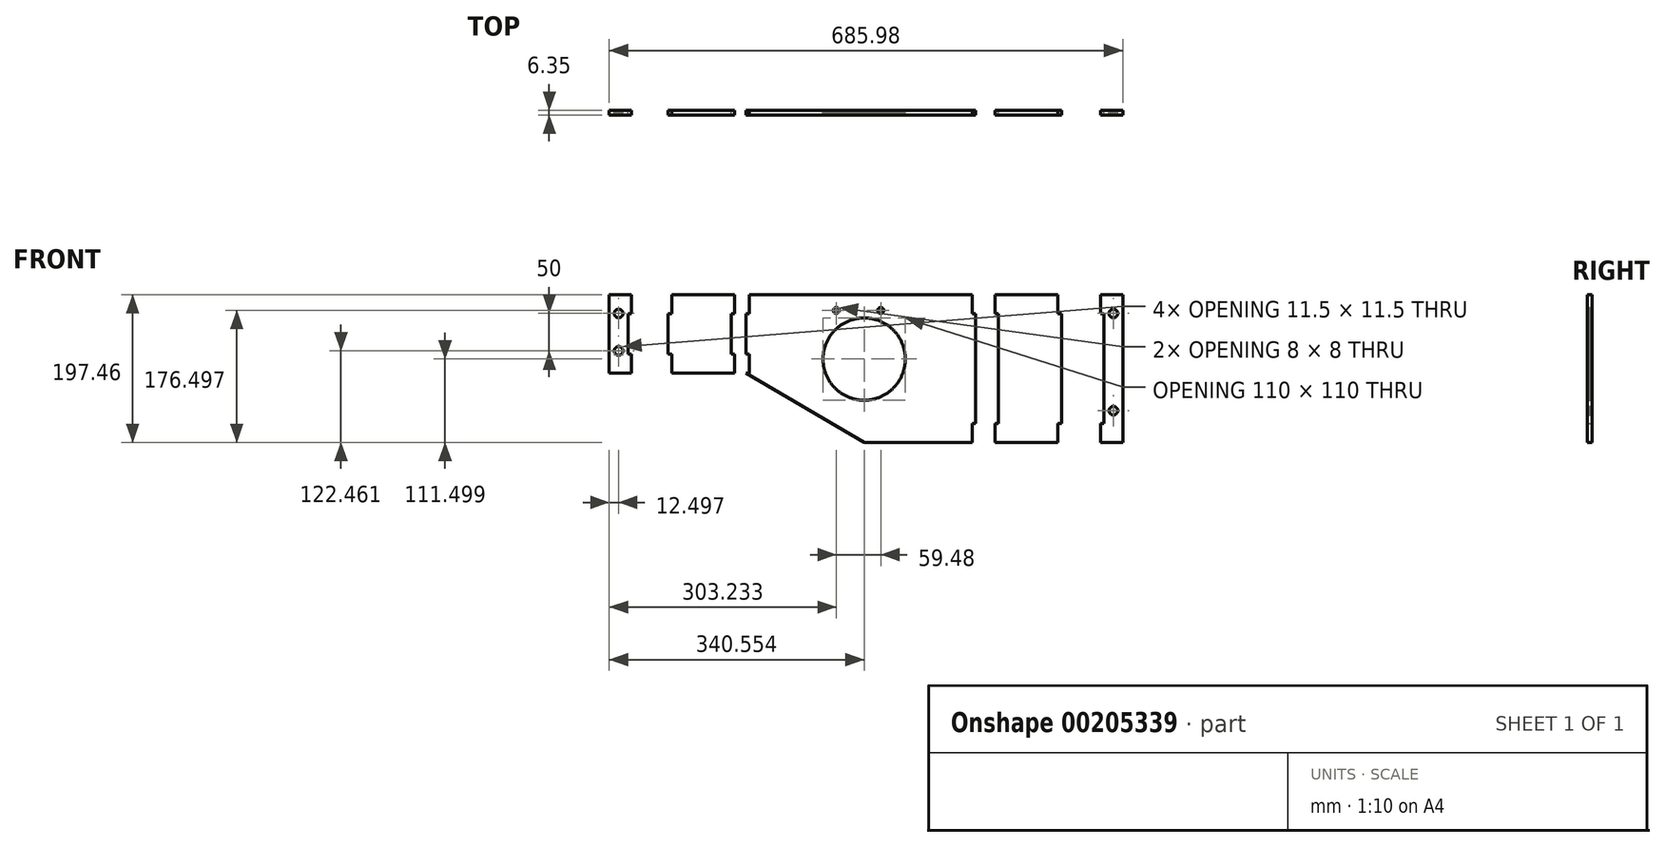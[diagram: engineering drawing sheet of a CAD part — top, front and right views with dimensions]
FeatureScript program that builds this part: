
annotation { "Feature Type Name" : "Feature", "Feature Type Description" : "" }
export const myFeature = defineFeature(function(context is Context, id is Id, definition is map)
    precondition{}
    {
        {
            var Q0;
            Q0=qCreatedBy(makeId("Front.planeOp"),FACE);
            var sketch = newSketch(context, id + "F0", { "sketchPlane" : qUnion([Q0])});
            skLineSegment(sketch, "E0", {"start": v(-330.5, 79.48) * mm, "end": v(-330.36, 79.48) * mm});
            skLineSegment(sketch, "E1", {"start": v(-330.36, 79.48) * mm, "end": v(-330.24, 79.48) * mm});
            skLineSegment(sketch, "E2", {"start": v(-330.24, 79.48) * mm, "end": v(-330.1, 79.47) * mm});
            skLineSegment(sketch, "E3", {"start": v(-330.1, 79.47) * mm, "end": v(-329.98, 79.46) * mm});
            skLineSegment(sketch, "E4", {"start": v(-329.98, 79.46) * mm, "end": v(-329.84, 79.44) * mm});
            skLineSegment(sketch, "E5", {"start": v(-329.84, 79.44) * mm, "end": v(-329.71, 79.43) * mm});
            skLineSegment(sketch, "E6", {"start": v(-329.71, 79.43) * mm, "end": v(-329.58, 79.4) * mm});
            skLineSegment(sketch, "E7", {"start": v(-329.58, 79.4) * mm, "end": v(-329.45, 79.39) * mm});
            skLineSegment(sketch, "E8", {"start": v(-329.45, 79.39) * mm, "end": v(-329.31, 79.36) * mm});
            skLineSegment(sketch, "E9", {"start": v(-329.31, 79.36) * mm, "end": v(-329.18, 79.33) * mm});
            skLineSegment(sketch, "E10", {"start": v(-329.18, 79.33) * mm, "end": v(-329.04, 79.3) * mm});
            skLineSegment(sketch, "E11", {"start": v(-329.04, 79.3) * mm, "end": v(-328.91, 79.26) * mm});
            skLineSegment(sketch, "E12", {"start": v(-328.91, 79.26) * mm, "end": v(-328.78, 79.22) * mm});
            skLineSegment(sketch, "E13", {"start": v(-328.78, 79.22) * mm, "end": v(-328.64, 79.18) * mm});
            skLineSegment(sketch, "E14", {"start": v(-328.64, 79.18) * mm, "end": v(-328.5, 79.13) * mm});
            skLineSegment(sketch, "E15", {"start": v(-328.5, 79.13) * mm, "end": v(-328.38, 79.08) * mm});
            skLineSegment(sketch, "E16", {"start": v(-328.38, 79.08) * mm, "end": v(-328.24, 79.02) * mm});
            skLineSegment(sketch, "E17", {"start": v(-328.24, 79.02) * mm, "end": v(-328.11, 78.97) * mm});
            skLineSegment(sketch, "E18", {"start": v(-328.11, 78.97) * mm, "end": v(-327.98, 78.9) * mm});
            skLineSegment(sketch, "E19", {"start": v(-327.98, 78.9) * mm, "end": v(-327.85, 78.84) * mm});
            skLineSegment(sketch, "E20", {"start": v(-327.85, 78.84) * mm, "end": v(-327.72, 78.77) * mm});
            skLineSegment(sketch, "E21", {"start": v(-327.72, 78.77) * mm, "end": v(-327.6, 78.7) * mm});
            skLineSegment(sketch, "E22", {"start": v(-327.6, 78.7) * mm, "end": v(-327.47, 78.62) * mm});
            skLineSegment(sketch, "E23", {"start": v(-327.47, 78.62) * mm, "end": v(-327.35, 78.54) * mm});
            skLineSegment(sketch, "E24", {"start": v(-327.35, 78.54) * mm, "end": v(-327.22, 78.46) * mm});
            skLineSegment(sketch, "E25", {"start": v(-327.22, 78.46) * mm, "end": v(-327.1, 78.38) * mm});
            skLineSegment(sketch, "E26", {"start": v(-327.1, 78.38) * mm, "end": v(-326.98, 78.29) * mm});
            skLineSegment(sketch, "E27", {"start": v(-326.98, 78.29) * mm, "end": v(-326.87, 78.2) * mm});
            skLineSegment(sketch, "E28", {"start": v(-326.87, 78.2) * mm, "end": v(-326.75, 78.1) * mm});
            skLineSegment(sketch, "E29", {"start": v(-326.75, 78.1) * mm, "end": v(-326.64, 78) * mm});
            skLineSegment(sketch, "E30", {"start": v(-326.64, 78) * mm, "end": v(-326.53, 77.9) * mm});
            skLineSegment(sketch, "E31", {"start": v(-326.53, 77.9) * mm, "end": v(-326.43, 77.8) * mm});
            skLineSegment(sketch, "E32", {"start": v(-326.43, 77.8) * mm, "end": v(-326.32, 77.7) * mm});
            skLineSegment(sketch, "E33", {"start": v(-326.32, 77.7) * mm, "end": v(-326.22, 77.58) * mm});
            skLineSegment(sketch, "E34", {"start": v(-326.22, 77.58) * mm, "end": v(-326.12, 77.47) * mm});
            skLineSegment(sketch, "E35", {"start": v(-326.12, 77.47) * mm, "end": v(-326.03, 77.36) * mm});
            skLineSegment(sketch, "E36", {"start": v(-326.03, 77.36) * mm, "end": v(-325.94, 77.24) * mm});
            skLineSegment(sketch, "E37", {"start": v(-325.94, 77.24) * mm, "end": v(-325.85, 77.12) * mm});
            skLineSegment(sketch, "E38", {"start": v(-325.85, 77.12) * mm, "end": v(-325.76, 77) * mm});
            skLineSegment(sketch, "E39", {"start": v(-325.76, 77) * mm, "end": v(-325.68, 76.88) * mm});
            skLineSegment(sketch, "E40", {"start": v(-325.68, 76.88) * mm, "end": v(-325.6, 76.75) * mm});
            skLineSegment(sketch, "E41", {"start": v(-325.6, 76.75) * mm, "end": v(-325.53, 76.63) * mm});
            skLineSegment(sketch, "E42", {"start": v(-325.53, 76.63) * mm, "end": v(-325.45, 76.5) * mm});
            skLineSegment(sketch, "E43", {"start": v(-325.45, 76.5) * mm, "end": v(-325.38, 76.37) * mm});
            skLineSegment(sketch, "E44", {"start": v(-325.38, 76.37) * mm, "end": v(-325.32, 76.24) * mm});
            skLineSegment(sketch, "E45", {"start": v(-325.32, 76.24) * mm, "end": v(-325.26, 76.11) * mm});
            skLineSegment(sketch, "E46", {"start": v(-325.26, 76.11) * mm, "end": v(-325.2, 75.98) * mm});
            skLineSegment(sketch, "E47", {"start": v(-325.2, 75.98) * mm, "end": v(-325.15, 75.85) * mm});
            skLineSegment(sketch, "E48", {"start": v(-325.15, 75.85) * mm, "end": v(-325.1, 75.71) * mm});
            skLineSegment(sketch, "E49", {"start": v(-325.1, 75.71) * mm, "end": v(-325.05, 75.58) * mm});
            skLineSegment(sketch, "E50", {"start": v(-325.05, 75.58) * mm, "end": v(-325, 75.45) * mm});
            skLineSegment(sketch, "E51", {"start": v(-325, 75.45) * mm, "end": v(-324.96, 75.31) * mm});
            skLineSegment(sketch, "E52", {"start": v(-324.96, 75.31) * mm, "end": v(-324.93, 75.18) * mm});
            skLineSegment(sketch, "E53", {"start": v(-324.93, 75.18) * mm, "end": v(-324.9, 75.05) * mm});
            skLineSegment(sketch, "E54", {"start": v(-324.9, 75.05) * mm, "end": v(-324.87, 74.91) * mm});
            skLineSegment(sketch, "E55", {"start": v(-324.87, 74.91) * mm, "end": v(-324.84, 74.78) * mm});
            skLineSegment(sketch, "E56", {"start": v(-324.84, 74.78) * mm, "end": v(-324.82, 74.64) * mm});
            skLineSegment(sketch, "E57", {"start": v(-324.82, 74.64) * mm, "end": v(-324.8, 74.51) * mm});
            skLineSegment(sketch, "E58", {"start": v(-324.8, 74.51) * mm, "end": v(-324.78, 74.38) * mm});
            skLineSegment(sketch, "E59", {"start": v(-324.78, 74.38) * mm, "end": v(-324.77, 74.25) * mm});
            skLineSegment(sketch, "E60", {"start": v(-324.77, 74.25) * mm, "end": v(-324.76, 74.12) * mm});
            skLineSegment(sketch, "E61", {"start": v(-324.76, 74.12) * mm, "end": v(-324.75, 73.99) * mm});
            skLineSegment(sketch, "E62", {"start": v(-324.75, 73.99) * mm, "end": v(-324.74, 73.86) * mm});
            skLineSegment(sketch, "E63", {"start": v(-324.74, 73.86) * mm, "end": v(-324.74, 73.73) * mm});
            skLineSegment(sketch, "E64", {"start": v(-324.74, 73.73) * mm, "end": v(-324.74, 73.6) * mm});
            skLineSegment(sketch, "E65", {"start": v(-324.74, 73.6) * mm, "end": v(-324.75, 73.47) * mm});
            skLineSegment(sketch, "E66", {"start": v(-324.75, 73.47) * mm, "end": v(-324.76, 73.35) * mm});
            skLineSegment(sketch, "E67", {"start": v(-324.76, 73.35) * mm, "end": v(-324.77, 73.21) * mm});
            skLineSegment(sketch, "E68", {"start": v(-324.77, 73.21) * mm, "end": v(-324.78, 73.08) * mm});
            skLineSegment(sketch, "E69", {"start": v(-324.78, 73.08) * mm, "end": v(-324.8, 72.95) * mm});
            skLineSegment(sketch, "E70", {"start": v(-324.8, 72.95) * mm, "end": v(-324.82, 72.82) * mm});
            skLineSegment(sketch, "E71", {"start": v(-324.82, 72.82) * mm, "end": v(-324.84, 72.68) * mm});
            skLineSegment(sketch, "E72", {"start": v(-324.84, 72.68) * mm, "end": v(-324.87, 72.55) * mm});
            skLineSegment(sketch, "E73", {"start": v(-324.87, 72.55) * mm, "end": v(-324.9, 72.42) * mm});
            skLineSegment(sketch, "E74", {"start": v(-324.9, 72.42) * mm, "end": v(-324.93, 72.28) * mm});
            skLineSegment(sketch, "E75", {"start": v(-324.93, 72.28) * mm, "end": v(-324.96, 72.15) * mm});
            skLineSegment(sketch, "E76", {"start": v(-324.96, 72.15) * mm, "end": v(-325, 72.02) * mm});
            skLineSegment(sketch, "E77", {"start": v(-325, 72.02) * mm, "end": v(-325.05, 71.88) * mm});
            skLineSegment(sketch, "E78", {"start": v(-325.05, 71.88) * mm, "end": v(-325.1, 71.75) * mm});
            skLineSegment(sketch, "E79", {"start": v(-325.1, 71.75) * mm, "end": v(-325.15, 71.61) * mm});
            skLineSegment(sketch, "E80", {"start": v(-325.15, 71.61) * mm, "end": v(-325.2, 71.48) * mm});
            skLineSegment(sketch, "E81", {"start": v(-325.2, 71.48) * mm, "end": v(-325.26, 71.35) * mm});
            skLineSegment(sketch, "E82", {"start": v(-325.26, 71.35) * mm, "end": v(-325.32, 71.22) * mm});
            skLineSegment(sketch, "E83", {"start": v(-325.32, 71.22) * mm, "end": v(-325.38, 71.1) * mm});
            skLineSegment(sketch, "E84", {"start": v(-325.38, 71.1) * mm, "end": v(-325.45, 70.96) * mm});
            skLineSegment(sketch, "E85", {"start": v(-325.45, 70.96) * mm, "end": v(-325.53, 70.83) * mm});
            skLineSegment(sketch, "E86", {"start": v(-325.53, 70.83) * mm, "end": v(-325.6, 70.7) * mm});
            skLineSegment(sketch, "E87", {"start": v(-325.6, 70.7) * mm, "end": v(-325.68, 70.58) * mm});
            skLineSegment(sketch, "E88", {"start": v(-325.68, 70.58) * mm, "end": v(-325.76, 70.46) * mm});
            skLineSegment(sketch, "E89", {"start": v(-325.76, 70.46) * mm, "end": v(-325.85, 70.34) * mm});
            skLineSegment(sketch, "E90", {"start": v(-325.85, 70.34) * mm, "end": v(-325.94, 70.22) * mm});
            skLineSegment(sketch, "E91", {"start": v(-325.94, 70.22) * mm, "end": v(-326.03, 70.1) * mm});
            skLineSegment(sketch, "E92", {"start": v(-326.03, 70.1) * mm, "end": v(-326.12, 70) * mm});
            skLineSegment(sketch, "E93", {"start": v(-326.12, 70) * mm, "end": v(-326.22, 69.88) * mm});
            skLineSegment(sketch, "E94", {"start": v(-326.22, 69.88) * mm, "end": v(-326.32, 69.77) * mm});
            skLineSegment(sketch, "E95", {"start": v(-326.32, 69.77) * mm, "end": v(-326.43, 69.67) * mm});
            skLineSegment(sketch, "E96", {"start": v(-326.43, 69.67) * mm, "end": v(-326.53, 69.56) * mm});
            skLineSegment(sketch, "E97", {"start": v(-326.53, 69.56) * mm, "end": v(-326.64, 69.46) * mm});
            skLineSegment(sketch, "E98", {"start": v(-326.64, 69.46) * mm, "end": v(-326.75, 69.36) * mm});
            skLineSegment(sketch, "E99", {"start": v(-326.75, 69.36) * mm, "end": v(-326.87, 69.27) * mm});
            skLineSegment(sketch, "E100", {"start": v(-326.87, 69.27) * mm, "end": v(-326.98, 69.18) * mm});
            skLineSegment(sketch, "E101", {"start": v(-326.98, 69.18) * mm, "end": v(-327.1, 69.09) * mm});
            skLineSegment(sketch, "E102", {"start": v(-327.1, 69.09) * mm, "end": v(-327.22, 69) * mm});
            skLineSegment(sketch, "E103", {"start": v(-327.22, 69) * mm, "end": v(-327.35, 68.92) * mm});
            skLineSegment(sketch, "E104", {"start": v(-327.35, 68.92) * mm, "end": v(-327.47, 68.84) * mm});
            skLineSegment(sketch, "E105", {"start": v(-327.47, 68.84) * mm, "end": v(-327.6, 68.76) * mm});
            skLineSegment(sketch, "E106", {"start": v(-327.6, 68.76) * mm, "end": v(-327.72, 68.7) * mm});
            skLineSegment(sketch, "E107", {"start": v(-327.72, 68.7) * mm, "end": v(-327.85, 68.62) * mm});
            skLineSegment(sketch, "E108", {"start": v(-327.85, 68.62) * mm, "end": v(-327.98, 68.56) * mm});
            skLineSegment(sketch, "E109", {"start": v(-327.98, 68.56) * mm, "end": v(-328.11, 68.5) * mm});
            skLineSegment(sketch, "E110", {"start": v(-328.11, 68.5) * mm, "end": v(-328.24, 68.44) * mm});
            skLineSegment(sketch, "E111", {"start": v(-328.24, 68.44) * mm, "end": v(-328.38, 68.38) * mm});
            skLineSegment(sketch, "E112", {"start": v(-328.38, 68.38) * mm, "end": v(-328.5, 68.33) * mm});
            skLineSegment(sketch, "E113", {"start": v(-328.5, 68.33) * mm, "end": v(-328.64, 68.29) * mm});
            skLineSegment(sketch, "E114", {"start": v(-328.64, 68.29) * mm, "end": v(-328.78, 68.24) * mm});
            skLineSegment(sketch, "E115", {"start": v(-328.78, 68.24) * mm, "end": v(-328.91, 68.2) * mm});
            skLineSegment(sketch, "E116", {"start": v(-328.91, 68.2) * mm, "end": v(-329.04, 68.17) * mm});
            skLineSegment(sketch, "E117", {"start": v(-329.04, 68.17) * mm, "end": v(-329.18, 68.13) * mm});
            skLineSegment(sketch, "E118", {"start": v(-329.18, 68.13) * mm, "end": v(-329.31, 68.1) * mm});
            skLineSegment(sketch, "E119", {"start": v(-329.31, 68.1) * mm, "end": v(-329.45, 68.08) * mm});
            skLineSegment(sketch, "E120", {"start": v(-329.45, 68.08) * mm, "end": v(-329.58, 68.05) * mm});
            skLineSegment(sketch, "E121", {"start": v(-329.58, 68.05) * mm, "end": v(-329.71, 68.03) * mm});
            skLineSegment(sketch, "E122", {"start": v(-329.71, 68.03) * mm, "end": v(-329.84, 68.02) * mm});
            skLineSegment(sketch, "E123", {"start": v(-329.84, 68.02) * mm, "end": v(-329.98, 68) * mm});
            skLineSegment(sketch, "E124", {"start": v(-329.98, 68) * mm, "end": v(-330.1, 68) * mm});
            skLineSegment(sketch, "E125", {"start": v(-330.1, 68) * mm, "end": v(-330.24, 67.99) * mm});
            skLineSegment(sketch, "E126", {"start": v(-330.24, 67.99) * mm, "end": v(-330.36, 67.98) * mm});
            skLineSegment(sketch, "E127", {"start": v(-330.36, 67.98) * mm, "end": v(-330.5, 67.98) * mm});
            skLineSegment(sketch, "E128", {"start": v(-330.5, 67.98) * mm, "end": v(-330.62, 67.98) * mm});
            skLineSegment(sketch, "E129", {"start": v(-330.62, 67.98) * mm, "end": v(-330.75, 67.99) * mm});
            skLineSegment(sketch, "E130", {"start": v(-330.75, 67.99) * mm, "end": v(-330.88, 68) * mm});
            skLineSegment(sketch, "E131", {"start": v(-330.88, 68) * mm, "end": v(-331, 68) * mm});
            skLineSegment(sketch, "E132", {"start": v(-331, 68) * mm, "end": v(-331.14, 68.02) * mm});
            skLineSegment(sketch, "E133", {"start": v(-331.14, 68.02) * mm, "end": v(-331.27, 68.03) * mm});
            skLineSegment(sketch, "E134", {"start": v(-331.27, 68.03) * mm, "end": v(-331.4, 68.05) * mm});
            skLineSegment(sketch, "E135", {"start": v(-331.4, 68.05) * mm, "end": v(-331.54, 68.08) * mm});
            skLineSegment(sketch, "E136", {"start": v(-331.54, 68.08) * mm, "end": v(-331.67, 68.1) * mm});
            skLineSegment(sketch, "E137", {"start": v(-331.67, 68.1) * mm, "end": v(-331.8, 68.13) * mm});
            skLineSegment(sketch, "E138", {"start": v(-331.8, 68.13) * mm, "end": v(-331.94, 68.17) * mm});
            skLineSegment(sketch, "E139", {"start": v(-331.94, 68.17) * mm, "end": v(-332.07, 68.2) * mm});
            skLineSegment(sketch, "E140", {"start": v(-332.07, 68.2) * mm, "end": v(-332.2, 68.24) * mm});
            skLineSegment(sketch, "E141", {"start": v(-332.2, 68.24) * mm, "end": v(-332.34, 68.29) * mm});
            skLineSegment(sketch, "E142", {"start": v(-332.34, 68.29) * mm, "end": v(-332.48, 68.33) * mm});
            skLineSegment(sketch, "E143", {"start": v(-332.48, 68.33) * mm, "end": v(-332.6, 68.38) * mm});
            skLineSegment(sketch, "E144", {"start": v(-332.6, 68.38) * mm, "end": v(-332.74, 68.44) * mm});
            skLineSegment(sketch, "E145", {"start": v(-332.74, 68.44) * mm, "end": v(-332.87, 68.5) * mm});
            skLineSegment(sketch, "E146", {"start": v(-332.87, 68.5) * mm, "end": v(-333, 68.56) * mm});
            skLineSegment(sketch, "E147", {"start": v(-333, 68.56) * mm, "end": v(-333.13, 68.62) * mm});
            skLineSegment(sketch, "E148", {"start": v(-333.13, 68.62) * mm, "end": v(-333.26, 68.7) * mm});
            skLineSegment(sketch, "E149", {"start": v(-333.26, 68.7) * mm, "end": v(-333.39, 68.76) * mm});
            skLineSegment(sketch, "E150", {"start": v(-333.39, 68.76) * mm, "end": v(-333.51, 68.84) * mm});
            skLineSegment(sketch, "E151", {"start": v(-333.51, 68.84) * mm, "end": v(-333.64, 68.92) * mm});
            skLineSegment(sketch, "E152", {"start": v(-333.64, 68.92) * mm, "end": v(-333.76, 69) * mm});
            skLineSegment(sketch, "E153", {"start": v(-333.76, 69) * mm, "end": v(-333.88, 69.09) * mm});
            skLineSegment(sketch, "E154", {"start": v(-333.88, 69.09) * mm, "end": v(-334, 69.18) * mm});
            skLineSegment(sketch, "E155", {"start": v(-334, 69.18) * mm, "end": v(-334.12, 69.27) * mm});
            skLineSegment(sketch, "E156", {"start": v(-334.12, 69.27) * mm, "end": v(-334.23, 69.36) * mm});
            skLineSegment(sketch, "E157", {"start": v(-334.23, 69.36) * mm, "end": v(-334.34, 69.46) * mm});
            skLineSegment(sketch, "E158", {"start": v(-334.34, 69.46) * mm, "end": v(-334.45, 69.56) * mm});
            skLineSegment(sketch, "E159", {"start": v(-334.45, 69.56) * mm, "end": v(-334.56, 69.67) * mm});
            skLineSegment(sketch, "E160", {"start": v(-334.56, 69.67) * mm, "end": v(-334.66, 69.77) * mm});
            skLineSegment(sketch, "E161", {"start": v(-334.66, 69.77) * mm, "end": v(-334.76, 69.88) * mm});
            skLineSegment(sketch, "E162", {"start": v(-334.76, 69.88) * mm, "end": v(-334.86, 70) * mm});
            skLineSegment(sketch, "E163", {"start": v(-334.86, 70) * mm, "end": v(-334.96, 70.1) * mm});
            skLineSegment(sketch, "E164", {"start": v(-334.96, 70.1) * mm, "end": v(-335.05, 70.22) * mm});
            skLineSegment(sketch, "E165", {"start": v(-335.05, 70.22) * mm, "end": v(-335.14, 70.34) * mm});
            skLineSegment(sketch, "E166", {"start": v(-335.14, 70.34) * mm, "end": v(-335.22, 70.46) * mm});
            skLineSegment(sketch, "E167", {"start": v(-335.22, 70.46) * mm, "end": v(-335.3, 70.58) * mm});
            skLineSegment(sketch, "E168", {"start": v(-335.3, 70.58) * mm, "end": v(-335.38, 70.7) * mm});
            skLineSegment(sketch, "E169", {"start": v(-335.38, 70.7) * mm, "end": v(-335.46, 70.83) * mm});
            skLineSegment(sketch, "E170", {"start": v(-335.46, 70.83) * mm, "end": v(-335.53, 70.96) * mm});
            skLineSegment(sketch, "E171", {"start": v(-335.53, 70.96) * mm, "end": v(-335.6, 71.1) * mm});
            skLineSegment(sketch, "E172", {"start": v(-335.6, 71.1) * mm, "end": v(-335.67, 71.22) * mm});
            skLineSegment(sketch, "E173", {"start": v(-335.67, 71.22) * mm, "end": v(-335.73, 71.35) * mm});
            skLineSegment(sketch, "E174", {"start": v(-335.73, 71.35) * mm, "end": v(-335.78, 71.48) * mm});
            skLineSegment(sketch, "E175", {"start": v(-335.78, 71.48) * mm, "end": v(-335.84, 71.61) * mm});
            skLineSegment(sketch, "E176", {"start": v(-335.84, 71.61) * mm, "end": v(-335.89, 71.75) * mm});
            skLineSegment(sketch, "E177", {"start": v(-335.89, 71.75) * mm, "end": v(-335.94, 71.88) * mm});
            skLineSegment(sketch, "E178", {"start": v(-335.94, 71.88) * mm, "end": v(-335.98, 72.02) * mm});
            skLineSegment(sketch, "E179", {"start": v(-335.98, 72.02) * mm, "end": v(-336.02, 72.15) * mm});
            skLineSegment(sketch, "E180", {"start": v(-336.02, 72.15) * mm, "end": v(-336.06, 72.28) * mm});
            skLineSegment(sketch, "E181", {"start": v(-336.06, 72.28) * mm, "end": v(-336.1, 72.42) * mm});
            skLineSegment(sketch, "E182", {"start": v(-336.1, 72.42) * mm, "end": v(-336.12, 72.55) * mm});
            skLineSegment(sketch, "E183", {"start": v(-336.12, 72.55) * mm, "end": v(-336.15, 72.68) * mm});
            skLineSegment(sketch, "E184", {"start": v(-336.15, 72.68) * mm, "end": v(-336.17, 72.82) * mm});
            skLineSegment(sketch, "E185", {"start": v(-336.17, 72.82) * mm, "end": v(-336.19, 72.95) * mm});
            skLineSegment(sketch, "E186", {"start": v(-336.19, 72.95) * mm, "end": v(-336.2, 73.08) * mm});
            skLineSegment(sketch, "E187", {"start": v(-336.2, 73.08) * mm, "end": v(-336.22, 73.21) * mm});
            skLineSegment(sketch, "E188", {"start": v(-336.22, 73.21) * mm, "end": v(-336.23, 73.35) * mm});
            skLineSegment(sketch, "E189", {"start": v(-336.23, 73.35) * mm, "end": v(-336.24, 73.47) * mm});
            skLineSegment(sketch, "E190", {"start": v(-336.24, 73.47) * mm, "end": v(-336.24, 73.6) * mm});
            skLineSegment(sketch, "E191", {"start": v(-336.24, 73.6) * mm, "end": v(-336.24, 73.73) * mm});
            skLineSegment(sketch, "E192", {"start": v(-336.24, 73.73) * mm, "end": v(-336.24, 73.86) * mm});
            skLineSegment(sketch, "E193", {"start": v(-336.24, 73.86) * mm, "end": v(-336.24, 73.99) * mm});
            skLineSegment(sketch, "E194", {"start": v(-336.24, 73.99) * mm, "end": v(-336.23, 74.12) * mm});
            skLineSegment(sketch, "E195", {"start": v(-336.23, 74.12) * mm, "end": v(-336.22, 74.25) * mm});
            skLineSegment(sketch, "E196", {"start": v(-336.22, 74.25) * mm, "end": v(-336.2, 74.38) * mm});
            skLineSegment(sketch, "E197", {"start": v(-336.2, 74.38) * mm, "end": v(-336.19, 74.51) * mm});
            skLineSegment(sketch, "E198", {"start": v(-336.19, 74.51) * mm, "end": v(-336.17, 74.64) * mm});
            skLineSegment(sketch, "E199", {"start": v(-336.17, 74.64) * mm, "end": v(-336.15, 74.78) * mm});
            skLineSegment(sketch, "E200", {"start": v(-336.15, 74.78) * mm, "end": v(-336.12, 74.91) * mm});
            skLineSegment(sketch, "E201", {"start": v(-336.12, 74.91) * mm, "end": v(-336.1, 75.05) * mm});
            skLineSegment(sketch, "E202", {"start": v(-336.1, 75.05) * mm, "end": v(-336.06, 75.18) * mm});
            skLineSegment(sketch, "E203", {"start": v(-336.06, 75.18) * mm, "end": v(-336.02, 75.31) * mm});
            skLineSegment(sketch, "E204", {"start": v(-336.02, 75.31) * mm, "end": v(-335.98, 75.45) * mm});
            skLineSegment(sketch, "E205", {"start": v(-335.98, 75.45) * mm, "end": v(-335.94, 75.58) * mm});
            skLineSegment(sketch, "E206", {"start": v(-335.94, 75.58) * mm, "end": v(-335.89, 75.71) * mm});
            skLineSegment(sketch, "E207", {"start": v(-335.89, 75.71) * mm, "end": v(-335.84, 75.85) * mm});
            skLineSegment(sketch, "E208", {"start": v(-335.84, 75.85) * mm, "end": v(-335.78, 75.98) * mm});
            skLineSegment(sketch, "E209", {"start": v(-335.78, 75.98) * mm, "end": v(-335.73, 76.11) * mm});
            skLineSegment(sketch, "E210", {"start": v(-335.73, 76.11) * mm, "end": v(-335.67, 76.24) * mm});
            skLineSegment(sketch, "E211", {"start": v(-335.67, 76.24) * mm, "end": v(-335.6, 76.37) * mm});
            skLineSegment(sketch, "E212", {"start": v(-335.6, 76.37) * mm, "end": v(-335.53, 76.5) * mm});
            skLineSegment(sketch, "E213", {"start": v(-335.53, 76.5) * mm, "end": v(-335.46, 76.63) * mm});
            skLineSegment(sketch, "E214", {"start": v(-335.46, 76.63) * mm, "end": v(-335.38, 76.75) * mm});
            skLineSegment(sketch, "E215", {"start": v(-335.38, 76.75) * mm, "end": v(-335.3, 76.88) * mm});
            skLineSegment(sketch, "E216", {"start": v(-335.3, 76.88) * mm, "end": v(-335.22, 77) * mm});
            skLineSegment(sketch, "E217", {"start": v(-335.22, 77) * mm, "end": v(-335.14, 77.12) * mm});
            skLineSegment(sketch, "E218", {"start": v(-335.14, 77.12) * mm, "end": v(-335.05, 77.24) * mm});
            skLineSegment(sketch, "E219", {"start": v(-335.05, 77.24) * mm, "end": v(-334.96, 77.36) * mm});
            skLineSegment(sketch, "E220", {"start": v(-334.96, 77.36) * mm, "end": v(-334.86, 77.47) * mm});
            skLineSegment(sketch, "E221", {"start": v(-334.86, 77.47) * mm, "end": v(-334.76, 77.58) * mm});
            skLineSegment(sketch, "E222", {"start": v(-334.76, 77.58) * mm, "end": v(-334.66, 77.7) * mm});
            skLineSegment(sketch, "E223", {"start": v(-334.66, 77.7) * mm, "end": v(-334.56, 77.8) * mm});
            skLineSegment(sketch, "E224", {"start": v(-334.56, 77.8) * mm, "end": v(-334.45, 77.9) * mm});
            skLineSegment(sketch, "E225", {"start": v(-334.45, 77.9) * mm, "end": v(-334.34, 78) * mm});
            skLineSegment(sketch, "E226", {"start": v(-334.34, 78) * mm, "end": v(-334.23, 78.1) * mm});
            skLineSegment(sketch, "E227", {"start": v(-334.23, 78.1) * mm, "end": v(-334.12, 78.2) * mm});
            skLineSegment(sketch, "E228", {"start": v(-334.12, 78.2) * mm, "end": v(-334, 78.29) * mm});
            skLineSegment(sketch, "E229", {"start": v(-334, 78.29) * mm, "end": v(-333.88, 78.38) * mm});
            skLineSegment(sketch, "E230", {"start": v(-333.88, 78.38) * mm, "end": v(-333.76, 78.46) * mm});
            skLineSegment(sketch, "E231", {"start": v(-333.76, 78.46) * mm, "end": v(-333.64, 78.54) * mm});
            skLineSegment(sketch, "E232", {"start": v(-333.64, 78.54) * mm, "end": v(-333.51, 78.62) * mm});
            skLineSegment(sketch, "E233", {"start": v(-333.51, 78.62) * mm, "end": v(-333.39, 78.7) * mm});
            skLineSegment(sketch, "E234", {"start": v(-333.39, 78.7) * mm, "end": v(-333.26, 78.77) * mm});
            skLineSegment(sketch, "E235", {"start": v(-333.26, 78.77) * mm, "end": v(-333.13, 78.84) * mm});
            skLineSegment(sketch, "E236", {"start": v(-333.13, 78.84) * mm, "end": v(-333, 78.9) * mm});
            skLineSegment(sketch, "E237", {"start": v(-333, 78.9) * mm, "end": v(-332.87, 78.97) * mm});
            skLineSegment(sketch, "E238", {"start": v(-332.87, 78.97) * mm, "end": v(-332.74, 79.02) * mm});
            skLineSegment(sketch, "E239", {"start": v(-332.74, 79.02) * mm, "end": v(-332.6, 79.08) * mm});
            skLineSegment(sketch, "E240", {"start": v(-332.6, 79.08) * mm, "end": v(-332.48, 79.13) * mm});
            skLineSegment(sketch, "E241", {"start": v(-332.48, 79.13) * mm, "end": v(-332.34, 79.18) * mm});
            skLineSegment(sketch, "E242", {"start": v(-332.34, 79.18) * mm, "end": v(-332.2, 79.22) * mm});
            skLineSegment(sketch, "E243", {"start": v(-332.2, 79.22) * mm, "end": v(-332.07, 79.26) * mm});
            skLineSegment(sketch, "E244", {"start": v(-332.07, 79.26) * mm, "end": v(-331.94, 79.3) * mm});
            skLineSegment(sketch, "E245", {"start": v(-331.94, 79.3) * mm, "end": v(-331.8, 79.33) * mm});
            skLineSegment(sketch, "E246", {"start": v(-331.8, 79.33) * mm, "end": v(-331.67, 79.36) * mm});
            skLineSegment(sketch, "E247", {"start": v(-331.67, 79.36) * mm, "end": v(-331.54, 79.39) * mm});
            skLineSegment(sketch, "E248", {"start": v(-331.54, 79.39) * mm, "end": v(-331.4, 79.4) * mm});
            skLineSegment(sketch, "E249", {"start": v(-331.4, 79.4) * mm, "end": v(-331.27, 79.43) * mm});
            skLineSegment(sketch, "E250", {"start": v(-331.27, 79.43) * mm, "end": v(-331.14, 79.44) * mm});
            skLineSegment(sketch, "E251", {"start": v(-331.14, 79.44) * mm, "end": v(-331, 79.46) * mm});
            skLineSegment(sketch, "E252", {"start": v(-331, 79.46) * mm, "end": v(-330.88, 79.47) * mm});
            skLineSegment(sketch, "E253", {"start": v(-330.88, 79.47) * mm, "end": v(-330.75, 79.48) * mm});
            skLineSegment(sketch, "E254", {"start": v(-330.75, 79.48) * mm, "end": v(-330.62, 79.48) * mm});
            skLineSegment(sketch, "E255", {"start": v(-330.62, 79.48) * mm, "end": v(-330.5, 79.48) * mm});
            skLineSegment(sketch, "E256", {"start": v(-330.5, 29.48) * mm, "end": v(-330.36, 29.48) * mm});
            skLineSegment(sketch, "E257", {"start": v(-330.36, 29.48) * mm, "end": v(-330.24, 29.48) * mm});
            skLineSegment(sketch, "E258", {"start": v(-330.24, 29.48) * mm, "end": v(-330.1, 29.47) * mm});
            skLineSegment(sketch, "E259", {"start": v(-330.1, 29.47) * mm, "end": v(-329.98, 29.46) * mm});
            skLineSegment(sketch, "E260", {"start": v(-329.98, 29.46) * mm, "end": v(-329.84, 29.44) * mm});
            skLineSegment(sketch, "E261", {"start": v(-329.84, 29.44) * mm, "end": v(-329.71, 29.43) * mm});
            skLineSegment(sketch, "E262", {"start": v(-329.71, 29.43) * mm, "end": v(-329.58, 29.4) * mm});
            skLineSegment(sketch, "E263", {"start": v(-329.58, 29.4) * mm, "end": v(-329.45, 29.39) * mm});
            skLineSegment(sketch, "E264", {"start": v(-329.45, 29.39) * mm, "end": v(-329.31, 29.36) * mm});
            skLineSegment(sketch, "E265", {"start": v(-329.31, 29.36) * mm, "end": v(-329.18, 29.33) * mm});
            skLineSegment(sketch, "E266", {"start": v(-329.18, 29.33) * mm, "end": v(-329.04, 29.3) * mm});
            skLineSegment(sketch, "E267", {"start": v(-329.04, 29.3) * mm, "end": v(-328.91, 29.26) * mm});
            skLineSegment(sketch, "E268", {"start": v(-328.91, 29.26) * mm, "end": v(-328.78, 29.22) * mm});
            skLineSegment(sketch, "E269", {"start": v(-328.78, 29.22) * mm, "end": v(-328.64, 29.18) * mm});
            skLineSegment(sketch, "E270", {"start": v(-328.64, 29.18) * mm, "end": v(-328.5, 29.13) * mm});
            skLineSegment(sketch, "E271", {"start": v(-328.5, 29.13) * mm, "end": v(-328.38, 29.08) * mm});
            skLineSegment(sketch, "E272", {"start": v(-328.38, 29.08) * mm, "end": v(-328.24, 29.02) * mm});
            skLineSegment(sketch, "E273", {"start": v(-328.24, 29.02) * mm, "end": v(-328.11, 28.97) * mm});
            skLineSegment(sketch, "E274", {"start": v(-328.11, 28.97) * mm, "end": v(-327.98, 28.9) * mm});
            skLineSegment(sketch, "E275", {"start": v(-327.98, 28.9) * mm, "end": v(-327.85, 28.84) * mm});
            skLineSegment(sketch, "E276", {"start": v(-327.85, 28.84) * mm, "end": v(-327.72, 28.77) * mm});
            skLineSegment(sketch, "E277", {"start": v(-327.72, 28.77) * mm, "end": v(-327.6, 28.7) * mm});
            skLineSegment(sketch, "E278", {"start": v(-327.6, 28.7) * mm, "end": v(-327.47, 28.62) * mm});
            skLineSegment(sketch, "E279", {"start": v(-327.47, 28.62) * mm, "end": v(-327.35, 28.54) * mm});
            skLineSegment(sketch, "E280", {"start": v(-327.35, 28.54) * mm, "end": v(-327.22, 28.46) * mm});
            skLineSegment(sketch, "E281", {"start": v(-327.22, 28.46) * mm, "end": v(-327.1, 28.38) * mm});
            skLineSegment(sketch, "E282", {"start": v(-327.1, 28.38) * mm, "end": v(-326.98, 28.29) * mm});
            skLineSegment(sketch, "E283", {"start": v(-326.98, 28.29) * mm, "end": v(-326.87, 28.2) * mm});
            skLineSegment(sketch, "E284", {"start": v(-326.87, 28.2) * mm, "end": v(-326.75, 28.1) * mm});
            skLineSegment(sketch, "E285", {"start": v(-326.75, 28.1) * mm, "end": v(-326.64, 28) * mm});
            skLineSegment(sketch, "E286", {"start": v(-326.64, 28) * mm, "end": v(-326.53, 27.9) * mm});
            skLineSegment(sketch, "E287", {"start": v(-326.53, 27.9) * mm, "end": v(-326.43, 27.8) * mm});
            skLineSegment(sketch, "E288", {"start": v(-326.43, 27.8) * mm, "end": v(-326.32, 27.7) * mm});
            skLineSegment(sketch, "E289", {"start": v(-326.32, 27.7) * mm, "end": v(-326.22, 27.58) * mm});
            skLineSegment(sketch, "E290", {"start": v(-326.22, 27.58) * mm, "end": v(-326.12, 27.47) * mm});
            skLineSegment(sketch, "E291", {"start": v(-326.12, 27.47) * mm, "end": v(-326.03, 27.36) * mm});
            skLineSegment(sketch, "E292", {"start": v(-326.03, 27.36) * mm, "end": v(-325.94, 27.24) * mm});
            skLineSegment(sketch, "E293", {"start": v(-325.94, 27.24) * mm, "end": v(-325.85, 27.12) * mm});
            skLineSegment(sketch, "E294", {"start": v(-325.85, 27.12) * mm, "end": v(-325.76, 27) * mm});
            skLineSegment(sketch, "E295", {"start": v(-325.76, 27) * mm, "end": v(-325.68, 26.88) * mm});
            skLineSegment(sketch, "E296", {"start": v(-325.68, 26.88) * mm, "end": v(-325.6, 26.75) * mm});
            skLineSegment(sketch, "E297", {"start": v(-325.6, 26.75) * mm, "end": v(-325.53, 26.63) * mm});
            skLineSegment(sketch, "E298", {"start": v(-325.53, 26.63) * mm, "end": v(-325.45, 26.5) * mm});
            skLineSegment(sketch, "E299", {"start": v(-325.45, 26.5) * mm, "end": v(-325.38, 26.37) * mm});
            skLineSegment(sketch, "E300", {"start": v(-325.38, 26.37) * mm, "end": v(-325.32, 26.24) * mm});
            skLineSegment(sketch, "E301", {"start": v(-325.32, 26.24) * mm, "end": v(-325.26, 26.11) * mm});
            skLineSegment(sketch, "E302", {"start": v(-325.26, 26.11) * mm, "end": v(-325.2, 25.98) * mm});
            skLineSegment(sketch, "E303", {"start": v(-325.2, 25.98) * mm, "end": v(-325.15, 25.85) * mm});
            skLineSegment(sketch, "E304", {"start": v(-325.15, 25.85) * mm, "end": v(-325.1, 25.71) * mm});
            skLineSegment(sketch, "E305", {"start": v(-325.1, 25.71) * mm, "end": v(-325.05, 25.58) * mm});
            skLineSegment(sketch, "E306", {"start": v(-325.05, 25.58) * mm, "end": v(-325, 25.45) * mm});
            skLineSegment(sketch, "E307", {"start": v(-325, 25.45) * mm, "end": v(-324.96, 25.31) * mm});
            skLineSegment(sketch, "E308", {"start": v(-324.96, 25.31) * mm, "end": v(-324.93, 25.18) * mm});
            skLineSegment(sketch, "E309", {"start": v(-324.93, 25.18) * mm, "end": v(-324.9, 25.05) * mm});
            skLineSegment(sketch, "E310", {"start": v(-324.9, 25.05) * mm, "end": v(-324.87, 24.91) * mm});
            skLineSegment(sketch, "E311", {"start": v(-324.87, 24.91) * mm, "end": v(-324.84, 24.78) * mm});
            skLineSegment(sketch, "E312", {"start": v(-324.84, 24.78) * mm, "end": v(-324.82, 24.64) * mm});
            skLineSegment(sketch, "E313", {"start": v(-324.82, 24.64) * mm, "end": v(-324.8, 24.51) * mm});
            skLineSegment(sketch, "E314", {"start": v(-324.8, 24.51) * mm, "end": v(-324.78, 24.38) * mm});
            skLineSegment(sketch, "E315", {"start": v(-324.78, 24.38) * mm, "end": v(-324.77, 24.25) * mm});
            skLineSegment(sketch, "E316", {"start": v(-324.77, 24.25) * mm, "end": v(-324.76, 24.12) * mm});
            skLineSegment(sketch, "E317", {"start": v(-324.76, 24.12) * mm, "end": v(-324.75, 23.99) * mm});
            skLineSegment(sketch, "E318", {"start": v(-324.75, 23.99) * mm, "end": v(-324.74, 23.86) * mm});
            skLineSegment(sketch, "E319", {"start": v(-324.74, 23.86) * mm, "end": v(-324.74, 23.73) * mm});
            skLineSegment(sketch, "E320", {"start": v(-324.74, 23.73) * mm, "end": v(-324.74, 23.6) * mm});
            skLineSegment(sketch, "E321", {"start": v(-324.74, 23.6) * mm, "end": v(-324.75, 23.47) * mm});
            skLineSegment(sketch, "E322", {"start": v(-324.75, 23.47) * mm, "end": v(-324.76, 23.35) * mm});
            skLineSegment(sketch, "E323", {"start": v(-324.76, 23.35) * mm, "end": v(-324.77, 23.21) * mm});
            skLineSegment(sketch, "E324", {"start": v(-324.77, 23.21) * mm, "end": v(-324.78, 23.08) * mm});
            skLineSegment(sketch, "E325", {"start": v(-324.78, 23.08) * mm, "end": v(-324.8, 22.95) * mm});
            skLineSegment(sketch, "E326", {"start": v(-324.8, 22.95) * mm, "end": v(-324.82, 22.82) * mm});
            skLineSegment(sketch, "E327", {"start": v(-324.82, 22.82) * mm, "end": v(-324.84, 22.68) * mm});
            skLineSegment(sketch, "E328", {"start": v(-324.84, 22.68) * mm, "end": v(-324.87, 22.55) * mm});
            skLineSegment(sketch, "E329", {"start": v(-324.87, 22.55) * mm, "end": v(-324.9, 22.42) * mm});
            skLineSegment(sketch, "E330", {"start": v(-324.9, 22.42) * mm, "end": v(-324.93, 22.28) * mm});
            skLineSegment(sketch, "E331", {"start": v(-324.93, 22.28) * mm, "end": v(-324.96, 22.15) * mm});
            skLineSegment(sketch, "E332", {"start": v(-324.96, 22.15) * mm, "end": v(-325, 22.02) * mm});
            skLineSegment(sketch, "E333", {"start": v(-325, 22.02) * mm, "end": v(-325.05, 21.88) * mm});
            skLineSegment(sketch, "E334", {"start": v(-325.05, 21.88) * mm, "end": v(-325.1, 21.75) * mm});
            skLineSegment(sketch, "E335", {"start": v(-325.1, 21.75) * mm, "end": v(-325.15, 21.61) * mm});
            skLineSegment(sketch, "E336", {"start": v(-325.15, 21.61) * mm, "end": v(-325.2, 21.48) * mm});
            skLineSegment(sketch, "E337", {"start": v(-325.2, 21.48) * mm, "end": v(-325.26, 21.35) * mm});
            skLineSegment(sketch, "E338", {"start": v(-325.26, 21.35) * mm, "end": v(-325.32, 21.22) * mm});
            skLineSegment(sketch, "E339", {"start": v(-325.32, 21.22) * mm, "end": v(-325.38, 21.1) * mm});
            skLineSegment(sketch, "E340", {"start": v(-325.38, 21.1) * mm, "end": v(-325.45, 20.96) * mm});
            skLineSegment(sketch, "E341", {"start": v(-325.45, 20.96) * mm, "end": v(-325.53, 20.83) * mm});
            skLineSegment(sketch, "E342", {"start": v(-325.53, 20.83) * mm, "end": v(-325.6, 20.7) * mm});
            skLineSegment(sketch, "E343", {"start": v(-325.6, 20.7) * mm, "end": v(-325.68, 20.58) * mm});
            skLineSegment(sketch, "E344", {"start": v(-325.68, 20.58) * mm, "end": v(-325.76, 20.46) * mm});
            skLineSegment(sketch, "E345", {"start": v(-325.76, 20.46) * mm, "end": v(-325.85, 20.34) * mm});
            skLineSegment(sketch, "E346", {"start": v(-325.85, 20.34) * mm, "end": v(-325.94, 20.22) * mm});
            skLineSegment(sketch, "E347", {"start": v(-325.94, 20.22) * mm, "end": v(-326.03, 20.1) * mm});
            skLineSegment(sketch, "E348", {"start": v(-326.03, 20.1) * mm, "end": v(-326.12, 20) * mm});
            skLineSegment(sketch, "E349", {"start": v(-326.12, 20) * mm, "end": v(-326.22, 19.88) * mm});
            skLineSegment(sketch, "E350", {"start": v(-326.22, 19.88) * mm, "end": v(-326.32, 19.77) * mm});
            skLineSegment(sketch, "E351", {"start": v(-326.32, 19.77) * mm, "end": v(-326.43, 19.67) * mm});
            skLineSegment(sketch, "E352", {"start": v(-326.43, 19.67) * mm, "end": v(-326.53, 19.56) * mm});
            skLineSegment(sketch, "E353", {"start": v(-326.53, 19.56) * mm, "end": v(-326.64, 19.46) * mm});
            skLineSegment(sketch, "E354", {"start": v(-326.64, 19.46) * mm, "end": v(-326.75, 19.36) * mm});
            skLineSegment(sketch, "E355", {"start": v(-326.75, 19.36) * mm, "end": v(-326.87, 19.27) * mm});
            skLineSegment(sketch, "E356", {"start": v(-326.87, 19.27) * mm, "end": v(-326.98, 19.18) * mm});
            skLineSegment(sketch, "E357", {"start": v(-326.98, 19.18) * mm, "end": v(-327.1, 19.09) * mm});
            skLineSegment(sketch, "E358", {"start": v(-327.1, 19.09) * mm, "end": v(-327.22, 19) * mm});
            skLineSegment(sketch, "E359", {"start": v(-327.22, 19) * mm, "end": v(-327.35, 18.92) * mm});
            skLineSegment(sketch, "E360", {"start": v(-327.35, 18.92) * mm, "end": v(-327.47, 18.84) * mm});
            skLineSegment(sketch, "E361", {"start": v(-327.47, 18.84) * mm, "end": v(-327.6, 18.76) * mm});
            skLineSegment(sketch, "E362", {"start": v(-327.6, 18.76) * mm, "end": v(-327.72, 18.7) * mm});
            skLineSegment(sketch, "E363", {"start": v(-327.72, 18.7) * mm, "end": v(-327.85, 18.62) * mm});
            skLineSegment(sketch, "E364", {"start": v(-327.85, 18.62) * mm, "end": v(-327.98, 18.56) * mm});
            skLineSegment(sketch, "E365", {"start": v(-327.98, 18.56) * mm, "end": v(-328.11, 18.5) * mm});
            skLineSegment(sketch, "E366", {"start": v(-328.11, 18.5) * mm, "end": v(-328.24, 18.44) * mm});
            skLineSegment(sketch, "E367", {"start": v(-328.24, 18.44) * mm, "end": v(-328.38, 18.38) * mm});
            skLineSegment(sketch, "E368", {"start": v(-328.38, 18.38) * mm, "end": v(-328.5, 18.33) * mm});
            skLineSegment(sketch, "E369", {"start": v(-328.5, 18.33) * mm, "end": v(-328.64, 18.29) * mm});
            skLineSegment(sketch, "E370", {"start": v(-328.64, 18.29) * mm, "end": v(-328.78, 18.24) * mm});
            skLineSegment(sketch, "E371", {"start": v(-328.78, 18.24) * mm, "end": v(-328.91, 18.2) * mm});
            skLineSegment(sketch, "E372", {"start": v(-328.91, 18.2) * mm, "end": v(-329.04, 18.17) * mm});
            skLineSegment(sketch, "E373", {"start": v(-329.04, 18.17) * mm, "end": v(-329.18, 18.13) * mm});
            skLineSegment(sketch, "E374", {"start": v(-329.18, 18.13) * mm, "end": v(-329.31, 18.1) * mm});
            skLineSegment(sketch, "E375", {"start": v(-329.31, 18.1) * mm, "end": v(-329.45, 18.08) * mm});
            skLineSegment(sketch, "E376", {"start": v(-329.45, 18.08) * mm, "end": v(-329.58, 18.05) * mm});
            skLineSegment(sketch, "E377", {"start": v(-329.58, 18.05) * mm, "end": v(-329.71, 18.03) * mm});
            skLineSegment(sketch, "E378", {"start": v(-329.71, 18.03) * mm, "end": v(-329.84, 18.02) * mm});
            skLineSegment(sketch, "E379", {"start": v(-329.84, 18.02) * mm, "end": v(-329.98, 18) * mm});
            skLineSegment(sketch, "E380", {"start": v(-329.98, 18) * mm, "end": v(-330.1, 18) * mm});
            skLineSegment(sketch, "E381", {"start": v(-330.1, 18) * mm, "end": v(-330.24, 17.99) * mm});
            skLineSegment(sketch, "E382", {"start": v(-330.24, 17.99) * mm, "end": v(-330.36, 17.98) * mm});
            skLineSegment(sketch, "E383", {"start": v(-330.36, 17.98) * mm, "end": v(-330.5, 17.98) * mm});
            skLineSegment(sketch, "E384", {"start": v(-330.5, 17.98) * mm, "end": v(-330.62, 17.98) * mm});
            skLineSegment(sketch, "E385", {"start": v(-330.62, 17.98) * mm, "end": v(-330.75, 17.99) * mm});
            skLineSegment(sketch, "E386", {"start": v(-330.75, 17.99) * mm, "end": v(-330.88, 18) * mm});
            skLineSegment(sketch, "E387", {"start": v(-330.88, 18) * mm, "end": v(-331, 18) * mm});
            skLineSegment(sketch, "E388", {"start": v(-331, 18) * mm, "end": v(-331.14, 18.02) * mm});
            skLineSegment(sketch, "E389", {"start": v(-331.14, 18.02) * mm, "end": v(-331.27, 18.03) * mm});
            skLineSegment(sketch, "E390", {"start": v(-331.27, 18.03) * mm, "end": v(-331.4, 18.05) * mm});
            skLineSegment(sketch, "E391", {"start": v(-331.4, 18.05) * mm, "end": v(-331.54, 18.08) * mm});
            skLineSegment(sketch, "E392", {"start": v(-331.54, 18.08) * mm, "end": v(-331.67, 18.1) * mm});
            skLineSegment(sketch, "E393", {"start": v(-331.67, 18.1) * mm, "end": v(-331.8, 18.13) * mm});
            skLineSegment(sketch, "E394", {"start": v(-331.8, 18.13) * mm, "end": v(-331.94, 18.17) * mm});
            skLineSegment(sketch, "E395", {"start": v(-331.94, 18.17) * mm, "end": v(-332.07, 18.2) * mm});
            skLineSegment(sketch, "E396", {"start": v(-332.07, 18.2) * mm, "end": v(-332.2, 18.24) * mm});
            skLineSegment(sketch, "E397", {"start": v(-332.2, 18.24) * mm, "end": v(-332.34, 18.29) * mm});
            skLineSegment(sketch, "E398", {"start": v(-332.34, 18.29) * mm, "end": v(-332.48, 18.33) * mm});
            skLineSegment(sketch, "E399", {"start": v(-332.48, 18.33) * mm, "end": v(-332.6, 18.38) * mm});
            skLineSegment(sketch, "E400", {"start": v(-332.6, 18.38) * mm, "end": v(-332.74, 18.44) * mm});
            skLineSegment(sketch, "E401", {"start": v(-332.74, 18.44) * mm, "end": v(-332.87, 18.5) * mm});
            skLineSegment(sketch, "E402", {"start": v(-332.87, 18.5) * mm, "end": v(-333, 18.56) * mm});
            skLineSegment(sketch, "E403", {"start": v(-333, 18.56) * mm, "end": v(-333.13, 18.62) * mm});
            skLineSegment(sketch, "E404", {"start": v(-333.13, 18.62) * mm, "end": v(-333.26, 18.7) * mm});
            skLineSegment(sketch, "E405", {"start": v(-333.26, 18.7) * mm, "end": v(-333.39, 18.76) * mm});
            skLineSegment(sketch, "E406", {"start": v(-333.39, 18.76) * mm, "end": v(-333.51, 18.84) * mm});
            skLineSegment(sketch, "E407", {"start": v(-333.51, 18.84) * mm, "end": v(-333.64, 18.92) * mm});
            skLineSegment(sketch, "E408", {"start": v(-333.64, 18.92) * mm, "end": v(-333.76, 19) * mm});
            skLineSegment(sketch, "E409", {"start": v(-333.76, 19) * mm, "end": v(-333.88, 19.09) * mm});
            skLineSegment(sketch, "E410", {"start": v(-333.88, 19.09) * mm, "end": v(-334, 19.18) * mm});
            skLineSegment(sketch, "E411", {"start": v(-334, 19.18) * mm, "end": v(-334.12, 19.27) * mm});
            skLineSegment(sketch, "E412", {"start": v(-334.12, 19.27) * mm, "end": v(-334.23, 19.36) * mm});
            skLineSegment(sketch, "E413", {"start": v(-334.23, 19.36) * mm, "end": v(-334.34, 19.46) * mm});
            skLineSegment(sketch, "E414", {"start": v(-334.34, 19.46) * mm, "end": v(-334.45, 19.56) * mm});
            skLineSegment(sketch, "E415", {"start": v(-334.45, 19.56) * mm, "end": v(-334.56, 19.67) * mm});
            skLineSegment(sketch, "E416", {"start": v(-334.56, 19.67) * mm, "end": v(-334.66, 19.77) * mm});
            skLineSegment(sketch, "E417", {"start": v(-334.66, 19.77) * mm, "end": v(-334.76, 19.88) * mm});
            skLineSegment(sketch, "E418", {"start": v(-334.76, 19.88) * mm, "end": v(-334.86, 20) * mm});
            skLineSegment(sketch, "E419", {"start": v(-334.86, 20) * mm, "end": v(-334.96, 20.1) * mm});
            skLineSegment(sketch, "E420", {"start": v(-334.96, 20.1) * mm, "end": v(-335.05, 20.22) * mm});
            skLineSegment(sketch, "E421", {"start": v(-335.05, 20.22) * mm, "end": v(-335.14, 20.34) * mm});
            skLineSegment(sketch, "E422", {"start": v(-335.14, 20.34) * mm, "end": v(-335.22, 20.46) * mm});
            skLineSegment(sketch, "E423", {"start": v(-335.22, 20.46) * mm, "end": v(-335.3, 20.58) * mm});
            skLineSegment(sketch, "E424", {"start": v(-335.3, 20.58) * mm, "end": v(-335.38, 20.7) * mm});
            skLineSegment(sketch, "E425", {"start": v(-335.38, 20.7) * mm, "end": v(-335.46, 20.83) * mm});
            skLineSegment(sketch, "E426", {"start": v(-335.46, 20.83) * mm, "end": v(-335.53, 20.96) * mm});
            skLineSegment(sketch, "E427", {"start": v(-335.53, 20.96) * mm, "end": v(-335.6, 21.1) * mm});
            skLineSegment(sketch, "E428", {"start": v(-335.6, 21.1) * mm, "end": v(-335.67, 21.22) * mm});
            skLineSegment(sketch, "E429", {"start": v(-335.67, 21.22) * mm, "end": v(-335.73, 21.35) * mm});
            skLineSegment(sketch, "E430", {"start": v(-335.73, 21.35) * mm, "end": v(-335.78, 21.48) * mm});
            skLineSegment(sketch, "E431", {"start": v(-335.78, 21.48) * mm, "end": v(-335.84, 21.61) * mm});
            skLineSegment(sketch, "E432", {"start": v(-335.84, 21.61) * mm, "end": v(-335.89, 21.75) * mm});
            skLineSegment(sketch, "E433", {"start": v(-335.89, 21.75) * mm, "end": v(-335.94, 21.88) * mm});
            skLineSegment(sketch, "E434", {"start": v(-335.94, 21.88) * mm, "end": v(-335.98, 22.02) * mm});
            skLineSegment(sketch, "E435", {"start": v(-335.98, 22.02) * mm, "end": v(-336.02, 22.15) * mm});
            skLineSegment(sketch, "E436", {"start": v(-336.02, 22.15) * mm, "end": v(-336.06, 22.28) * mm});
            skLineSegment(sketch, "E437", {"start": v(-336.06, 22.28) * mm, "end": v(-336.1, 22.42) * mm});
            skLineSegment(sketch, "E438", {"start": v(-336.1, 22.42) * mm, "end": v(-336.12, 22.55) * mm});
            skLineSegment(sketch, "E439", {"start": v(-336.12, 22.55) * mm, "end": v(-336.15, 22.68) * mm});
            skLineSegment(sketch, "E440", {"start": v(-336.15, 22.68) * mm, "end": v(-336.17, 22.82) * mm});
            skLineSegment(sketch, "E441", {"start": v(-336.17, 22.82) * mm, "end": v(-336.19, 22.95) * mm});
            skLineSegment(sketch, "E442", {"start": v(-336.19, 22.95) * mm, "end": v(-336.2, 23.08) * mm});
            skLineSegment(sketch, "E443", {"start": v(-336.2, 23.08) * mm, "end": v(-336.22, 23.21) * mm});
            skLineSegment(sketch, "E444", {"start": v(-336.22, 23.21) * mm, "end": v(-336.23, 23.35) * mm});
            skLineSegment(sketch, "E445", {"start": v(-336.23, 23.35) * mm, "end": v(-336.24, 23.47) * mm});
            skLineSegment(sketch, "E446", {"start": v(-336.24, 23.47) * mm, "end": v(-336.24, 23.6) * mm});
            skLineSegment(sketch, "E447", {"start": v(-336.24, 23.6) * mm, "end": v(-336.24, 23.73) * mm});
            skLineSegment(sketch, "E448", {"start": v(-336.24, 23.73) * mm, "end": v(-336.24, 23.86) * mm});
            skLineSegment(sketch, "E449", {"start": v(-336.24, 23.86) * mm, "end": v(-336.24, 23.99) * mm});
            skLineSegment(sketch, "E450", {"start": v(-336.24, 23.99) * mm, "end": v(-336.23, 24.12) * mm});
            skLineSegment(sketch, "E451", {"start": v(-336.23, 24.12) * mm, "end": v(-336.22, 24.25) * mm});
            skLineSegment(sketch, "E452", {"start": v(-336.22, 24.25) * mm, "end": v(-336.2, 24.38) * mm});
            skLineSegment(sketch, "E453", {"start": v(-336.2, 24.38) * mm, "end": v(-336.19, 24.51) * mm});
            skLineSegment(sketch, "E454", {"start": v(-336.19, 24.51) * mm, "end": v(-336.17, 24.64) * mm});
            skLineSegment(sketch, "E455", {"start": v(-336.17, 24.64) * mm, "end": v(-336.15, 24.78) * mm});
            skLineSegment(sketch, "E456", {"start": v(-336.15, 24.78) * mm, "end": v(-336.12, 24.91) * mm});
            skLineSegment(sketch, "E457", {"start": v(-336.12, 24.91) * mm, "end": v(-336.1, 25.05) * mm});
            skLineSegment(sketch, "E458", {"start": v(-336.1, 25.05) * mm, "end": v(-336.06, 25.18) * mm});
            skLineSegment(sketch, "E459", {"start": v(-336.06, 25.18) * mm, "end": v(-336.02, 25.31) * mm});
            skLineSegment(sketch, "E460", {"start": v(-336.02, 25.31) * mm, "end": v(-335.98, 25.45) * mm});
            skLineSegment(sketch, "E461", {"start": v(-335.98, 25.45) * mm, "end": v(-335.94, 25.58) * mm});
            skLineSegment(sketch, "E462", {"start": v(-335.94, 25.58) * mm, "end": v(-335.89, 25.71) * mm});
            skLineSegment(sketch, "E463", {"start": v(-335.89, 25.71) * mm, "end": v(-335.84, 25.85) * mm});
            skLineSegment(sketch, "E464", {"start": v(-335.84, 25.85) * mm, "end": v(-335.78, 25.98) * mm});
            skLineSegment(sketch, "E465", {"start": v(-335.78, 25.98) * mm, "end": v(-335.73, 26.11) * mm});
            skLineSegment(sketch, "E466", {"start": v(-335.73, 26.11) * mm, "end": v(-335.67, 26.24) * mm});
            skLineSegment(sketch, "E467", {"start": v(-335.67, 26.24) * mm, "end": v(-335.6, 26.37) * mm});
            skLineSegment(sketch, "E468", {"start": v(-335.6, 26.37) * mm, "end": v(-335.53, 26.5) * mm});
            skLineSegment(sketch, "E469", {"start": v(-335.53, 26.5) * mm, "end": v(-335.46, 26.63) * mm});
            skLineSegment(sketch, "E470", {"start": v(-335.46, 26.63) * mm, "end": v(-335.38, 26.75) * mm});
            skLineSegment(sketch, "E471", {"start": v(-335.38, 26.75) * mm, "end": v(-335.3, 26.88) * mm});
            skLineSegment(sketch, "E472", {"start": v(-335.3, 26.88) * mm, "end": v(-335.22, 27) * mm});
            skLineSegment(sketch, "E473", {"start": v(-335.22, 27) * mm, "end": v(-335.14, 27.12) * mm});
            skLineSegment(sketch, "E474", {"start": v(-335.14, 27.12) * mm, "end": v(-335.05, 27.24) * mm});
            skLineSegment(sketch, "E475", {"start": v(-335.05, 27.24) * mm, "end": v(-334.96, 27.36) * mm});
            skLineSegment(sketch, "E476", {"start": v(-334.96, 27.36) * mm, "end": v(-334.86, 27.47) * mm});
            skLineSegment(sketch, "E477", {"start": v(-334.86, 27.47) * mm, "end": v(-334.76, 27.58) * mm});
            skLineSegment(sketch, "E478", {"start": v(-334.76, 27.58) * mm, "end": v(-334.66, 27.7) * mm});
            skLineSegment(sketch, "E479", {"start": v(-334.66, 27.7) * mm, "end": v(-334.56, 27.8) * mm});
            skLineSegment(sketch, "E480", {"start": v(-334.56, 27.8) * mm, "end": v(-334.45, 27.9) * mm});
            skLineSegment(sketch, "E481", {"start": v(-334.45, 27.9) * mm, "end": v(-334.34, 28) * mm});
            skLineSegment(sketch, "E482", {"start": v(-334.34, 28) * mm, "end": v(-334.23, 28.1) * mm});
            skLineSegment(sketch, "E483", {"start": v(-334.23, 28.1) * mm, "end": v(-334.12, 28.2) * mm});
            skLineSegment(sketch, "E484", {"start": v(-334.12, 28.2) * mm, "end": v(-334, 28.29) * mm});
            skLineSegment(sketch, "E485", {"start": v(-334, 28.29) * mm, "end": v(-333.88, 28.38) * mm});
            skLineSegment(sketch, "E486", {"start": v(-333.88, 28.38) * mm, "end": v(-333.76, 28.46) * mm});
            skLineSegment(sketch, "E487", {"start": v(-333.76, 28.46) * mm, "end": v(-333.64, 28.54) * mm});
            skLineSegment(sketch, "E488", {"start": v(-333.64, 28.54) * mm, "end": v(-333.51, 28.62) * mm});
            skLineSegment(sketch, "E489", {"start": v(-333.51, 28.62) * mm, "end": v(-333.39, 28.7) * mm});
            skLineSegment(sketch, "E490", {"start": v(-333.39, 28.7) * mm, "end": v(-333.26, 28.77) * mm});
            skLineSegment(sketch, "E491", {"start": v(-333.26, 28.77) * mm, "end": v(-333.13, 28.84) * mm});
            skLineSegment(sketch, "E492", {"start": v(-333.13, 28.84) * mm, "end": v(-333, 28.9) * mm});
            skLineSegment(sketch, "E493", {"start": v(-333, 28.9) * mm, "end": v(-332.87, 28.97) * mm});
            skLineSegment(sketch, "E494", {"start": v(-332.87, 28.97) * mm, "end": v(-332.74, 29.02) * mm});
            skLineSegment(sketch, "E495", {"start": v(-332.74, 29.02) * mm, "end": v(-332.6, 29.08) * mm});
            skLineSegment(sketch, "E496", {"start": v(-332.6, 29.08) * mm, "end": v(-332.48, 29.13) * mm});
            skLineSegment(sketch, "E497", {"start": v(-332.48, 29.13) * mm, "end": v(-332.34, 29.18) * mm});
            skLineSegment(sketch, "E498", {"start": v(-332.34, 29.18) * mm, "end": v(-332.2, 29.22) * mm});
            skLineSegment(sketch, "E499", {"start": v(-332.2, 29.22) * mm, "end": v(-332.07, 29.26) * mm});
            skLineSegment(sketch, "E500", {"start": v(-332.07, 29.26) * mm, "end": v(-331.94, 29.3) * mm});
            skLineSegment(sketch, "E501", {"start": v(-331.94, 29.3) * mm, "end": v(-331.8, 29.33) * mm});
            skLineSegment(sketch, "E502", {"start": v(-331.8, 29.33) * mm, "end": v(-331.67, 29.36) * mm});
            skLineSegment(sketch, "E503", {"start": v(-331.67, 29.36) * mm, "end": v(-331.54, 29.39) * mm});
            skLineSegment(sketch, "E504", {"start": v(-331.54, 29.39) * mm, "end": v(-331.4, 29.4) * mm});
            skLineSegment(sketch, "E505", {"start": v(-331.4, 29.4) * mm, "end": v(-331.27, 29.43) * mm});
            skLineSegment(sketch, "E506", {"start": v(-331.27, 29.43) * mm, "end": v(-331.14, 29.44) * mm});
            skLineSegment(sketch, "E507", {"start": v(-331.14, 29.44) * mm, "end": v(-331, 29.46) * mm});
            skLineSegment(sketch, "E508", {"start": v(-331, 29.46) * mm, "end": v(-330.88, 29.47) * mm});
            skLineSegment(sketch, "E509", {"start": v(-330.88, 29.47) * mm, "end": v(-330.75, 29.48) * mm});
            skLineSegment(sketch, "E510", {"start": v(-330.75, 29.48) * mm, "end": v(-330.62, 29.48) * mm});
            skLineSegment(sketch, "E511", {"start": v(-330.62, 29.48) * mm, "end": v(-330.5, 29.48) * mm});
            skLineSegment(sketch, "E512", {"start": v(-313.23, -6.23) * mm, "end": v(-313.23, 19.17) * mm});
            skLineSegment(sketch, "E513", {"start": v(-313.23, 19.17) * mm, "end": v(-318, 19.17) * mm});
            skLineSegment(sketch, "E514", {"start": v(-318, 19.17) * mm, "end": v(-318, 73.33) * mm});
            skLineSegment(sketch, "E515", {"start": v(-318, 73.33) * mm, "end": v(-313.23, 73.33) * mm});
            skLineSegment(sketch, "E516", {"start": v(-313.23, 73.33) * mm, "end": v(-313.23, 98.73) * mm});
            skLineSegment(sketch, "E517", {"start": v(-313.23, 98.73) * mm, "end": v(-318, 98.73) * mm});
            skLineSegment(sketch, "E518", {"start": v(-318, 98.73) * mm, "end": v(-343, 98.73) * mm});
            skLineSegment(sketch, "E519", {"start": v(-343, 98.73) * mm, "end": v(-343, -6.23) * mm});
            skLineSegment(sketch, "E520", {"start": v(-343, -6.23) * mm, "end": v(-318, -6.23) * mm});
            skLineSegment(sketch, "E521", {"start": v(-318, -6.23) * mm, "end": v(-313.23, -6.23) * mm});
            skLineSegment(sketch, "E522", {"start": v(-259.5, 19.17) * mm, "end": v(-259.5, -6.23) * mm});
            skLineSegment(sketch, "E523", {"start": v(-259.5, -6.23) * mm, "end": v(-180.03, -6.23) * mm});
            skLineSegment(sketch, "E524", {"start": v(-180.03, -6.23) * mm, "end": v(-175.27, -6.23) * mm});
            skLineSegment(sketch, "E525", {"start": v(-175.27, -6.23) * mm, "end": v(-175.27, 19.17) * mm});
            skLineSegment(sketch, "E526", {"start": v(-175.27, 19.17) * mm, "end": v(-180.03, 19.17) * mm});
            skLineSegment(sketch, "E527", {"start": v(-180.03, 19.17) * mm, "end": v(-180.03, 73.33) * mm});
            skLineSegment(sketch, "E528", {"start": v(-180.03, 73.33) * mm, "end": v(-175.27, 73.33) * mm});
            skLineSegment(sketch, "E529", {"start": v(-175.27, 73.33) * mm, "end": v(-175.27, 98.73) * mm});
            skLineSegment(sketch, "E530", {"start": v(-175.27, 98.73) * mm, "end": v(-180.03, 98.73) * mm});
            skLineSegment(sketch, "E531", {"start": v(-180.03, 98.73) * mm, "end": v(-259.5, 98.73) * mm});
            skLineSegment(sketch, "E532", {"start": v(-259.5, 98.73) * mm, "end": v(-259.5, 73.33) * mm});
            skLineSegment(sketch, "E533", {"start": v(-259.5, 73.33) * mm, "end": v(-264.27, 73.33) * mm});
            skLineSegment(sketch, "E534", {"start": v(-264.27, 73.33) * mm, "end": v(-264.27, 19.17) * mm});
            skLineSegment(sketch, "E535", {"start": v(-264.27, 19.17) * mm, "end": v(-259.5, 19.17) * mm});
            skLineSegment(sketch, "E536", {"start": v(-39.76, 81.77) * mm, "end": v(-39.67, 81.77) * mm});
            skLineSegment(sketch, "E537", {"start": v(-39.67, 81.77) * mm, "end": v(-39.58, 81.76) * mm});
            skLineSegment(sketch, "E538", {"start": v(-39.58, 81.76) * mm, "end": v(-39.49, 81.76) * mm});
            skLineSegment(sketch, "E539", {"start": v(-39.49, 81.76) * mm, "end": v(-39.4, 81.75) * mm});
            skLineSegment(sketch, "E540", {"start": v(-39.4, 81.75) * mm, "end": v(-39.3, 81.74) * mm});
            skLineSegment(sketch, "E541", {"start": v(-39.3, 81.74) * mm, "end": v(-39.21, 81.73) * mm});
            skLineSegment(sketch, "E542", {"start": v(-39.21, 81.73) * mm, "end": v(-39.12, 81.72) * mm});
            skLineSegment(sketch, "E543", {"start": v(-39.12, 81.72) * mm, "end": v(-39.03, 81.7) * mm});
            skLineSegment(sketch, "E544", {"start": v(-39.03, 81.7) * mm, "end": v(-38.94, 81.68) * mm});
            skLineSegment(sketch, "E545", {"start": v(-38.94, 81.68) * mm, "end": v(-38.84, 81.66) * mm});
            skLineSegment(sketch, "E546", {"start": v(-38.84, 81.66) * mm, "end": v(-38.75, 81.64) * mm});
            skLineSegment(sketch, "E547", {"start": v(-38.75, 81.64) * mm, "end": v(-38.66, 81.61) * mm});
            skLineSegment(sketch, "E548", {"start": v(-38.66, 81.61) * mm, "end": v(-38.56, 81.59) * mm});
            skLineSegment(sketch, "E549", {"start": v(-38.56, 81.59) * mm, "end": v(-38.47, 81.55) * mm});
            skLineSegment(sketch, "E550", {"start": v(-38.47, 81.55) * mm, "end": v(-38.38, 81.52) * mm});
            skLineSegment(sketch, "E551", {"start": v(-38.38, 81.52) * mm, "end": v(-38.29, 81.49) * mm});
            skLineSegment(sketch, "E552", {"start": v(-38.29, 81.49) * mm, "end": v(-38.2, 81.45) * mm});
            skLineSegment(sketch, "E553", {"start": v(-38.2, 81.45) * mm, "end": v(-38.1, 81.4) * mm});
            skLineSegment(sketch, "E554", {"start": v(-38.1, 81.4) * mm, "end": v(-38.01, 81.37) * mm});
            skLineSegment(sketch, "E555", {"start": v(-38.01, 81.37) * mm, "end": v(-37.92, 81.32) * mm});
            skLineSegment(sketch, "E556", {"start": v(-37.92, 81.32) * mm, "end": v(-37.83, 81.27) * mm});
            skLineSegment(sketch, "E557", {"start": v(-37.83, 81.27) * mm, "end": v(-37.74, 81.22) * mm});
            skLineSegment(sketch, "E558", {"start": v(-37.74, 81.22) * mm, "end": v(-37.66, 81.17) * mm});
            skLineSegment(sketch, "E559", {"start": v(-37.66, 81.17) * mm, "end": v(-37.57, 81.12) * mm});
            skLineSegment(sketch, "E560", {"start": v(-37.57, 81.12) * mm, "end": v(-37.48, 81.06) * mm});
            skLineSegment(sketch, "E561", {"start": v(-37.48, 81.06) * mm, "end": v(-37.4, 81) * mm});
            skLineSegment(sketch, "E562", {"start": v(-37.4, 81) * mm, "end": v(-37.32, 80.94) * mm});
            skLineSegment(sketch, "E563", {"start": v(-37.32, 80.94) * mm, "end": v(-37.24, 80.87) * mm});
            skLineSegment(sketch, "E564", {"start": v(-37.24, 80.87) * mm, "end": v(-37.16, 80.8) * mm});
            skLineSegment(sketch, "E565", {"start": v(-37.16, 80.8) * mm, "end": v(-37.08, 80.74) * mm});
            skLineSegment(sketch, "E566", {"start": v(-37.08, 80.74) * mm, "end": v(-37, 80.67) * mm});
            skLineSegment(sketch, "E567", {"start": v(-37, 80.67) * mm, "end": v(-36.93, 80.6) * mm});
            skLineSegment(sketch, "E568", {"start": v(-36.93, 80.6) * mm, "end": v(-36.86, 80.52) * mm});
            skLineSegment(sketch, "E569", {"start": v(-36.86, 80.52) * mm, "end": v(-36.79, 80.45) * mm});
            skLineSegment(sketch, "E570", {"start": v(-36.79, 80.45) * mm, "end": v(-36.72, 80.37) * mm});
            skLineSegment(sketch, "E571", {"start": v(-36.72, 80.37) * mm, "end": v(-36.65, 80.29) * mm});
            skLineSegment(sketch, "E572", {"start": v(-36.65, 80.29) * mm, "end": v(-36.59, 80.2) * mm});
            skLineSegment(sketch, "E573", {"start": v(-36.59, 80.2) * mm, "end": v(-36.53, 80.13) * mm});
            skLineSegment(sketch, "E574", {"start": v(-36.53, 80.13) * mm, "end": v(-36.47, 80.04) * mm});
            skLineSegment(sketch, "E575", {"start": v(-36.47, 80.04) * mm, "end": v(-36.4, 79.96) * mm});
            skLineSegment(sketch, "E576", {"start": v(-36.4, 79.96) * mm, "end": v(-36.35, 79.87) * mm});
            skLineSegment(sketch, "E577", {"start": v(-36.35, 79.87) * mm, "end": v(-36.3, 79.78) * mm});
            skLineSegment(sketch, "E578", {"start": v(-36.3, 79.78) * mm, "end": v(-36.25, 79.7) * mm});
            skLineSegment(sketch, "E579", {"start": v(-36.25, 79.7) * mm, "end": v(-36.2, 79.6) * mm});
            skLineSegment(sketch, "E580", {"start": v(-36.2, 79.6) * mm, "end": v(-36.16, 79.51) * mm});
            skLineSegment(sketch, "E581", {"start": v(-36.16, 79.51) * mm, "end": v(-36.12, 79.42) * mm});
            skLineSegment(sketch, "E582", {"start": v(-36.12, 79.42) * mm, "end": v(-36.08, 79.33) * mm});
            skLineSegment(sketch, "E583", {"start": v(-36.08, 79.33) * mm, "end": v(-36.04, 79.24) * mm});
            skLineSegment(sketch, "E584", {"start": v(-36.04, 79.24) * mm, "end": v(-36, 79.15) * mm});
            skLineSegment(sketch, "E585", {"start": v(-36, 79.15) * mm, "end": v(-35.97, 79.05) * mm});
            skLineSegment(sketch, "E586", {"start": v(-35.97, 79.05) * mm, "end": v(-35.94, 78.96) * mm});
            skLineSegment(sketch, "E587", {"start": v(-35.94, 78.96) * mm, "end": v(-35.91, 78.87) * mm});
            skLineSegment(sketch, "E588", {"start": v(-35.91, 78.87) * mm, "end": v(-35.89, 78.77) * mm});
            skLineSegment(sketch, "E589", {"start": v(-35.89, 78.77) * mm, "end": v(-35.86, 78.68) * mm});
            skLineSegment(sketch, "E590", {"start": v(-35.86, 78.68) * mm, "end": v(-35.84, 78.59) * mm});
            skLineSegment(sketch, "E591", {"start": v(-35.84, 78.59) * mm, "end": v(-35.82, 78.5) * mm});
            skLineSegment(sketch, "E592", {"start": v(-35.82, 78.5) * mm, "end": v(-35.8, 78.4) * mm});
            skLineSegment(sketch, "E593", {"start": v(-35.8, 78.4) * mm, "end": v(-35.8, 78.31) * mm});
            skLineSegment(sketch, "E594", {"start": v(-35.8, 78.31) * mm, "end": v(-35.78, 78.22) * mm});
            skLineSegment(sketch, "E595", {"start": v(-35.78, 78.22) * mm, "end": v(-35.77, 78.13) * mm});
            skLineSegment(sketch, "E596", {"start": v(-35.77, 78.13) * mm, "end": v(-35.77, 78.04) * mm});
            skLineSegment(sketch, "E597", {"start": v(-35.77, 78.04) * mm, "end": v(-35.76, 77.95) * mm});
            skLineSegment(sketch, "E598", {"start": v(-35.76, 77.95) * mm, "end": v(-35.76, 77.86) * mm});
            skLineSegment(sketch, "E599", {"start": v(-35.76, 77.86) * mm, "end": v(-35.76, 77.77) * mm});
            skLineSegment(sketch, "E600", {"start": v(-35.76, 77.77) * mm, "end": v(-35.76, 77.68) * mm});
            skLineSegment(sketch, "E601", {"start": v(-35.76, 77.68) * mm, "end": v(-35.76, 77.59) * mm});
            skLineSegment(sketch, "E602", {"start": v(-35.76, 77.59) * mm, "end": v(-35.77, 77.5) * mm});
            skLineSegment(sketch, "E603", {"start": v(-35.77, 77.5) * mm, "end": v(-35.77, 77.4) * mm});
            skLineSegment(sketch, "E604", {"start": v(-35.77, 77.4) * mm, "end": v(-35.78, 77.32) * mm});
            skLineSegment(sketch, "E605", {"start": v(-35.78, 77.32) * mm, "end": v(-35.8, 77.22) * mm});
            skLineSegment(sketch, "E606", {"start": v(-35.8, 77.22) * mm, "end": v(-35.8, 77.13) * mm});
            skLineSegment(sketch, "E607", {"start": v(-35.8, 77.13) * mm, "end": v(-35.82, 77.04) * mm});
            skLineSegment(sketch, "E608", {"start": v(-35.82, 77.04) * mm, "end": v(-35.84, 76.95) * mm});
            skLineSegment(sketch, "E609", {"start": v(-35.84, 76.95) * mm, "end": v(-35.86, 76.85) * mm});
            skLineSegment(sketch, "E610", {"start": v(-35.86, 76.85) * mm, "end": v(-35.89, 76.76) * mm});
            skLineSegment(sketch, "E611", {"start": v(-35.89, 76.76) * mm, "end": v(-35.91, 76.67) * mm});
            skLineSegment(sketch, "E612", {"start": v(-35.91, 76.67) * mm, "end": v(-35.94, 76.57) * mm});
            skLineSegment(sketch, "E613", {"start": v(-35.94, 76.57) * mm, "end": v(-35.97, 76.48) * mm});
            skLineSegment(sketch, "E614", {"start": v(-35.97, 76.48) * mm, "end": v(-36, 76.39) * mm});
            skLineSegment(sketch, "E615", {"start": v(-36, 76.39) * mm, "end": v(-36.04, 76.3) * mm});
            skLineSegment(sketch, "E616", {"start": v(-36.04, 76.3) * mm, "end": v(-36.08, 76.2) * mm});
            skLineSegment(sketch, "E617", {"start": v(-36.08, 76.2) * mm, "end": v(-36.12, 76.11) * mm});
            skLineSegment(sketch, "E618", {"start": v(-36.12, 76.11) * mm, "end": v(-36.16, 76.02) * mm});
            skLineSegment(sketch, "E619", {"start": v(-36.16, 76.02) * mm, "end": v(-36.2, 75.93) * mm});
            skLineSegment(sketch, "E620", {"start": v(-36.2, 75.93) * mm, "end": v(-36.25, 75.84) * mm});
            skLineSegment(sketch, "E621", {"start": v(-36.25, 75.84) * mm, "end": v(-36.3, 75.75) * mm});
            skLineSegment(sketch, "E622", {"start": v(-36.3, 75.75) * mm, "end": v(-36.35, 75.66) * mm});
            skLineSegment(sketch, "E623", {"start": v(-36.35, 75.66) * mm, "end": v(-36.4, 75.58) * mm});
            skLineSegment(sketch, "E624", {"start": v(-36.4, 75.58) * mm, "end": v(-36.47, 75.5) * mm});
            skLineSegment(sketch, "E625", {"start": v(-36.47, 75.5) * mm, "end": v(-36.53, 75.4) * mm});
            skLineSegment(sketch, "E626", {"start": v(-36.53, 75.4) * mm, "end": v(-36.59, 75.33) * mm});
            skLineSegment(sketch, "E627", {"start": v(-36.59, 75.33) * mm, "end": v(-36.65, 75.25) * mm});
            skLineSegment(sketch, "E628", {"start": v(-36.65, 75.25) * mm, "end": v(-36.72, 75.17) * mm});
            skLineSegment(sketch, "E629", {"start": v(-36.72, 75.17) * mm, "end": v(-36.79, 75.09) * mm});
            skLineSegment(sketch, "E630", {"start": v(-36.79, 75.09) * mm, "end": v(-36.86, 75.01) * mm});
            skLineSegment(sketch, "E631", {"start": v(-36.86, 75.01) * mm, "end": v(-36.93, 74.94) * mm});
            skLineSegment(sketch, "E632", {"start": v(-36.93, 74.94) * mm, "end": v(-37, 74.87) * mm});
            skLineSegment(sketch, "E633", {"start": v(-37, 74.87) * mm, "end": v(-37.08, 74.8) * mm});
            skLineSegment(sketch, "E634", {"start": v(-37.08, 74.8) * mm, "end": v(-37.16, 74.73) * mm});
            skLineSegment(sketch, "E635", {"start": v(-37.16, 74.73) * mm, "end": v(-37.24, 74.66) * mm});
            skLineSegment(sketch, "E636", {"start": v(-37.24, 74.66) * mm, "end": v(-37.32, 74.6) * mm});
            skLineSegment(sketch, "E637", {"start": v(-37.32, 74.6) * mm, "end": v(-37.4, 74.54) * mm});
            skLineSegment(sketch, "E638", {"start": v(-37.4, 74.54) * mm, "end": v(-37.48, 74.48) * mm});
            skLineSegment(sketch, "E639", {"start": v(-37.48, 74.48) * mm, "end": v(-37.57, 74.42) * mm});
            skLineSegment(sketch, "E640", {"start": v(-37.57, 74.42) * mm, "end": v(-37.66, 74.36) * mm});
            skLineSegment(sketch, "E641", {"start": v(-37.66, 74.36) * mm, "end": v(-37.74, 74.31) * mm});
            skLineSegment(sketch, "E642", {"start": v(-37.74, 74.31) * mm, "end": v(-37.83, 74.26) * mm});
            skLineSegment(sketch, "E643", {"start": v(-37.83, 74.26) * mm, "end": v(-37.92, 74.21) * mm});
            skLineSegment(sketch, "E644", {"start": v(-37.92, 74.21) * mm, "end": v(-38.01, 74.17) * mm});
            skLineSegment(sketch, "E645", {"start": v(-38.01, 74.17) * mm, "end": v(-38.1, 74.13) * mm});
            skLineSegment(sketch, "E646", {"start": v(-38.1, 74.13) * mm, "end": v(-38.2, 74.09) * mm});
            skLineSegment(sketch, "E647", {"start": v(-38.2, 74.09) * mm, "end": v(-38.29, 74.05) * mm});
            skLineSegment(sketch, "E648", {"start": v(-38.29, 74.05) * mm, "end": v(-38.38, 74.01) * mm});
            skLineSegment(sketch, "E649", {"start": v(-38.38, 74.01) * mm, "end": v(-38.47, 73.98) * mm});
            skLineSegment(sketch, "E650", {"start": v(-38.47, 73.98) * mm, "end": v(-38.56, 73.95) * mm});
            skLineSegment(sketch, "E651", {"start": v(-38.56, 73.95) * mm, "end": v(-38.66, 73.92) * mm});
            skLineSegment(sketch, "E652", {"start": v(-38.66, 73.92) * mm, "end": v(-38.75, 73.9) * mm});
            skLineSegment(sketch, "E653", {"start": v(-38.75, 73.9) * mm, "end": v(-38.84, 73.87) * mm});
            skLineSegment(sketch, "E654", {"start": v(-38.84, 73.87) * mm, "end": v(-38.94, 73.85) * mm});
            skLineSegment(sketch, "E655", {"start": v(-38.94, 73.85) * mm, "end": v(-39.03, 73.83) * mm});
            skLineSegment(sketch, "E656", {"start": v(-39.03, 73.83) * mm, "end": v(-39.12, 73.82) * mm});
            skLineSegment(sketch, "E657", {"start": v(-39.12, 73.82) * mm, "end": v(-39.21, 73.8) * mm});
            skLineSegment(sketch, "E658", {"start": v(-39.21, 73.8) * mm, "end": v(-39.3, 73.8) * mm});
            skLineSegment(sketch, "E659", {"start": v(-39.3, 73.8) * mm, "end": v(-39.4, 73.78) * mm});
            skLineSegment(sketch, "E660", {"start": v(-39.4, 73.78) * mm, "end": v(-39.49, 73.78) * mm});
            skLineSegment(sketch, "E661", {"start": v(-39.49, 73.78) * mm, "end": v(-39.58, 73.77) * mm});
            skLineSegment(sketch, "E662", {"start": v(-39.58, 73.77) * mm, "end": v(-39.67, 73.77) * mm});
            skLineSegment(sketch, "E663", {"start": v(-39.67, 73.77) * mm, "end": v(-39.76, 73.77) * mm});
            skLineSegment(sketch, "E664", {"start": v(-39.76, 73.77) * mm, "end": v(-39.85, 73.77) * mm});
            skLineSegment(sketch, "E665", {"start": v(-39.85, 73.77) * mm, "end": v(-39.94, 73.77) * mm});
            skLineSegment(sketch, "E666", {"start": v(-39.94, 73.77) * mm, "end": v(-40.03, 73.78) * mm});
            skLineSegment(sketch, "E667", {"start": v(-40.03, 73.78) * mm, "end": v(-40.12, 73.78) * mm});
            skLineSegment(sketch, "E668", {"start": v(-40.12, 73.78) * mm, "end": v(-40.2, 73.8) * mm});
            skLineSegment(sketch, "E669", {"start": v(-40.2, 73.8) * mm, "end": v(-40.3, 73.8) * mm});
            skLineSegment(sketch, "E670", {"start": v(-40.3, 73.8) * mm, "end": v(-40.4, 73.82) * mm});
            skLineSegment(sketch, "E671", {"start": v(-40.4, 73.82) * mm, "end": v(-40.49, 73.83) * mm});
            skLineSegment(sketch, "E672", {"start": v(-40.49, 73.83) * mm, "end": v(-40.58, 73.85) * mm});
            skLineSegment(sketch, "E673", {"start": v(-40.58, 73.85) * mm, "end": v(-40.67, 73.87) * mm});
            skLineSegment(sketch, "E674", {"start": v(-40.67, 73.87) * mm, "end": v(-40.76, 73.9) * mm});
            skLineSegment(sketch, "E675", {"start": v(-40.76, 73.9) * mm, "end": v(-40.86, 73.92) * mm});
            skLineSegment(sketch, "E676", {"start": v(-40.86, 73.92) * mm, "end": v(-40.95, 73.95) * mm});
            skLineSegment(sketch, "E677", {"start": v(-40.95, 73.95) * mm, "end": v(-41.04, 73.98) * mm});
            skLineSegment(sketch, "E678", {"start": v(-41.04, 73.98) * mm, "end": v(-41.14, 74.01) * mm});
            skLineSegment(sketch, "E679", {"start": v(-41.14, 74.01) * mm, "end": v(-41.23, 74.05) * mm});
            skLineSegment(sketch, "E680", {"start": v(-41.23, 74.05) * mm, "end": v(-41.32, 74.09) * mm});
            skLineSegment(sketch, "E681", {"start": v(-41.32, 74.09) * mm, "end": v(-41.41, 74.13) * mm});
            skLineSegment(sketch, "E682", {"start": v(-41.41, 74.13) * mm, "end": v(-41.5, 74.17) * mm});
            skLineSegment(sketch, "E683", {"start": v(-41.5, 74.17) * mm, "end": v(-41.6, 74.21) * mm});
            skLineSegment(sketch, "E684", {"start": v(-41.6, 74.21) * mm, "end": v(-41.68, 74.26) * mm});
            skLineSegment(sketch, "E685", {"start": v(-41.68, 74.26) * mm, "end": v(-41.77, 74.31) * mm});
            skLineSegment(sketch, "E686", {"start": v(-41.77, 74.31) * mm, "end": v(-41.86, 74.36) * mm});
            skLineSegment(sketch, "E687", {"start": v(-41.86, 74.36) * mm, "end": v(-41.95, 74.42) * mm});
            skLineSegment(sketch, "E688", {"start": v(-41.95, 74.42) * mm, "end": v(-42.03, 74.48) * mm});
            skLineSegment(sketch, "E689", {"start": v(-42.03, 74.48) * mm, "end": v(-42.12, 74.54) * mm});
            skLineSegment(sketch, "E690", {"start": v(-42.12, 74.54) * mm, "end": v(-42.2, 74.6) * mm});
            skLineSegment(sketch, "E691", {"start": v(-42.2, 74.6) * mm, "end": v(-42.28, 74.66) * mm});
            skLineSegment(sketch, "E692", {"start": v(-42.28, 74.66) * mm, "end": v(-42.36, 74.73) * mm});
            skLineSegment(sketch, "E693", {"start": v(-42.36, 74.73) * mm, "end": v(-42.44, 74.8) * mm});
            skLineSegment(sketch, "E694", {"start": v(-42.44, 74.8) * mm, "end": v(-42.51, 74.87) * mm});
            skLineSegment(sketch, "E695", {"start": v(-42.51, 74.87) * mm, "end": v(-42.59, 74.94) * mm});
            skLineSegment(sketch, "E696", {"start": v(-42.59, 74.94) * mm, "end": v(-42.66, 75.01) * mm});
            skLineSegment(sketch, "E697", {"start": v(-42.66, 75.01) * mm, "end": v(-42.73, 75.09) * mm});
            skLineSegment(sketch, "E698", {"start": v(-42.73, 75.09) * mm, "end": v(-42.8, 75.17) * mm});
            skLineSegment(sketch, "E699", {"start": v(-42.8, 75.17) * mm, "end": v(-42.86, 75.25) * mm});
            skLineSegment(sketch, "E700", {"start": v(-42.86, 75.25) * mm, "end": v(-42.93, 75.33) * mm});
            skLineSegment(sketch, "E701", {"start": v(-42.93, 75.33) * mm, "end": v(-42.99, 75.4) * mm});
            skLineSegment(sketch, "E702", {"start": v(-42.99, 75.4) * mm, "end": v(-43.05, 75.5) * mm});
            skLineSegment(sketch, "E703", {"start": v(-43.05, 75.5) * mm, "end": v(-43.1, 75.58) * mm});
            skLineSegment(sketch, "E704", {"start": v(-43.1, 75.58) * mm, "end": v(-43.16, 75.66) * mm});
            skLineSegment(sketch, "E705", {"start": v(-43.16, 75.66) * mm, "end": v(-43.21, 75.75) * mm});
            skLineSegment(sketch, "E706", {"start": v(-43.21, 75.75) * mm, "end": v(-43.26, 75.84) * mm});
            skLineSegment(sketch, "E707", {"start": v(-43.26, 75.84) * mm, "end": v(-43.31, 75.93) * mm});
            skLineSegment(sketch, "E708", {"start": v(-43.31, 75.93) * mm, "end": v(-43.36, 76.02) * mm});
            skLineSegment(sketch, "E709", {"start": v(-43.36, 76.02) * mm, "end": v(-43.4, 76.11) * mm});
            skLineSegment(sketch, "E710", {"start": v(-43.4, 76.11) * mm, "end": v(-43.44, 76.2) * mm});
            skLineSegment(sketch, "E711", {"start": v(-43.44, 76.2) * mm, "end": v(-43.48, 76.3) * mm});
            skLineSegment(sketch, "E712", {"start": v(-43.48, 76.3) * mm, "end": v(-43.51, 76.39) * mm});
            skLineSegment(sketch, "E713", {"start": v(-43.51, 76.39) * mm, "end": v(-43.54, 76.48) * mm});
            skLineSegment(sketch, "E714", {"start": v(-43.54, 76.48) * mm, "end": v(-43.58, 76.57) * mm});
            skLineSegment(sketch, "E715", {"start": v(-43.58, 76.57) * mm, "end": v(-43.6, 76.67) * mm});
            skLineSegment(sketch, "E716", {"start": v(-43.6, 76.67) * mm, "end": v(-43.63, 76.76) * mm});
            skLineSegment(sketch, "E717", {"start": v(-43.63, 76.76) * mm, "end": v(-43.65, 76.85) * mm});
            skLineSegment(sketch, "E718", {"start": v(-43.65, 76.85) * mm, "end": v(-43.67, 76.95) * mm});
            skLineSegment(sketch, "E719", {"start": v(-43.67, 76.95) * mm, "end": v(-43.7, 77.04) * mm});
            skLineSegment(sketch, "E720", {"start": v(-43.7, 77.04) * mm, "end": v(-43.7, 77.13) * mm});
            skLineSegment(sketch, "E721", {"start": v(-43.7, 77.13) * mm, "end": v(-43.72, 77.22) * mm});
            skLineSegment(sketch, "E722", {"start": v(-43.72, 77.22) * mm, "end": v(-43.73, 77.32) * mm});
            skLineSegment(sketch, "E723", {"start": v(-43.73, 77.32) * mm, "end": v(-43.74, 77.4) * mm});
            skLineSegment(sketch, "E724", {"start": v(-43.74, 77.4) * mm, "end": v(-43.75, 77.5) * mm});
            skLineSegment(sketch, "E725", {"start": v(-43.75, 77.5) * mm, "end": v(-43.75, 77.59) * mm});
            skLineSegment(sketch, "E726", {"start": v(-43.75, 77.59) * mm, "end": v(-43.76, 77.68) * mm});
            skLineSegment(sketch, "E727", {"start": v(-43.76, 77.68) * mm, "end": v(-43.76, 77.77) * mm});
            skLineSegment(sketch, "E728", {"start": v(-43.76, 77.77) * mm, "end": v(-43.76, 77.86) * mm});
            skLineSegment(sketch, "E729", {"start": v(-43.76, 77.86) * mm, "end": v(-43.75, 77.95) * mm});
            skLineSegment(sketch, "E730", {"start": v(-43.75, 77.95) * mm, "end": v(-43.75, 78.04) * mm});
            skLineSegment(sketch, "E731", {"start": v(-43.75, 78.04) * mm, "end": v(-43.74, 78.13) * mm});
            skLineSegment(sketch, "E732", {"start": v(-43.74, 78.13) * mm, "end": v(-43.73, 78.22) * mm});
            skLineSegment(sketch, "E733", {"start": v(-43.73, 78.22) * mm, "end": v(-43.72, 78.31) * mm});
            skLineSegment(sketch, "E734", {"start": v(-43.72, 78.31) * mm, "end": v(-43.7, 78.4) * mm});
            skLineSegment(sketch, "E735", {"start": v(-43.7, 78.4) * mm, "end": v(-43.7, 78.5) * mm});
            skLineSegment(sketch, "E736", {"start": v(-43.7, 78.5) * mm, "end": v(-43.67, 78.59) * mm});
            skLineSegment(sketch, "E737", {"start": v(-43.67, 78.59) * mm, "end": v(-43.65, 78.68) * mm});
            skLineSegment(sketch, "E738", {"start": v(-43.65, 78.68) * mm, "end": v(-43.63, 78.77) * mm});
            skLineSegment(sketch, "E739", {"start": v(-43.63, 78.77) * mm, "end": v(-43.6, 78.87) * mm});
            skLineSegment(sketch, "E740", {"start": v(-43.6, 78.87) * mm, "end": v(-43.58, 78.96) * mm});
            skLineSegment(sketch, "E741", {"start": v(-43.58, 78.96) * mm, "end": v(-43.54, 79.05) * mm});
            skLineSegment(sketch, "E742", {"start": v(-43.54, 79.05) * mm, "end": v(-43.51, 79.15) * mm});
            skLineSegment(sketch, "E743", {"start": v(-43.51, 79.15) * mm, "end": v(-43.48, 79.24) * mm});
            skLineSegment(sketch, "E744", {"start": v(-43.48, 79.24) * mm, "end": v(-43.44, 79.33) * mm});
            skLineSegment(sketch, "E745", {"start": v(-43.44, 79.33) * mm, "end": v(-43.4, 79.42) * mm});
            skLineSegment(sketch, "E746", {"start": v(-43.4, 79.42) * mm, "end": v(-43.36, 79.51) * mm});
            skLineSegment(sketch, "E747", {"start": v(-43.36, 79.51) * mm, "end": v(-43.31, 79.6) * mm});
            skLineSegment(sketch, "E748", {"start": v(-43.31, 79.6) * mm, "end": v(-43.26, 79.7) * mm});
            skLineSegment(sketch, "E749", {"start": v(-43.26, 79.7) * mm, "end": v(-43.21, 79.78) * mm});
            skLineSegment(sketch, "E750", {"start": v(-43.21, 79.78) * mm, "end": v(-43.16, 79.87) * mm});
            skLineSegment(sketch, "E751", {"start": v(-43.16, 79.87) * mm, "end": v(-43.1, 79.96) * mm});
            skLineSegment(sketch, "E752", {"start": v(-43.1, 79.96) * mm, "end": v(-43.05, 80.04) * mm});
            skLineSegment(sketch, "E753", {"start": v(-43.05, 80.04) * mm, "end": v(-42.99, 80.13) * mm});
            skLineSegment(sketch, "E754", {"start": v(-42.99, 80.13) * mm, "end": v(-42.93, 80.2) * mm});
            skLineSegment(sketch, "E755", {"start": v(-42.93, 80.2) * mm, "end": v(-42.86, 80.29) * mm});
            skLineSegment(sketch, "E756", {"start": v(-42.86, 80.29) * mm, "end": v(-42.8, 80.37) * mm});
            skLineSegment(sketch, "E757", {"start": v(-42.8, 80.37) * mm, "end": v(-42.73, 80.45) * mm});
            skLineSegment(sketch, "E758", {"start": v(-42.73, 80.45) * mm, "end": v(-42.66, 80.52) * mm});
            skLineSegment(sketch, "E759", {"start": v(-42.66, 80.52) * mm, "end": v(-42.59, 80.6) * mm});
            skLineSegment(sketch, "E760", {"start": v(-42.59, 80.6) * mm, "end": v(-42.51, 80.67) * mm});
            skLineSegment(sketch, "E761", {"start": v(-42.51, 80.67) * mm, "end": v(-42.44, 80.74) * mm});
            skLineSegment(sketch, "E762", {"start": v(-42.44, 80.74) * mm, "end": v(-42.36, 80.8) * mm});
            skLineSegment(sketch, "E763", {"start": v(-42.36, 80.8) * mm, "end": v(-42.28, 80.87) * mm});
            skLineSegment(sketch, "E764", {"start": v(-42.28, 80.87) * mm, "end": v(-42.2, 80.94) * mm});
            skLineSegment(sketch, "E765", {"start": v(-42.2, 80.94) * mm, "end": v(-42.12, 81) * mm});
            skLineSegment(sketch, "E766", {"start": v(-42.12, 81) * mm, "end": v(-42.03, 81.06) * mm});
            skLineSegment(sketch, "E767", {"start": v(-42.03, 81.06) * mm, "end": v(-41.95, 81.12) * mm});
            skLineSegment(sketch, "E768", {"start": v(-41.95, 81.12) * mm, "end": v(-41.86, 81.17) * mm});
            skLineSegment(sketch, "E769", {"start": v(-41.86, 81.17) * mm, "end": v(-41.77, 81.22) * mm});
            skLineSegment(sketch, "E770", {"start": v(-41.77, 81.22) * mm, "end": v(-41.68, 81.27) * mm});
            skLineSegment(sketch, "E771", {"start": v(-41.68, 81.27) * mm, "end": v(-41.6, 81.32) * mm});
            skLineSegment(sketch, "E772", {"start": v(-41.6, 81.32) * mm, "end": v(-41.5, 81.37) * mm});
            skLineSegment(sketch, "E773", {"start": v(-41.5, 81.37) * mm, "end": v(-41.41, 81.4) * mm});
            skLineSegment(sketch, "E774", {"start": v(-41.41, 81.4) * mm, "end": v(-41.32, 81.45) * mm});
            skLineSegment(sketch, "E775", {"start": v(-41.32, 81.45) * mm, "end": v(-41.23, 81.49) * mm});
            skLineSegment(sketch, "E776", {"start": v(-41.23, 81.49) * mm, "end": v(-41.14, 81.52) * mm});
            skLineSegment(sketch, "E777", {"start": v(-41.14, 81.52) * mm, "end": v(-41.04, 81.55) * mm});
            skLineSegment(sketch, "E778", {"start": v(-41.04, 81.55) * mm, "end": v(-40.95, 81.59) * mm});
            skLineSegment(sketch, "E779", {"start": v(-40.95, 81.59) * mm, "end": v(-40.86, 81.61) * mm});
            skLineSegment(sketch, "E780", {"start": v(-40.86, 81.61) * mm, "end": v(-40.76, 81.64) * mm});
            skLineSegment(sketch, "E781", {"start": v(-40.76, 81.64) * mm, "end": v(-40.67, 81.66) * mm});
            skLineSegment(sketch, "E782", {"start": v(-40.67, 81.66) * mm, "end": v(-40.58, 81.68) * mm});
            skLineSegment(sketch, "E783", {"start": v(-40.58, 81.68) * mm, "end": v(-40.49, 81.7) * mm});
            skLineSegment(sketch, "E784", {"start": v(-40.49, 81.7) * mm, "end": v(-40.4, 81.72) * mm});
            skLineSegment(sketch, "E785", {"start": v(-40.4, 81.72) * mm, "end": v(-40.3, 81.73) * mm});
            skLineSegment(sketch, "E786", {"start": v(-40.3, 81.73) * mm, "end": v(-40.2, 81.74) * mm});
            skLineSegment(sketch, "E787", {"start": v(-40.2, 81.74) * mm, "end": v(-40.12, 81.75) * mm});
            skLineSegment(sketch, "E788", {"start": v(-40.12, 81.75) * mm, "end": v(-40.03, 81.76) * mm});
            skLineSegment(sketch, "E789", {"start": v(-40.03, 81.76) * mm, "end": v(-39.94, 81.76) * mm});
            skLineSegment(sketch, "E790", {"start": v(-39.94, 81.76) * mm, "end": v(-39.85, 81.77) * mm});
            skLineSegment(sketch, "E791", {"start": v(-39.85, 81.77) * mm, "end": v(-39.76, 81.77) * mm});
            skLineSegment(sketch, "E792", {"start": v(19.72, 81.77) * mm, "end": v(19.81, 81.77) * mm});
            skLineSegment(sketch, "E793", {"start": v(19.81, 81.77) * mm, "end": v(19.9, 81.76) * mm});
            skLineSegment(sketch, "E794", {"start": v(19.9, 81.76) * mm, "end": v(20, 81.76) * mm});
            skLineSegment(sketch, "E795", {"start": v(20, 81.76) * mm, "end": v(20.08, 81.75) * mm});
            skLineSegment(sketch, "E796", {"start": v(20.08, 81.75) * mm, "end": v(20.17, 81.74) * mm});
            skLineSegment(sketch, "E797", {"start": v(20.17, 81.74) * mm, "end": v(20.27, 81.73) * mm});
            skLineSegment(sketch, "E798", {"start": v(20.27, 81.73) * mm, "end": v(20.36, 81.72) * mm});
            skLineSegment(sketch, "E799", {"start": v(20.36, 81.72) * mm, "end": v(20.45, 81.7) * mm});
            skLineSegment(sketch, "E800", {"start": v(20.45, 81.7) * mm, "end": v(20.54, 81.68) * mm});
            skLineSegment(sketch, "E801", {"start": v(20.54, 81.68) * mm, "end": v(20.64, 81.66) * mm});
            skLineSegment(sketch, "E802", {"start": v(20.64, 81.66) * mm, "end": v(20.73, 81.64) * mm});
            skLineSegment(sketch, "E803", {"start": v(20.73, 81.64) * mm, "end": v(20.82, 81.61) * mm});
            skLineSegment(sketch, "E804", {"start": v(20.82, 81.61) * mm, "end": v(20.92, 81.58) * mm});
            skLineSegment(sketch, "E805", {"start": v(20.92, 81.58) * mm, "end": v(21, 81.55) * mm});
            skLineSegment(sketch, "E806", {"start": v(21, 81.55) * mm, "end": v(21.1, 81.52) * mm});
            skLineSegment(sketch, "E807", {"start": v(21.1, 81.52) * mm, "end": v(21.2, 81.49) * mm});
            skLineSegment(sketch, "E808", {"start": v(21.2, 81.49) * mm, "end": v(21.29, 81.45) * mm});
            skLineSegment(sketch, "E809", {"start": v(21.29, 81.45) * mm, "end": v(21.38, 81.4) * mm});
            skLineSegment(sketch, "E810", {"start": v(21.38, 81.4) * mm, "end": v(21.47, 81.36) * mm});
            skLineSegment(sketch, "E811", {"start": v(21.47, 81.36) * mm, "end": v(21.56, 81.32) * mm});
            skLineSegment(sketch, "E812", {"start": v(21.56, 81.32) * mm, "end": v(21.65, 81.27) * mm});
            skLineSegment(sketch, "E813", {"start": v(21.65, 81.27) * mm, "end": v(21.74, 81.22) * mm});
            skLineSegment(sketch, "E814", {"start": v(21.74, 81.22) * mm, "end": v(21.82, 81.17) * mm});
            skLineSegment(sketch, "E815", {"start": v(21.82, 81.17) * mm, "end": v(21.91, 81.11) * mm});
            skLineSegment(sketch, "E816", {"start": v(21.91, 81.11) * mm, "end": v(22, 81.06) * mm});
            skLineSegment(sketch, "E817", {"start": v(22, 81.06) * mm, "end": v(22.08, 81) * mm});
            skLineSegment(sketch, "E818", {"start": v(22.08, 81) * mm, "end": v(22.16, 80.94) * mm});
            skLineSegment(sketch, "E819", {"start": v(22.16, 80.94) * mm, "end": v(22.24, 80.87) * mm});
            skLineSegment(sketch, "E820", {"start": v(22.24, 80.87) * mm, "end": v(22.32, 80.8) * mm});
            skLineSegment(sketch, "E821", {"start": v(22.32, 80.8) * mm, "end": v(22.4, 80.74) * mm});
            skLineSegment(sketch, "E822", {"start": v(22.4, 80.74) * mm, "end": v(22.48, 80.67) * mm});
            skLineSegment(sketch, "E823", {"start": v(22.48, 80.67) * mm, "end": v(22.55, 80.6) * mm});
            skLineSegment(sketch, "E824", {"start": v(22.55, 80.6) * mm, "end": v(22.62, 80.52) * mm});
            skLineSegment(sketch, "E825", {"start": v(22.62, 80.52) * mm, "end": v(22.7, 80.45) * mm});
            skLineSegment(sketch, "E826", {"start": v(22.7, 80.45) * mm, "end": v(22.76, 80.37) * mm});
            skLineSegment(sketch, "E827", {"start": v(22.76, 80.37) * mm, "end": v(22.83, 80.29) * mm});
            skLineSegment(sketch, "E828", {"start": v(22.83, 80.29) * mm, "end": v(22.9, 80.2) * mm});
            skLineSegment(sketch, "E829", {"start": v(22.9, 80.2) * mm, "end": v(22.95, 80.12) * mm});
            skLineSegment(sketch, "E830", {"start": v(22.95, 80.12) * mm, "end": v(23.01, 80.04) * mm});
            skLineSegment(sketch, "E831", {"start": v(23.01, 80.04) * mm, "end": v(23.07, 79.96) * mm});
            skLineSegment(sketch, "E832", {"start": v(23.07, 79.96) * mm, "end": v(23.12, 79.87) * mm});
            skLineSegment(sketch, "E833", {"start": v(23.12, 79.87) * mm, "end": v(23.18, 79.78) * mm});
            skLineSegment(sketch, "E834", {"start": v(23.18, 79.78) * mm, "end": v(23.23, 79.7) * mm});
            skLineSegment(sketch, "E835", {"start": v(23.23, 79.7) * mm, "end": v(23.27, 79.6) * mm});
            skLineSegment(sketch, "E836", {"start": v(23.27, 79.6) * mm, "end": v(23.32, 79.51) * mm});
            skLineSegment(sketch, "E837", {"start": v(23.32, 79.51) * mm, "end": v(23.36, 79.42) * mm});
            skLineSegment(sketch, "E838", {"start": v(23.36, 79.42) * mm, "end": v(23.4, 79.33) * mm});
            skLineSegment(sketch, "E839", {"start": v(23.4, 79.33) * mm, "end": v(23.44, 79.24) * mm});
            skLineSegment(sketch, "E840", {"start": v(23.44, 79.24) * mm, "end": v(23.48, 79.15) * mm});
            skLineSegment(sketch, "E841", {"start": v(23.48, 79.15) * mm, "end": v(23.5, 79.05) * mm});
            skLineSegment(sketch, "E842", {"start": v(23.5, 79.05) * mm, "end": v(23.54, 78.96) * mm});
            skLineSegment(sketch, "E843", {"start": v(23.54, 78.96) * mm, "end": v(23.57, 78.87) * mm});
            skLineSegment(sketch, "E844", {"start": v(23.57, 78.87) * mm, "end": v(23.6, 78.77) * mm});
            skLineSegment(sketch, "E845", {"start": v(23.6, 78.77) * mm, "end": v(23.62, 78.68) * mm});
            skLineSegment(sketch, "E846", {"start": v(23.62, 78.68) * mm, "end": v(23.64, 78.59) * mm});
            skLineSegment(sketch, "E847", {"start": v(23.64, 78.59) * mm, "end": v(23.65, 78.5) * mm});
            skLineSegment(sketch, "E848", {"start": v(23.65, 78.5) * mm, "end": v(23.67, 78.4) * mm});
            skLineSegment(sketch, "E849", {"start": v(23.67, 78.4) * mm, "end": v(23.68, 78.31) * mm});
            skLineSegment(sketch, "E850", {"start": v(23.68, 78.31) * mm, "end": v(23.7, 78.22) * mm});
            skLineSegment(sketch, "E851", {"start": v(23.7, 78.22) * mm, "end": v(23.7, 78.13) * mm});
            skLineSegment(sketch, "E852", {"start": v(23.7, 78.13) * mm, "end": v(23.71, 78.04) * mm});
            skLineSegment(sketch, "E853", {"start": v(23.71, 78.04) * mm, "end": v(23.72, 77.95) * mm});
            skLineSegment(sketch, "E854", {"start": v(23.72, 77.95) * mm, "end": v(23.72, 77.86) * mm});
            skLineSegment(sketch, "E855", {"start": v(23.72, 77.86) * mm, "end": v(23.72, 77.77) * mm});
            skLineSegment(sketch, "E856", {"start": v(23.72, 77.77) * mm, "end": v(23.72, 77.68) * mm});
            skLineSegment(sketch, "E857", {"start": v(23.72, 77.68) * mm, "end": v(23.72, 77.59) * mm});
            skLineSegment(sketch, "E858", {"start": v(23.72, 77.59) * mm, "end": v(23.71, 77.5) * mm});
            skLineSegment(sketch, "E859", {"start": v(23.71, 77.5) * mm, "end": v(23.7, 77.4) * mm});
            skLineSegment(sketch, "E860", {"start": v(23.7, 77.4) * mm, "end": v(23.7, 77.32) * mm});
            skLineSegment(sketch, "E861", {"start": v(23.7, 77.32) * mm, "end": v(23.68, 77.22) * mm});
            skLineSegment(sketch, "E862", {"start": v(23.68, 77.22) * mm, "end": v(23.67, 77.13) * mm});
            skLineSegment(sketch, "E863", {"start": v(23.67, 77.13) * mm, "end": v(23.65, 77.04) * mm});
            skLineSegment(sketch, "E864", {"start": v(23.65, 77.04) * mm, "end": v(23.64, 76.95) * mm});
            skLineSegment(sketch, "E865", {"start": v(23.64, 76.95) * mm, "end": v(23.62, 76.85) * mm});
            skLineSegment(sketch, "E866", {"start": v(23.62, 76.85) * mm, "end": v(23.6, 76.76) * mm});
            skLineSegment(sketch, "E867", {"start": v(23.6, 76.76) * mm, "end": v(23.57, 76.67) * mm});
            skLineSegment(sketch, "E868", {"start": v(23.57, 76.67) * mm, "end": v(23.54, 76.57) * mm});
            skLineSegment(sketch, "E869", {"start": v(23.54, 76.57) * mm, "end": v(23.5, 76.48) * mm});
            skLineSegment(sketch, "E870", {"start": v(23.5, 76.48) * mm, "end": v(23.48, 76.39) * mm});
            skLineSegment(sketch, "E871", {"start": v(23.48, 76.39) * mm, "end": v(23.44, 76.3) * mm});
            skLineSegment(sketch, "E872", {"start": v(23.44, 76.3) * mm, "end": v(23.4, 76.2) * mm});
            skLineSegment(sketch, "E873", {"start": v(23.4, 76.2) * mm, "end": v(23.36, 76.11) * mm});
            skLineSegment(sketch, "E874", {"start": v(23.36, 76.11) * mm, "end": v(23.32, 76.02) * mm});
            skLineSegment(sketch, "E875", {"start": v(23.32, 76.02) * mm, "end": v(23.27, 75.93) * mm});
            skLineSegment(sketch, "E876", {"start": v(23.27, 75.93) * mm, "end": v(23.23, 75.84) * mm});
            skLineSegment(sketch, "E877", {"start": v(23.23, 75.84) * mm, "end": v(23.18, 75.75) * mm});
            skLineSegment(sketch, "E878", {"start": v(23.18, 75.75) * mm, "end": v(23.12, 75.67) * mm});
            skLineSegment(sketch, "E879", {"start": v(23.12, 75.67) * mm, "end": v(23.07, 75.58) * mm});
            skLineSegment(sketch, "E880", {"start": v(23.07, 75.58) * mm, "end": v(23.01, 75.5) * mm});
            skLineSegment(sketch, "E881", {"start": v(23.01, 75.5) * mm, "end": v(22.95, 75.41) * mm});
            skLineSegment(sketch, "E882", {"start": v(22.95, 75.41) * mm, "end": v(22.9, 75.33) * mm});
            skLineSegment(sketch, "E883", {"start": v(22.9, 75.33) * mm, "end": v(22.83, 75.25) * mm});
            skLineSegment(sketch, "E884", {"start": v(22.83, 75.25) * mm, "end": v(22.76, 75.17) * mm});
            skLineSegment(sketch, "E885", {"start": v(22.76, 75.17) * mm, "end": v(22.7, 75.09) * mm});
            skLineSegment(sketch, "E886", {"start": v(22.7, 75.09) * mm, "end": v(22.62, 75.01) * mm});
            skLineSegment(sketch, "E887", {"start": v(22.62, 75.01) * mm, "end": v(22.55, 74.94) * mm});
            skLineSegment(sketch, "E888", {"start": v(22.55, 74.94) * mm, "end": v(22.48, 74.87) * mm});
            skLineSegment(sketch, "E889", {"start": v(22.48, 74.87) * mm, "end": v(22.4, 74.8) * mm});
            skLineSegment(sketch, "E890", {"start": v(22.4, 74.8) * mm, "end": v(22.32, 74.73) * mm});
            skLineSegment(sketch, "E891", {"start": v(22.32, 74.73) * mm, "end": v(22.24, 74.66) * mm});
            skLineSegment(sketch, "E892", {"start": v(22.24, 74.66) * mm, "end": v(22.16, 74.6) * mm});
            skLineSegment(sketch, "E893", {"start": v(22.16, 74.6) * mm, "end": v(22.08, 74.54) * mm});
            skLineSegment(sketch, "E894", {"start": v(22.08, 74.54) * mm, "end": v(22, 74.48) * mm});
            skLineSegment(sketch, "E895", {"start": v(22, 74.48) * mm, "end": v(21.91, 74.42) * mm});
            skLineSegment(sketch, "E896", {"start": v(21.91, 74.42) * mm, "end": v(21.82, 74.37) * mm});
            skLineSegment(sketch, "E897", {"start": v(21.82, 74.37) * mm, "end": v(21.74, 74.31) * mm});
            skLineSegment(sketch, "E898", {"start": v(21.74, 74.31) * mm, "end": v(21.65, 74.26) * mm});
            skLineSegment(sketch, "E899", {"start": v(21.65, 74.26) * mm, "end": v(21.56, 74.22) * mm});
            skLineSegment(sketch, "E900", {"start": v(21.56, 74.22) * mm, "end": v(21.47, 74.17) * mm});
            skLineSegment(sketch, "E901", {"start": v(21.47, 74.17) * mm, "end": v(21.38, 74.13) * mm});
            skLineSegment(sketch, "E902", {"start": v(21.38, 74.13) * mm, "end": v(21.29, 74.09) * mm});
            skLineSegment(sketch, "E903", {"start": v(21.29, 74.09) * mm, "end": v(21.2, 74.05) * mm});
            skLineSegment(sketch, "E904", {"start": v(21.2, 74.05) * mm, "end": v(21.1, 74.01) * mm});
            skLineSegment(sketch, "E905", {"start": v(21.1, 74.01) * mm, "end": v(21, 73.98) * mm});
            skLineSegment(sketch, "E906", {"start": v(21, 73.98) * mm, "end": v(20.92, 73.95) * mm});
            skLineSegment(sketch, "E907", {"start": v(20.92, 73.95) * mm, "end": v(20.82, 73.92) * mm});
            skLineSegment(sketch, "E908", {"start": v(20.82, 73.92) * mm, "end": v(20.73, 73.9) * mm});
            skLineSegment(sketch, "E909", {"start": v(20.73, 73.9) * mm, "end": v(20.64, 73.87) * mm});
            skLineSegment(sketch, "E910", {"start": v(20.64, 73.87) * mm, "end": v(20.54, 73.85) * mm});
            skLineSegment(sketch, "E911", {"start": v(20.54, 73.85) * mm, "end": v(20.45, 73.84) * mm});
            skLineSegment(sketch, "E912", {"start": v(20.45, 73.84) * mm, "end": v(20.36, 73.82) * mm});
            skLineSegment(sketch, "E913", {"start": v(20.36, 73.82) * mm, "end": v(20.27, 73.8) * mm});
            skLineSegment(sketch, "E914", {"start": v(20.27, 73.8) * mm, "end": v(20.17, 73.8) * mm});
            skLineSegment(sketch, "E915", {"start": v(20.17, 73.8) * mm, "end": v(20.08, 73.78) * mm});
            skLineSegment(sketch, "E916", {"start": v(20.08, 73.78) * mm, "end": v(20, 73.78) * mm});
            skLineSegment(sketch, "E917", {"start": v(20, 73.78) * mm, "end": v(19.9, 73.77) * mm});
            skLineSegment(sketch, "E918", {"start": v(19.9, 73.77) * mm, "end": v(19.81, 73.77) * mm});
            skLineSegment(sketch, "E919", {"start": v(19.81, 73.77) * mm, "end": v(19.72, 73.77) * mm});
            skLineSegment(sketch, "E920", {"start": v(19.72, 73.77) * mm, "end": v(19.63, 73.77) * mm});
            skLineSegment(sketch, "E921", {"start": v(19.63, 73.77) * mm, "end": v(19.54, 73.77) * mm});
            skLineSegment(sketch, "E922", {"start": v(19.54, 73.77) * mm, "end": v(19.45, 73.78) * mm});
            skLineSegment(sketch, "E923", {"start": v(19.45, 73.78) * mm, "end": v(19.36, 73.78) * mm});
            skLineSegment(sketch, "E924", {"start": v(19.36, 73.78) * mm, "end": v(19.27, 73.8) * mm});
            skLineSegment(sketch, "E925", {"start": v(19.27, 73.8) * mm, "end": v(19.18, 73.8) * mm});
            skLineSegment(sketch, "E926", {"start": v(19.18, 73.8) * mm, "end": v(19.09, 73.82) * mm});
            skLineSegment(sketch, "E927", {"start": v(19.09, 73.82) * mm, "end": v(19, 73.84) * mm});
            skLineSegment(sketch, "E928", {"start": v(19, 73.84) * mm, "end": v(18.9, 73.85) * mm});
            skLineSegment(sketch, "E929", {"start": v(18.9, 73.85) * mm, "end": v(18.8, 73.87) * mm});
            skLineSegment(sketch, "E930", {"start": v(18.8, 73.87) * mm, "end": v(18.72, 73.9) * mm});
            skLineSegment(sketch, "E931", {"start": v(18.72, 73.9) * mm, "end": v(18.62, 73.92) * mm});
            skLineSegment(sketch, "E932", {"start": v(18.62, 73.92) * mm, "end": v(18.53, 73.95) * mm});
            skLineSegment(sketch, "E933", {"start": v(18.53, 73.95) * mm, "end": v(18.44, 73.98) * mm});
            skLineSegment(sketch, "E934", {"start": v(18.44, 73.98) * mm, "end": v(18.34, 74.01) * mm});
            skLineSegment(sketch, "E935", {"start": v(18.34, 74.01) * mm, "end": v(18.25, 74.05) * mm});
            skLineSegment(sketch, "E936", {"start": v(18.25, 74.05) * mm, "end": v(18.16, 74.09) * mm});
            skLineSegment(sketch, "E937", {"start": v(18.16, 74.09) * mm, "end": v(18.07, 74.13) * mm});
            skLineSegment(sketch, "E938", {"start": v(18.07, 74.13) * mm, "end": v(17.98, 74.17) * mm});
            skLineSegment(sketch, "E939", {"start": v(17.98, 74.17) * mm, "end": v(17.89, 74.22) * mm});
            skLineSegment(sketch, "E940", {"start": v(17.89, 74.22) * mm, "end": v(17.8, 74.26) * mm});
            skLineSegment(sketch, "E941", {"start": v(17.8, 74.26) * mm, "end": v(17.7, 74.31) * mm});
            skLineSegment(sketch, "E942", {"start": v(17.7, 74.31) * mm, "end": v(17.62, 74.37) * mm});
            skLineSegment(sketch, "E943", {"start": v(17.62, 74.37) * mm, "end": v(17.53, 74.42) * mm});
            skLineSegment(sketch, "E944", {"start": v(17.53, 74.42) * mm, "end": v(17.45, 74.48) * mm});
            skLineSegment(sketch, "E945", {"start": v(17.45, 74.48) * mm, "end": v(17.37, 74.54) * mm});
            skLineSegment(sketch, "E946", {"start": v(17.37, 74.54) * mm, "end": v(17.28, 74.6) * mm});
            skLineSegment(sketch, "E947", {"start": v(17.28, 74.6) * mm, "end": v(17.2, 74.66) * mm});
            skLineSegment(sketch, "E948", {"start": v(17.2, 74.66) * mm, "end": v(17.12, 74.73) * mm});
            skLineSegment(sketch, "E949", {"start": v(17.12, 74.73) * mm, "end": v(17.04, 74.8) * mm});
            skLineSegment(sketch, "E950", {"start": v(17.04, 74.8) * mm, "end": v(16.97, 74.87) * mm});
            skLineSegment(sketch, "E951", {"start": v(16.97, 74.87) * mm, "end": v(16.9, 74.94) * mm});
            skLineSegment(sketch, "E952", {"start": v(16.9, 74.94) * mm, "end": v(16.82, 75.01) * mm});
            skLineSegment(sketch, "E953", {"start": v(16.82, 75.01) * mm, "end": v(16.75, 75.09) * mm});
            skLineSegment(sketch, "E954", {"start": v(16.75, 75.09) * mm, "end": v(16.68, 75.17) * mm});
            skLineSegment(sketch, "E955", {"start": v(16.68, 75.17) * mm, "end": v(16.62, 75.25) * mm});
            skLineSegment(sketch, "E956", {"start": v(16.62, 75.25) * mm, "end": v(16.55, 75.33) * mm});
            skLineSegment(sketch, "E957", {"start": v(16.55, 75.33) * mm, "end": v(16.5, 75.41) * mm});
            skLineSegment(sketch, "E958", {"start": v(16.5, 75.41) * mm, "end": v(16.43, 75.5) * mm});
            skLineSegment(sketch, "E959", {"start": v(16.43, 75.5) * mm, "end": v(16.38, 75.58) * mm});
            skLineSegment(sketch, "E960", {"start": v(16.38, 75.58) * mm, "end": v(16.32, 75.67) * mm});
            skLineSegment(sketch, "E961", {"start": v(16.32, 75.67) * mm, "end": v(16.27, 75.75) * mm});
            skLineSegment(sketch, "E962", {"start": v(16.27, 75.75) * mm, "end": v(16.22, 75.84) * mm});
            skLineSegment(sketch, "E963", {"start": v(16.22, 75.84) * mm, "end": v(16.17, 75.93) * mm});
            skLineSegment(sketch, "E964", {"start": v(16.17, 75.93) * mm, "end": v(16.12, 76.02) * mm});
            skLineSegment(sketch, "E965", {"start": v(16.12, 76.02) * mm, "end": v(16.08, 76.11) * mm});
            skLineSegment(sketch, "E966", {"start": v(16.08, 76.11) * mm, "end": v(16.04, 76.2) * mm});
            skLineSegment(sketch, "E967", {"start": v(16.04, 76.2) * mm, "end": v(16, 76.3) * mm});
            skLineSegment(sketch, "E968", {"start": v(16, 76.3) * mm, "end": v(15.97, 76.39) * mm});
            skLineSegment(sketch, "E969", {"start": v(15.97, 76.39) * mm, "end": v(15.94, 76.48) * mm});
            skLineSegment(sketch, "E970", {"start": v(15.94, 76.48) * mm, "end": v(15.9, 76.57) * mm});
            skLineSegment(sketch, "E971", {"start": v(15.9, 76.57) * mm, "end": v(15.88, 76.67) * mm});
            skLineSegment(sketch, "E972", {"start": v(15.88, 76.67) * mm, "end": v(15.85, 76.76) * mm});
            skLineSegment(sketch, "E973", {"start": v(15.85, 76.76) * mm, "end": v(15.83, 76.85) * mm});
            skLineSegment(sketch, "E974", {"start": v(15.83, 76.85) * mm, "end": v(15.8, 76.95) * mm});
            skLineSegment(sketch, "E975", {"start": v(15.8, 76.95) * mm, "end": v(15.8, 77.04) * mm});
            skLineSegment(sketch, "E976", {"start": v(15.8, 77.04) * mm, "end": v(15.77, 77.13) * mm});
            skLineSegment(sketch, "E977", {"start": v(15.77, 77.13) * mm, "end": v(15.76, 77.22) * mm});
            skLineSegment(sketch, "E978", {"start": v(15.76, 77.22) * mm, "end": v(15.75, 77.32) * mm});
            skLineSegment(sketch, "E979", {"start": v(15.75, 77.32) * mm, "end": v(15.74, 77.4) * mm});
            skLineSegment(sketch, "E980", {"start": v(15.74, 77.4) * mm, "end": v(15.73, 77.5) * mm});
            skLineSegment(sketch, "E981", {"start": v(15.73, 77.5) * mm, "end": v(15.73, 77.59) * mm});
            skLineSegment(sketch, "E982", {"start": v(15.73, 77.59) * mm, "end": v(15.72, 77.68) * mm});
            skLineSegment(sketch, "E983", {"start": v(15.72, 77.68) * mm, "end": v(15.72, 77.77) * mm});
            skLineSegment(sketch, "E984", {"start": v(15.72, 77.77) * mm, "end": v(15.72, 77.86) * mm});
            skLineSegment(sketch, "E985", {"start": v(15.72, 77.86) * mm, "end": v(15.73, 77.95) * mm});
            skLineSegment(sketch, "E986", {"start": v(15.73, 77.95) * mm, "end": v(15.73, 78.04) * mm});
            skLineSegment(sketch, "E987", {"start": v(15.73, 78.04) * mm, "end": v(15.74, 78.13) * mm});
            skLineSegment(sketch, "E988", {"start": v(15.74, 78.13) * mm, "end": v(15.75, 78.22) * mm});
            skLineSegment(sketch, "E989", {"start": v(15.75, 78.22) * mm, "end": v(15.76, 78.31) * mm});
            skLineSegment(sketch, "E990", {"start": v(15.76, 78.31) * mm, "end": v(15.77, 78.4) * mm});
            skLineSegment(sketch, "E991", {"start": v(15.77, 78.4) * mm, "end": v(15.8, 78.5) * mm});
            skLineSegment(sketch, "E992", {"start": v(15.8, 78.5) * mm, "end": v(15.8, 78.59) * mm});
            skLineSegment(sketch, "E993", {"start": v(15.8, 78.59) * mm, "end": v(15.83, 78.68) * mm});
            skLineSegment(sketch, "E994", {"start": v(15.83, 78.68) * mm, "end": v(15.85, 78.77) * mm});
            skLineSegment(sketch, "E995", {"start": v(15.85, 78.77) * mm, "end": v(15.88, 78.87) * mm});
            skLineSegment(sketch, "E996", {"start": v(15.88, 78.87) * mm, "end": v(15.9, 78.96) * mm});
            skLineSegment(sketch, "E997", {"start": v(15.9, 78.96) * mm, "end": v(15.94, 79.05) * mm});
            skLineSegment(sketch, "E998", {"start": v(15.94, 79.05) * mm, "end": v(15.97, 79.15) * mm});
            skLineSegment(sketch, "E999", {"start": v(15.97, 79.15) * mm, "end": v(16, 79.24) * mm});
            skLineSegment(sketch, "E1000", {"start": v(16, 79.24) * mm, "end": v(16.04, 79.33) * mm});
            skLineSegment(sketch, "E1001", {"start": v(16.04, 79.33) * mm, "end": v(16.08, 79.42) * mm});
            skLineSegment(sketch, "E1002", {"start": v(16.08, 79.42) * mm, "end": v(16.12, 79.51) * mm});
            skLineSegment(sketch, "E1003", {"start": v(16.12, 79.51) * mm, "end": v(16.17, 79.6) * mm});
            skLineSegment(sketch, "E1004", {"start": v(16.17, 79.6) * mm, "end": v(16.22, 79.7) * mm});
            skLineSegment(sketch, "E1005", {"start": v(16.22, 79.7) * mm, "end": v(16.27, 79.78) * mm});
            skLineSegment(sketch, "E1006", {"start": v(16.27, 79.78) * mm, "end": v(16.32, 79.87) * mm});
            skLineSegment(sketch, "E1007", {"start": v(16.32, 79.87) * mm, "end": v(16.38, 79.96) * mm});
            skLineSegment(sketch, "E1008", {"start": v(16.38, 79.96) * mm, "end": v(16.43, 80.04) * mm});
            skLineSegment(sketch, "E1009", {"start": v(16.43, 80.04) * mm, "end": v(16.5, 80.12) * mm});
            skLineSegment(sketch, "E1010", {"start": v(16.5, 80.12) * mm, "end": v(16.55, 80.2) * mm});
            skLineSegment(sketch, "E1011", {"start": v(16.55, 80.2) * mm, "end": v(16.62, 80.29) * mm});
            skLineSegment(sketch, "E1012", {"start": v(16.62, 80.29) * mm, "end": v(16.68, 80.37) * mm});
            skLineSegment(sketch, "E1013", {"start": v(16.68, 80.37) * mm, "end": v(16.75, 80.45) * mm});
            skLineSegment(sketch, "E1014", {"start": v(16.75, 80.45) * mm, "end": v(16.82, 80.52) * mm});
            skLineSegment(sketch, "E1015", {"start": v(16.82, 80.52) * mm, "end": v(16.9, 80.6) * mm});
            skLineSegment(sketch, "E1016", {"start": v(16.9, 80.6) * mm, "end": v(16.97, 80.67) * mm});
            skLineSegment(sketch, "E1017", {"start": v(16.97, 80.67) * mm, "end": v(17.04, 80.74) * mm});
            skLineSegment(sketch, "E1018", {"start": v(17.04, 80.74) * mm, "end": v(17.12, 80.8) * mm});
            skLineSegment(sketch, "E1019", {"start": v(17.12, 80.8) * mm, "end": v(17.2, 80.87) * mm});
            skLineSegment(sketch, "E1020", {"start": v(17.2, 80.87) * mm, "end": v(17.28, 80.94) * mm});
            skLineSegment(sketch, "E1021", {"start": v(17.28, 80.94) * mm, "end": v(17.37, 81) * mm});
            skLineSegment(sketch, "E1022", {"start": v(17.37, 81) * mm, "end": v(17.45, 81.06) * mm});
            skLineSegment(sketch, "E1023", {"start": v(17.45, 81.06) * mm, "end": v(17.53, 81.11) * mm});
            skLineSegment(sketch, "E1024", {"start": v(17.53, 81.11) * mm, "end": v(17.62, 81.17) * mm});
            skLineSegment(sketch, "E1025", {"start": v(17.62, 81.17) * mm, "end": v(17.7, 81.22) * mm});
            skLineSegment(sketch, "E1026", {"start": v(17.7, 81.22) * mm, "end": v(17.8, 81.27) * mm});
            skLineSegment(sketch, "E1027", {"start": v(17.8, 81.27) * mm, "end": v(17.89, 81.32) * mm});
            skLineSegment(sketch, "E1028", {"start": v(17.89, 81.32) * mm, "end": v(17.98, 81.36) * mm});
            skLineSegment(sketch, "E1029", {"start": v(17.98, 81.36) * mm, "end": v(18.07, 81.4) * mm});
            skLineSegment(sketch, "E1030", {"start": v(18.07, 81.4) * mm, "end": v(18.16, 81.45) * mm});
            skLineSegment(sketch, "E1031", {"start": v(18.16, 81.45) * mm, "end": v(18.25, 81.49) * mm});
            skLineSegment(sketch, "E1032", {"start": v(18.25, 81.49) * mm, "end": v(18.34, 81.52) * mm});
            skLineSegment(sketch, "E1033", {"start": v(18.34, 81.52) * mm, "end": v(18.44, 81.55) * mm});
            skLineSegment(sketch, "E1034", {"start": v(18.44, 81.55) * mm, "end": v(18.53, 81.58) * mm});
            skLineSegment(sketch, "E1035", {"start": v(18.53, 81.58) * mm, "end": v(18.62, 81.61) * mm});
            skLineSegment(sketch, "E1036", {"start": v(18.62, 81.61) * mm, "end": v(18.72, 81.64) * mm});
            skLineSegment(sketch, "E1037", {"start": v(18.72, 81.64) * mm, "end": v(18.8, 81.66) * mm});
            skLineSegment(sketch, "E1038", {"start": v(18.8, 81.66) * mm, "end": v(18.9, 81.68) * mm});
            skLineSegment(sketch, "E1039", {"start": v(18.9, 81.68) * mm, "end": v(19, 81.7) * mm});
            skLineSegment(sketch, "E1040", {"start": v(19, 81.7) * mm, "end": v(19.09, 81.72) * mm});
            skLineSegment(sketch, "E1041", {"start": v(19.09, 81.72) * mm, "end": v(19.18, 81.73) * mm});
            skLineSegment(sketch, "E1042", {"start": v(19.18, 81.73) * mm, "end": v(19.27, 81.74) * mm});
            skLineSegment(sketch, "E1043", {"start": v(19.27, 81.74) * mm, "end": v(19.36, 81.75) * mm});
            skLineSegment(sketch, "E1044", {"start": v(19.36, 81.75) * mm, "end": v(19.45, 81.76) * mm});
            skLineSegment(sketch, "E1045", {"start": v(19.45, 81.76) * mm, "end": v(19.54, 81.76) * mm});
            skLineSegment(sketch, "E1046", {"start": v(19.54, 81.76) * mm, "end": v(19.63, 81.77) * mm});
            skLineSegment(sketch, "E1047", {"start": v(19.63, 81.77) * mm, "end": v(19.72, 81.77) * mm});
            skLineSegment(sketch, "E1048", {"start": v(-2.44, 67.77) * mm, "end": v(-1.21, 67.76) * mm});
            skLineSegment(sketch, "E1049", {"start": v(-1.21, 67.76) * mm, "end": v(0.02, 67.71) * mm});
            skLineSegment(sketch, "E1050", {"start": v(0.02, 67.71) * mm, "end": v(1.26, 67.64) * mm});
            skLineSegment(sketch, "E1051", {"start": v(1.26, 67.64) * mm, "end": v(2.5, 67.55) * mm});
            skLineSegment(sketch, "E1052", {"start": v(2.5, 67.55) * mm, "end": v(3.76, 67.42) * mm});
            skLineSegment(sketch, "E1053", {"start": v(3.76, 67.42) * mm, "end": v(5.03, 67.26) * mm});
            skLineSegment(sketch, "E1054", {"start": v(5.03, 67.26) * mm, "end": v(6.3, 67.07) * mm});
            skLineSegment(sketch, "E1055", {"start": v(6.3, 67.07) * mm, "end": v(7.57, 66.85) * mm});
            skLineSegment(sketch, "E1056", {"start": v(7.57, 66.85) * mm, "end": v(8.85, 66.6) * mm});
            skLineSegment(sketch, "E1057", {"start": v(8.85, 66.6) * mm, "end": v(10.13, 66.31) * mm});
            skLineSegment(sketch, "E1058", {"start": v(10.13, 66.31) * mm, "end": v(11.41, 66) * mm});
            skLineSegment(sketch, "E1059", {"start": v(11.41, 66) * mm, "end": v(12.7, 65.65) * mm});
            skLineSegment(sketch, "E1060", {"start": v(12.7, 65.65) * mm, "end": v(13.98, 65.26) * mm});
            skLineSegment(sketch, "E1061", {"start": v(13.98, 65.26) * mm, "end": v(15.26, 64.84) * mm});
            skLineSegment(sketch, "E1062", {"start": v(15.26, 64.84) * mm, "end": v(16.54, 64.4) * mm});
            skLineSegment(sketch, "E1063", {"start": v(16.54, 64.4) * mm, "end": v(17.8, 63.9) * mm});
            skLineSegment(sketch, "E1064", {"start": v(17.8, 63.9) * mm, "end": v(19.08, 63.39) * mm});
            skLineSegment(sketch, "E1065", {"start": v(19.08, 63.39) * mm, "end": v(20.33, 62.83) * mm});
            skLineSegment(sketch, "E1066", {"start": v(20.33, 62.83) * mm, "end": v(21.59, 62.25) * mm});
            skLineSegment(sketch, "E1067", {"start": v(21.59, 62.25) * mm, "end": v(22.83, 61.62) * mm});
            skLineSegment(sketch, "E1068", {"start": v(22.83, 61.62) * mm, "end": v(24.05, 60.97) * mm});
            skLineSegment(sketch, "E1069", {"start": v(24.05, 60.97) * mm, "end": v(25.27, 60.28) * mm});
            skLineSegment(sketch, "E1070", {"start": v(25.27, 60.28) * mm, "end": v(26.47, 59.56) * mm});
            skLineSegment(sketch, "E1071", {"start": v(26.47, 59.56) * mm, "end": v(27.66, 58.8) * mm});
            skLineSegment(sketch, "E1072", {"start": v(27.66, 58.8) * mm, "end": v(28.83, 58.02) * mm});
            skLineSegment(sketch, "E1073", {"start": v(28.83, 58.02) * mm, "end": v(29.98, 57.2) * mm});
            skLineSegment(sketch, "E1074", {"start": v(29.98, 57.2) * mm, "end": v(31.12, 56.35) * mm});
            skLineSegment(sketch, "E1075", {"start": v(31.12, 56.35) * mm, "end": v(32.23, 55.47) * mm});
            skLineSegment(sketch, "E1076", {"start": v(32.23, 55.47) * mm, "end": v(33.32, 54.56) * mm});
            skLineSegment(sketch, "E1077", {"start": v(33.32, 54.56) * mm, "end": v(34.4, 53.62) * mm});
            skLineSegment(sketch, "E1078", {"start": v(34.4, 53.62) * mm, "end": v(35.44, 52.65) * mm});
            skLineSegment(sketch, "E1079", {"start": v(35.44, 52.65) * mm, "end": v(36.46, 51.66) * mm});
            skLineSegment(sketch, "E1080", {"start": v(36.46, 51.66) * mm, "end": v(37.45, 50.64) * mm});
            skLineSegment(sketch, "E1081", {"start": v(37.45, 50.64) * mm, "end": v(38.42, 49.6) * mm});
            skLineSegment(sketch, "E1082", {"start": v(38.42, 49.6) * mm, "end": v(39.35, 48.53) * mm});
            skLineSegment(sketch, "E1083", {"start": v(39.35, 48.53) * mm, "end": v(40.26, 47.44) * mm});
            skLineSegment(sketch, "E1084", {"start": v(40.26, 47.44) * mm, "end": v(41.14, 46.32) * mm});
            skLineSegment(sketch, "E1085", {"start": v(41.14, 46.32) * mm, "end": v(42, 45.19) * mm});
            skLineSegment(sketch, "E1086", {"start": v(42, 45.19) * mm, "end": v(42.81, 44.04) * mm});
            skLineSegment(sketch, "E1087", {"start": v(42.81, 44.04) * mm, "end": v(43.6, 42.87) * mm});
            skLineSegment(sketch, "E1088", {"start": v(43.6, 42.87) * mm, "end": v(44.35, 41.68) * mm});
            skLineSegment(sketch, "E1089", {"start": v(44.35, 41.68) * mm, "end": v(45.08, 40.48) * mm});
            skLineSegment(sketch, "E1090", {"start": v(45.08, 40.48) * mm, "end": v(45.76, 39.26) * mm});
            skLineSegment(sketch, "E1091", {"start": v(45.76, 39.26) * mm, "end": v(46.42, 38.03) * mm});
            skLineSegment(sketch, "E1092", {"start": v(46.42, 38.03) * mm, "end": v(47.04, 36.79) * mm});
            skLineSegment(sketch, "E1093", {"start": v(47.04, 36.79) * mm, "end": v(47.63, 35.54) * mm});
            skLineSegment(sketch, "E1094", {"start": v(47.63, 35.54) * mm, "end": v(48.18, 34.28) * mm});
            skLineSegment(sketch, "E1095", {"start": v(48.18, 34.28) * mm, "end": v(48.7, 33.01) * mm});
            skLineSegment(sketch, "E1096", {"start": v(48.7, 33.01) * mm, "end": v(49.19, 31.74) * mm});
            skLineSegment(sketch, "E1097", {"start": v(49.19, 31.74) * mm, "end": v(49.64, 30.46) * mm});
            skLineSegment(sketch, "E1098", {"start": v(49.64, 30.46) * mm, "end": v(50.06, 29.18) * mm});
            skLineSegment(sketch, "E1099", {"start": v(50.06, 29.18) * mm, "end": v(50.44, 27.9) * mm});
            skLineSegment(sketch, "E1100", {"start": v(50.44, 27.9) * mm, "end": v(50.8, 26.62) * mm});
            skLineSegment(sketch, "E1101", {"start": v(50.8, 26.62) * mm, "end": v(51.1, 25.34) * mm});
            skLineSegment(sketch, "E1102", {"start": v(51.1, 25.34) * mm, "end": v(51.4, 24.06) * mm});
            skLineSegment(sketch, "E1103", {"start": v(51.4, 24.06) * mm, "end": v(51.65, 22.78) * mm});
            skLineSegment(sketch, "E1104", {"start": v(51.65, 22.78) * mm, "end": v(51.87, 21.5) * mm});
            skLineSegment(sketch, "E1105", {"start": v(51.87, 21.5) * mm, "end": v(52.06, 20.23) * mm});
            skLineSegment(sketch, "E1106", {"start": v(52.06, 20.23) * mm, "end": v(52.21, 18.97) * mm});
            skLineSegment(sketch, "E1107", {"start": v(52.21, 18.97) * mm, "end": v(52.34, 17.71) * mm});
            skLineSegment(sketch, "E1108", {"start": v(52.34, 17.71) * mm, "end": v(52.44, 16.46) * mm});
            skLineSegment(sketch, "E1109", {"start": v(52.44, 16.46) * mm, "end": v(52.5, 15.22) * mm});
            skLineSegment(sketch, "E1110", {"start": v(52.5, 15.22) * mm, "end": v(52.55, 13.99) * mm});
            skLineSegment(sketch, "E1111", {"start": v(52.55, 13.99) * mm, "end": v(52.56, 12.77) * mm});
            skLineSegment(sketch, "E1112", {"start": v(52.56, 12.77) * mm, "end": v(52.55, 11.55) * mm});
            skLineSegment(sketch, "E1113", {"start": v(52.55, 11.55) * mm, "end": v(52.5, 10.32) * mm});
            skLineSegment(sketch, "E1114", {"start": v(52.5, 10.32) * mm, "end": v(52.44, 9.08) * mm});
            skLineSegment(sketch, "E1115", {"start": v(52.44, 9.08) * mm, "end": v(52.34, 7.83) * mm});
            skLineSegment(sketch, "E1116", {"start": v(52.34, 7.83) * mm, "end": v(52.21, 6.57) * mm});
            skLineSegment(sketch, "E1117", {"start": v(52.21, 6.57) * mm, "end": v(52.06, 5.3) * mm});
            skLineSegment(sketch, "E1118", {"start": v(52.06, 5.3) * mm, "end": v(51.87, 4.04) * mm});
            skLineSegment(sketch, "E1119", {"start": v(51.87, 4.04) * mm, "end": v(51.65, 2.76) * mm});
            skLineSegment(sketch, "E1120", {"start": v(51.65, 2.76) * mm, "end": v(51.4, 1.48) * mm});
            skLineSegment(sketch, "E1121", {"start": v(51.4, 1.48) * mm, "end": v(51.1, 0.2) * mm});
            skLineSegment(sketch, "E1122", {"start": v(51.1, 0.2) * mm, "end": v(50.8, -1.08) * mm});
            skLineSegment(sketch, "E1123", {"start": v(50.8, -1.08) * mm, "end": v(50.44, -2.36) * mm});
            skLineSegment(sketch, "E1124", {"start": v(50.44, -2.36) * mm, "end": v(50.06, -3.65) * mm});
            skLineSegment(sketch, "E1125", {"start": v(50.06, -3.65) * mm, "end": v(49.64, -4.93) * mm});
            skLineSegment(sketch, "E1126", {"start": v(49.64, -4.93) * mm, "end": v(49.19, -6.2) * mm});
            skLineSegment(sketch, "E1127", {"start": v(49.19, -6.2) * mm, "end": v(48.7, -7.48) * mm});
            skLineSegment(sketch, "E1128", {"start": v(48.7, -7.48) * mm, "end": v(48.18, -8.74) * mm});
            skLineSegment(sketch, "E1129", {"start": v(48.18, -8.74) * mm, "end": v(47.63, -10) * mm});
            skLineSegment(sketch, "E1130", {"start": v(47.63, -10) * mm, "end": v(47.04, -11.25) * mm});
            skLineSegment(sketch, "E1131", {"start": v(47.04, -11.25) * mm, "end": v(46.42, -12.5) * mm});
            skLineSegment(sketch, "E1132", {"start": v(46.42, -12.5) * mm, "end": v(45.76, -13.72) * mm});
            skLineSegment(sketch, "E1133", {"start": v(45.76, -13.72) * mm, "end": v(45.08, -14.94) * mm});
            skLineSegment(sketch, "E1134", {"start": v(45.08, -14.94) * mm, "end": v(44.35, -16.14) * mm});
            skLineSegment(sketch, "E1135", {"start": v(44.35, -16.14) * mm, "end": v(43.6, -17.33) * mm});
            skLineSegment(sketch, "E1136", {"start": v(43.6, -17.33) * mm, "end": v(42.81, -18.5) * mm});
            skLineSegment(sketch, "E1137", {"start": v(42.81, -18.5) * mm, "end": v(42, -19.65) * mm});
            skLineSegment(sketch, "E1138", {"start": v(42, -19.65) * mm, "end": v(41.14, -20.78) * mm});
            skLineSegment(sketch, "E1139", {"start": v(41.14, -20.78) * mm, "end": v(40.26, -21.9) * mm});
            skLineSegment(sketch, "E1140", {"start": v(40.26, -21.9) * mm, "end": v(39.35, -22.99) * mm});
            skLineSegment(sketch, "E1141", {"start": v(39.35, -22.99) * mm, "end": v(38.42, -24.06) * mm});
            skLineSegment(sketch, "E1142", {"start": v(38.42, -24.06) * mm, "end": v(37.45, -25.1) * mm});
            skLineSegment(sketch, "E1143", {"start": v(37.45, -25.1) * mm, "end": v(36.46, -26.12) * mm});
            skLineSegment(sketch, "E1144", {"start": v(36.46, -26.12) * mm, "end": v(35.44, -27.12) * mm});
            skLineSegment(sketch, "E1145", {"start": v(35.44, -27.12) * mm, "end": v(34.4, -28.08) * mm});
            skLineSegment(sketch, "E1146", {"start": v(34.4, -28.08) * mm, "end": v(33.32, -29.02) * mm});
            skLineSegment(sketch, "E1147", {"start": v(33.32, -29.02) * mm, "end": v(32.23, -29.93) * mm});
            skLineSegment(sketch, "E1148", {"start": v(32.23, -29.93) * mm, "end": v(31.12, -30.81) * mm});
            skLineSegment(sketch, "E1149", {"start": v(31.12, -30.81) * mm, "end": v(29.98, -31.66) * mm});
            skLineSegment(sketch, "E1150", {"start": v(29.98, -31.66) * mm, "end": v(28.83, -32.48) * mm});
            skLineSegment(sketch, "E1151", {"start": v(28.83, -32.48) * mm, "end": v(27.66, -33.27) * mm});
            skLineSegment(sketch, "E1152", {"start": v(27.66, -33.27) * mm, "end": v(26.47, -34.02) * mm});
            skLineSegment(sketch, "E1153", {"start": v(26.47, -34.02) * mm, "end": v(25.27, -34.74) * mm});
            skLineSegment(sketch, "E1154", {"start": v(25.27, -34.74) * mm, "end": v(24.05, -35.43) * mm});
            skLineSegment(sketch, "E1155", {"start": v(24.05, -35.43) * mm, "end": v(22.83, -36.09) * mm});
            skLineSegment(sketch, "E1156", {"start": v(22.83, -36.09) * mm, "end": v(21.59, -36.7) * mm});
            skLineSegment(sketch, "E1157", {"start": v(21.59, -36.7) * mm, "end": v(20.33, -37.3) * mm});
            skLineSegment(sketch, "E1158", {"start": v(20.33, -37.3) * mm, "end": v(19.08, -37.85) * mm});
            skLineSegment(sketch, "E1159", {"start": v(19.08, -37.85) * mm, "end": v(17.8, -38.37) * mm});
            skLineSegment(sketch, "E1160", {"start": v(17.8, -38.37) * mm, "end": v(16.54, -38.86) * mm});
            skLineSegment(sketch, "E1161", {"start": v(16.54, -38.86) * mm, "end": v(15.26, -39.3) * mm});
            skLineSegment(sketch, "E1162", {"start": v(15.26, -39.3) * mm, "end": v(13.98, -39.72) * mm});
            skLineSegment(sketch, "E1163", {"start": v(13.98, -39.72) * mm, "end": v(12.7, -40.1) * mm});
            skLineSegment(sketch, "E1164", {"start": v(12.7, -40.1) * mm, "end": v(11.41, -40.46) * mm});
            skLineSegment(sketch, "E1165", {"start": v(11.41, -40.46) * mm, "end": v(10.13, -40.78) * mm});
            skLineSegment(sketch, "E1166", {"start": v(10.13, -40.78) * mm, "end": v(8.85, -41.06) * mm});
            skLineSegment(sketch, "E1167", {"start": v(8.85, -41.06) * mm, "end": v(7.57, -41.31) * mm});
            skLineSegment(sketch, "E1168", {"start": v(7.57, -41.31) * mm, "end": v(6.3, -41.53) * mm});
            skLineSegment(sketch, "E1169", {"start": v(6.3, -41.53) * mm, "end": v(5.03, -41.72) * mm});
            skLineSegment(sketch, "E1170", {"start": v(5.03, -41.72) * mm, "end": v(3.76, -41.88) * mm});
            skLineSegment(sketch, "E1171", {"start": v(3.76, -41.88) * mm, "end": v(2.5, -42) * mm});
            skLineSegment(sketch, "E1172", {"start": v(2.5, -42) * mm, "end": v(1.26, -42.1) * mm});
            skLineSegment(sketch, "E1173", {"start": v(1.26, -42.1) * mm, "end": v(0.02, -42.18) * mm});
            skLineSegment(sketch, "E1174", {"start": v(0.02, -42.18) * mm, "end": v(-1.21, -42.22) * mm});
            skLineSegment(sketch, "E1175", {"start": v(-1.21, -42.22) * mm, "end": v(-2.44, -42.23) * mm});
            skLineSegment(sketch, "E1176", {"start": v(-2.44, -42.23) * mm, "end": v(-3.66, -42.22) * mm});
            skLineSegment(sketch, "E1177", {"start": v(-3.66, -42.22) * mm, "end": v(-4.89, -42.18) * mm});
            skLineSegment(sketch, "E1178", {"start": v(-4.89, -42.18) * mm, "end": v(-6.13, -42.1) * mm});
            skLineSegment(sketch, "E1179", {"start": v(-6.13, -42.1) * mm, "end": v(-7.38, -42) * mm});
            skLineSegment(sketch, "E1180", {"start": v(-7.38, -42) * mm, "end": v(-8.63, -41.88) * mm});
            skLineSegment(sketch, "E1181", {"start": v(-8.63, -41.88) * mm, "end": v(-9.9, -41.72) * mm});
            skLineSegment(sketch, "E1182", {"start": v(-9.9, -41.72) * mm, "end": v(-11.17, -41.53) * mm});
            skLineSegment(sketch, "E1183", {"start": v(-11.17, -41.53) * mm, "end": v(-12.44, -41.31) * mm});
            skLineSegment(sketch, "E1184", {"start": v(-12.44, -41.31) * mm, "end": v(-13.72, -41.06) * mm});
            skLineSegment(sketch, "E1185", {"start": v(-13.72, -41.06) * mm, "end": v(-15, -40.78) * mm});
            skLineSegment(sketch, "E1186", {"start": v(-15, -40.78) * mm, "end": v(-16.29, -40.46) * mm});
            skLineSegment(sketch, "E1187", {"start": v(-16.29, -40.46) * mm, "end": v(-17.57, -40.1) * mm});
            skLineSegment(sketch, "E1188", {"start": v(-17.57, -40.1) * mm, "end": v(-18.85, -39.72) * mm});
            skLineSegment(sketch, "E1189", {"start": v(-18.85, -39.72) * mm, "end": v(-20.13, -39.3) * mm});
            skLineSegment(sketch, "E1190", {"start": v(-20.13, -39.3) * mm, "end": v(-21.4, -38.86) * mm});
            skLineSegment(sketch, "E1191", {"start": v(-21.4, -38.86) * mm, "end": v(-22.68, -38.37) * mm});
            skLineSegment(sketch, "E1192", {"start": v(-22.68, -38.37) * mm, "end": v(-23.95, -37.85) * mm});
            skLineSegment(sketch, "E1193", {"start": v(-23.95, -37.85) * mm, "end": v(-25.2, -37.3) * mm});
            skLineSegment(sketch, "E1194", {"start": v(-25.2, -37.3) * mm, "end": v(-26.46, -36.7) * mm});
            skLineSegment(sketch, "E1195", {"start": v(-26.46, -36.7) * mm, "end": v(-27.7, -36.09) * mm});
            skLineSegment(sketch, "E1196", {"start": v(-27.7, -36.09) * mm, "end": v(-28.93, -35.43) * mm});
            skLineSegment(sketch, "E1197", {"start": v(-28.93, -35.43) * mm, "end": v(-30.14, -34.74) * mm});
            skLineSegment(sketch, "E1198", {"start": v(-30.14, -34.74) * mm, "end": v(-31.34, -34.02) * mm});
            skLineSegment(sketch, "E1199", {"start": v(-31.34, -34.02) * mm, "end": v(-32.53, -33.27) * mm});
            skLineSegment(sketch, "E1200", {"start": v(-32.53, -33.27) * mm, "end": v(-33.7, -32.48) * mm});
            skLineSegment(sketch, "E1201", {"start": v(-33.7, -32.48) * mm, "end": v(-34.86, -31.66) * mm});
            skLineSegment(sketch, "E1202", {"start": v(-34.86, -31.66) * mm, "end": v(-35.99, -30.81) * mm});
            skLineSegment(sketch, "E1203", {"start": v(-35.99, -30.81) * mm, "end": v(-37.1, -29.93) * mm});
            skLineSegment(sketch, "E1204", {"start": v(-37.1, -29.93) * mm, "end": v(-38.2, -29.02) * mm});
            skLineSegment(sketch, "E1205", {"start": v(-38.2, -29.02) * mm, "end": v(-39.26, -28.08) * mm});
            skLineSegment(sketch, "E1206", {"start": v(-39.26, -28.08) * mm, "end": v(-40.3, -27.12) * mm});
            skLineSegment(sketch, "E1207", {"start": v(-40.3, -27.12) * mm, "end": v(-41.33, -26.12) * mm});
            skLineSegment(sketch, "E1208", {"start": v(-41.33, -26.12) * mm, "end": v(-42.32, -25.1) * mm});
            skLineSegment(sketch, "E1209", {"start": v(-42.32, -25.1) * mm, "end": v(-43.29, -24.06) * mm});
            skLineSegment(sketch, "E1210", {"start": v(-43.29, -24.06) * mm, "end": v(-44.23, -22.99) * mm});
            skLineSegment(sketch, "E1211", {"start": v(-44.23, -22.99) * mm, "end": v(-45.14, -21.9) * mm});
            skLineSegment(sketch, "E1212", {"start": v(-45.14, -21.9) * mm, "end": v(-46.02, -20.78) * mm});
            skLineSegment(sketch, "E1213", {"start": v(-46.02, -20.78) * mm, "end": v(-46.86, -19.65) * mm});
            skLineSegment(sketch, "E1214", {"start": v(-46.86, -19.65) * mm, "end": v(-47.68, -18.5) * mm});
            skLineSegment(sketch, "E1215", {"start": v(-47.68, -18.5) * mm, "end": v(-48.47, -17.33) * mm});
            skLineSegment(sketch, "E1216", {"start": v(-48.47, -17.33) * mm, "end": v(-49.23, -16.14) * mm});
            skLineSegment(sketch, "E1217", {"start": v(-49.23, -16.14) * mm, "end": v(-49.95, -14.94) * mm});
            skLineSegment(sketch, "E1218", {"start": v(-49.95, -14.94) * mm, "end": v(-50.64, -13.72) * mm});
            skLineSegment(sketch, "E1219", {"start": v(-50.64, -13.72) * mm, "end": v(-51.3, -12.5) * mm});
            skLineSegment(sketch, "E1220", {"start": v(-51.3, -12.5) * mm, "end": v(-51.91, -11.25) * mm});
            skLineSegment(sketch, "E1221", {"start": v(-51.91, -11.25) * mm, "end": v(-52.5, -10) * mm});
            skLineSegment(sketch, "E1222", {"start": v(-52.5, -10) * mm, "end": v(-53.05, -8.74) * mm});
            skLineSegment(sketch, "E1223", {"start": v(-53.05, -8.74) * mm, "end": v(-53.57, -7.48) * mm});
            skLineSegment(sketch, "E1224", {"start": v(-53.57, -7.48) * mm, "end": v(-54.06, -6.2) * mm});
            skLineSegment(sketch, "E1225", {"start": v(-54.06, -6.2) * mm, "end": v(-54.51, -4.93) * mm});
            skLineSegment(sketch, "E1226", {"start": v(-54.51, -4.93) * mm, "end": v(-54.93, -3.65) * mm});
            skLineSegment(sketch, "E1227", {"start": v(-54.93, -3.65) * mm, "end": v(-55.31, -2.36) * mm});
            skLineSegment(sketch, "E1228", {"start": v(-55.31, -2.36) * mm, "end": v(-55.66, -1.08) * mm});
            skLineSegment(sketch, "E1229", {"start": v(-55.66, -1.08) * mm, "end": v(-55.98, 0.2) * mm});
            skLineSegment(sketch, "E1230", {"start": v(-55.98, 0.2) * mm, "end": v(-56.27, 1.48) * mm});
            skLineSegment(sketch, "E1231", {"start": v(-56.27, 1.48) * mm, "end": v(-56.52, 2.76) * mm});
            skLineSegment(sketch, "E1232", {"start": v(-56.52, 2.76) * mm, "end": v(-56.74, 4.04) * mm});
            skLineSegment(sketch, "E1233", {"start": v(-56.74, 4.04) * mm, "end": v(-56.93, 5.3) * mm});
            skLineSegment(sketch, "E1234", {"start": v(-56.93, 5.3) * mm, "end": v(-57.09, 6.57) * mm});
            skLineSegment(sketch, "E1235", {"start": v(-57.09, 6.57) * mm, "end": v(-57.21, 7.83) * mm});
            skLineSegment(sketch, "E1236", {"start": v(-57.21, 7.83) * mm, "end": v(-57.31, 9.08) * mm});
            skLineSegment(sketch, "E1237", {"start": v(-57.31, 9.08) * mm, "end": v(-57.38, 10.32) * mm});
            skLineSegment(sketch, "E1238", {"start": v(-57.38, 10.32) * mm, "end": v(-57.42, 11.55) * mm});
            skLineSegment(sketch, "E1239", {"start": v(-57.42, 11.55) * mm, "end": v(-57.44, 12.77) * mm});
            skLineSegment(sketch, "E1240", {"start": v(-57.44, 12.77) * mm, "end": v(-57.42, 13.99) * mm});
            skLineSegment(sketch, "E1241", {"start": v(-57.42, 13.99) * mm, "end": v(-57.38, 15.22) * mm});
            skLineSegment(sketch, "E1242", {"start": v(-57.38, 15.22) * mm, "end": v(-57.31, 16.46) * mm});
            skLineSegment(sketch, "E1243", {"start": v(-57.31, 16.46) * mm, "end": v(-57.21, 17.71) * mm});
            skLineSegment(sketch, "E1244", {"start": v(-57.21, 17.71) * mm, "end": v(-57.09, 18.97) * mm});
            skLineSegment(sketch, "E1245", {"start": v(-57.09, 18.97) * mm, "end": v(-56.93, 20.23) * mm});
            skLineSegment(sketch, "E1246", {"start": v(-56.93, 20.23) * mm, "end": v(-56.74, 21.5) * mm});
            skLineSegment(sketch, "E1247", {"start": v(-56.74, 21.5) * mm, "end": v(-56.52, 22.78) * mm});
            skLineSegment(sketch, "E1248", {"start": v(-56.52, 22.78) * mm, "end": v(-56.27, 24.06) * mm});
            skLineSegment(sketch, "E1249", {"start": v(-56.27, 24.06) * mm, "end": v(-55.98, 25.34) * mm});
            skLineSegment(sketch, "E1250", {"start": v(-55.98, 25.34) * mm, "end": v(-55.66, 26.62) * mm});
            skLineSegment(sketch, "E1251", {"start": v(-55.66, 26.62) * mm, "end": v(-55.31, 27.9) * mm});
            skLineSegment(sketch, "E1252", {"start": v(-55.31, 27.9) * mm, "end": v(-54.93, 29.18) * mm});
            skLineSegment(sketch, "E1253", {"start": v(-54.93, 29.18) * mm, "end": v(-54.51, 30.46) * mm});
            skLineSegment(sketch, "E1254", {"start": v(-54.51, 30.46) * mm, "end": v(-54.06, 31.74) * mm});
            skLineSegment(sketch, "E1255", {"start": v(-54.06, 31.74) * mm, "end": v(-53.57, 33.01) * mm});
            skLineSegment(sketch, "E1256", {"start": v(-53.57, 33.01) * mm, "end": v(-53.05, 34.28) * mm});
            skLineSegment(sketch, "E1257", {"start": v(-53.05, 34.28) * mm, "end": v(-52.5, 35.54) * mm});
            skLineSegment(sketch, "E1258", {"start": v(-52.5, 35.54) * mm, "end": v(-51.91, 36.79) * mm});
            skLineSegment(sketch, "E1259", {"start": v(-51.91, 36.79) * mm, "end": v(-51.3, 38.03) * mm});
            skLineSegment(sketch, "E1260", {"start": v(-51.3, 38.03) * mm, "end": v(-50.64, 39.26) * mm});
            skLineSegment(sketch, "E1261", {"start": v(-50.64, 39.26) * mm, "end": v(-49.95, 40.48) * mm});
            skLineSegment(sketch, "E1262", {"start": v(-49.95, 40.48) * mm, "end": v(-49.23, 41.68) * mm});
            skLineSegment(sketch, "E1263", {"start": v(-49.23, 41.68) * mm, "end": v(-48.47, 42.87) * mm});
            skLineSegment(sketch, "E1264", {"start": v(-48.47, 42.87) * mm, "end": v(-47.68, 44.04) * mm});
            skLineSegment(sketch, "E1265", {"start": v(-47.68, 44.04) * mm, "end": v(-46.86, 45.19) * mm});
            skLineSegment(sketch, "E1266", {"start": v(-46.86, 45.19) * mm, "end": v(-46.02, 46.32) * mm});
            skLineSegment(sketch, "E1267", {"start": v(-46.02, 46.32) * mm, "end": v(-45.14, 47.44) * mm});
            skLineSegment(sketch, "E1268", {"start": v(-45.14, 47.44) * mm, "end": v(-44.23, 48.53) * mm});
            skLineSegment(sketch, "E1269", {"start": v(-44.23, 48.53) * mm, "end": v(-43.29, 49.6) * mm});
            skLineSegment(sketch, "E1270", {"start": v(-43.29, 49.6) * mm, "end": v(-42.32, 50.64) * mm});
            skLineSegment(sketch, "E1271", {"start": v(-42.32, 50.64) * mm, "end": v(-41.33, 51.66) * mm});
            skLineSegment(sketch, "E1272", {"start": v(-41.33, 51.66) * mm, "end": v(-40.3, 52.65) * mm});
            skLineSegment(sketch, "E1273", {"start": v(-40.3, 52.65) * mm, "end": v(-39.26, 53.62) * mm});
            skLineSegment(sketch, "E1274", {"start": v(-39.26, 53.62) * mm, "end": v(-38.2, 54.56) * mm});
            skLineSegment(sketch, "E1275", {"start": v(-38.2, 54.56) * mm, "end": v(-37.1, 55.47) * mm});
            skLineSegment(sketch, "E1276", {"start": v(-37.1, 55.47) * mm, "end": v(-35.99, 56.35) * mm});
            skLineSegment(sketch, "E1277", {"start": v(-35.99, 56.35) * mm, "end": v(-34.86, 57.2) * mm});
            skLineSegment(sketch, "E1278", {"start": v(-34.86, 57.2) * mm, "end": v(-33.7, 58.02) * mm});
            skLineSegment(sketch, "E1279", {"start": v(-33.7, 58.02) * mm, "end": v(-32.53, 58.8) * mm});
            skLineSegment(sketch, "E1280", {"start": v(-32.53, 58.8) * mm, "end": v(-31.34, 59.56) * mm});
            skLineSegment(sketch, "E1281", {"start": v(-31.34, 59.56) * mm, "end": v(-30.14, 60.28) * mm});
            skLineSegment(sketch, "E1282", {"start": v(-30.14, 60.28) * mm, "end": v(-28.93, 60.97) * mm});
            skLineSegment(sketch, "E1283", {"start": v(-28.93, 60.97) * mm, "end": v(-27.7, 61.62) * mm});
            skLineSegment(sketch, "E1284", {"start": v(-27.7, 61.62) * mm, "end": v(-26.46, 62.25) * mm});
            skLineSegment(sketch, "E1285", {"start": v(-26.46, 62.25) * mm, "end": v(-25.2, 62.83) * mm});
            skLineSegment(sketch, "E1286", {"start": v(-25.2, 62.83) * mm, "end": v(-23.95, 63.39) * mm});
            skLineSegment(sketch, "E1287", {"start": v(-23.95, 63.39) * mm, "end": v(-22.68, 63.9) * mm});
            skLineSegment(sketch, "E1288", {"start": v(-22.68, 63.9) * mm, "end": v(-21.4, 64.4) * mm});
            skLineSegment(sketch, "E1289", {"start": v(-21.4, 64.4) * mm, "end": v(-20.13, 64.84) * mm});
            skLineSegment(sketch, "E1290", {"start": v(-20.13, 64.84) * mm, "end": v(-18.85, 65.26) * mm});
            skLineSegment(sketch, "E1291", {"start": v(-18.85, 65.26) * mm, "end": v(-17.57, 65.65) * mm});
            skLineSegment(sketch, "E1292", {"start": v(-17.57, 65.65) * mm, "end": v(-16.29, 66) * mm});
            skLineSegment(sketch, "E1293", {"start": v(-16.29, 66) * mm, "end": v(-15, 66.31) * mm});
            skLineSegment(sketch, "E1294", {"start": v(-15, 66.31) * mm, "end": v(-13.72, 66.6) * mm});
            skLineSegment(sketch, "E1295", {"start": v(-13.72, 66.6) * mm, "end": v(-12.44, 66.85) * mm});
            skLineSegment(sketch, "E1296", {"start": v(-12.44, 66.85) * mm, "end": v(-11.17, 67.07) * mm});
            skLineSegment(sketch, "E1297", {"start": v(-11.17, 67.07) * mm, "end": v(-9.9, 67.26) * mm});
            skLineSegment(sketch, "E1298", {"start": v(-9.9, 67.26) * mm, "end": v(-8.63, 67.42) * mm});
            skLineSegment(sketch, "E1299", {"start": v(-8.63, 67.42) * mm, "end": v(-7.38, 67.55) * mm});
            skLineSegment(sketch, "E1300", {"start": v(-7.38, 67.55) * mm, "end": v(-6.13, 67.64) * mm});
            skLineSegment(sketch, "E1301", {"start": v(-6.13, 67.64) * mm, "end": v(-4.89, 67.71) * mm});
            skLineSegment(sketch, "E1302", {"start": v(-4.89, 67.71) * mm, "end": v(-3.66, 67.76) * mm});
            skLineSegment(sketch, "E1303", {"start": v(-3.66, 67.76) * mm, "end": v(-2.44, 67.77) * mm});
            skLineSegment(sketch, "E1304", {"start": v(-160.44, 19.17) * mm, "end": v(-155.67, 19.17) * mm});
            skLineSegment(sketch, "E1305", {"start": v(-155.67, 19.17) * mm, "end": v(-155.67, -6.23) * mm});
            skLineSegment(sketch, "E1306", {"start": v(-155.67, -6.23) * mm, "end": v(-160.44, -6.23) * mm});
            skLineSegment(sketch, "E1307", {"start": v(-160.44, -6.23) * mm, "end": v(-2.44, -98.73) * mm});
            skLineSegment(sketch, "E1308", {"start": v(-2.44, -98.73) * mm, "end": v(141.8, -98.73) * mm});
            skLineSegment(sketch, "E1309", {"start": v(141.8, -98.73) * mm, "end": v(141.8, -73.33) * mm});
            skLineSegment(sketch, "E1310", {"start": v(141.8, -73.33) * mm, "end": v(146.56, -73.33) * mm});
            skLineSegment(sketch, "E1311", {"start": v(146.56, -73.33) * mm, "end": v(146.56, 73.33) * mm});
            skLineSegment(sketch, "E1312", {"start": v(146.56, 73.33) * mm, "end": v(141.8, 73.33) * mm});
            skLineSegment(sketch, "E1313", {"start": v(141.8, 73.33) * mm, "end": v(141.8, 98.73) * mm});
            skLineSegment(sketch, "E1314", {"start": v(141.8, 98.73) * mm, "end": v(-155.67, 98.73) * mm});
            skLineSegment(sketch, "E1315", {"start": v(-155.67, 98.73) * mm, "end": v(-155.67, 73.33) * mm});
            skLineSegment(sketch, "E1316", {"start": v(-155.67, 73.33) * mm, "end": v(-160.44, 73.33) * mm});
            skLineSegment(sketch, "E1317", {"start": v(-160.44, 73.33) * mm, "end": v(-160.44, 19.17) * mm});
            skLineSegment(sketch, "E1318", {"start": v(256.5, 73.33) * mm, "end": v(256.5, 98.73) * mm});
            skLineSegment(sketch, "E1319", {"start": v(256.5, 98.73) * mm, "end": v(177.03, 98.73) * mm});
            skLineSegment(sketch, "E1320", {"start": v(177.03, 98.73) * mm, "end": v(172.27, 98.73) * mm});
            skLineSegment(sketch, "E1321", {"start": v(172.27, 98.73) * mm, "end": v(172.27, 73.33) * mm});
            skLineSegment(sketch, "E1322", {"start": v(172.27, 73.33) * mm, "end": v(177.03, 73.33) * mm});
            skLineSegment(sketch, "E1323", {"start": v(177.03, 73.33) * mm, "end": v(177.03, -73.33) * mm});
            skLineSegment(sketch, "E1324", {"start": v(177.03, -73.33) * mm, "end": v(172.27, -73.33) * mm});
            skLineSegment(sketch, "E1325", {"start": v(172.27, -73.33) * mm, "end": v(172.27, -98.73) * mm});
            skLineSegment(sketch, "E1326", {"start": v(172.27, -98.73) * mm, "end": v(177.03, -98.73) * mm});
            skLineSegment(sketch, "E1327", {"start": v(177.03, -98.73) * mm, "end": v(256.5, -98.73) * mm});
            skLineSegment(sketch, "E1328", {"start": v(256.5, -98.73) * mm, "end": v(256.5, -73.33) * mm});
            skLineSegment(sketch, "E1329", {"start": v(256.5, -73.33) * mm, "end": v(261.27, -73.33) * mm});
            skLineSegment(sketch, "E1330", {"start": v(261.27, -73.33) * mm, "end": v(261.27, 73.33) * mm});
            skLineSegment(sketch, "E1331", {"start": v(261.27, 73.33) * mm, "end": v(256.5, 73.33) * mm});
            skLineSegment(sketch, "E1332", {"start": v(330.5, -50.52) * mm, "end": v(330.62, -50.52) * mm});
            skLineSegment(sketch, "E1333", {"start": v(330.62, -50.52) * mm, "end": v(330.75, -50.52) * mm});
            skLineSegment(sketch, "E1334", {"start": v(330.75, -50.52) * mm, "end": v(330.88, -50.53) * mm});
            skLineSegment(sketch, "E1335", {"start": v(330.88, -50.53) * mm, "end": v(331, -50.54) * mm});
            skLineSegment(sketch, "E1336", {"start": v(331, -50.54) * mm, "end": v(331.14, -50.56) * mm});
            skLineSegment(sketch, "E1337", {"start": v(331.14, -50.56) * mm, "end": v(331.27, -50.57) * mm});
            skLineSegment(sketch, "E1338", {"start": v(331.27, -50.57) * mm, "end": v(331.4, -50.6) * mm});
            skLineSegment(sketch, "E1339", {"start": v(331.4, -50.6) * mm, "end": v(331.54, -50.61) * mm});
            skLineSegment(sketch, "E1340", {"start": v(331.54, -50.61) * mm, "end": v(331.67, -50.64) * mm});
            skLineSegment(sketch, "E1341", {"start": v(331.67, -50.64) * mm, "end": v(331.8, -50.67) * mm});
            skLineSegment(sketch, "E1342", {"start": v(331.8, -50.67) * mm, "end": v(331.94, -50.7) * mm});
            skLineSegment(sketch, "E1343", {"start": v(331.94, -50.7) * mm, "end": v(332.07, -50.74) * mm});
            skLineSegment(sketch, "E1344", {"start": v(332.07, -50.74) * mm, "end": v(332.2, -50.78) * mm});
            skLineSegment(sketch, "E1345", {"start": v(332.2, -50.78) * mm, "end": v(332.34, -50.82) * mm});
            skLineSegment(sketch, "E1346", {"start": v(332.34, -50.82) * mm, "end": v(332.48, -50.87) * mm});
            skLineSegment(sketch, "E1347", {"start": v(332.48, -50.87) * mm, "end": v(332.6, -50.92) * mm});
            skLineSegment(sketch, "E1348", {"start": v(332.6, -50.92) * mm, "end": v(332.74, -50.98) * mm});
            skLineSegment(sketch, "E1349", {"start": v(332.74, -50.98) * mm, "end": v(332.87, -51.03) * mm});
            skLineSegment(sketch, "E1350", {"start": v(332.87, -51.03) * mm, "end": v(333, -51.1) * mm});
            skLineSegment(sketch, "E1351", {"start": v(333, -51.1) * mm, "end": v(333.13, -51.16) * mm});
            skLineSegment(sketch, "E1352", {"start": v(333.13, -51.16) * mm, "end": v(333.26, -51.23) * mm});
            skLineSegment(sketch, "E1353", {"start": v(333.26, -51.23) * mm, "end": v(333.39, -51.3) * mm});
            skLineSegment(sketch, "E1354", {"start": v(333.39, -51.3) * mm, "end": v(333.51, -51.38) * mm});
            skLineSegment(sketch, "E1355", {"start": v(333.51, -51.38) * mm, "end": v(333.64, -51.46) * mm});
            skLineSegment(sketch, "E1356", {"start": v(333.64, -51.46) * mm, "end": v(333.76, -51.54) * mm});
            skLineSegment(sketch, "E1357", {"start": v(333.76, -51.54) * mm, "end": v(333.88, -51.62) * mm});
            skLineSegment(sketch, "E1358", {"start": v(333.88, -51.62) * mm, "end": v(334, -51.71) * mm});
            skLineSegment(sketch, "E1359", {"start": v(334, -51.71) * mm, "end": v(334.12, -51.8) * mm});
            skLineSegment(sketch, "E1360", {"start": v(334.12, -51.8) * mm, "end": v(334.23, -51.9) * mm});
            skLineSegment(sketch, "E1361", {"start": v(334.23, -51.9) * mm, "end": v(334.34, -52) * mm});
            skLineSegment(sketch, "E1362", {"start": v(334.34, -52) * mm, "end": v(334.45, -52.1) * mm});
            skLineSegment(sketch, "E1363", {"start": v(334.45, -52.1) * mm, "end": v(334.56, -52.2) * mm});
            skLineSegment(sketch, "E1364", {"start": v(334.56, -52.2) * mm, "end": v(334.66, -52.3) * mm});
            skLineSegment(sketch, "E1365", {"start": v(334.66, -52.3) * mm, "end": v(334.76, -52.42) * mm});
            skLineSegment(sketch, "E1366", {"start": v(334.76, -52.42) * mm, "end": v(334.86, -52.53) * mm});
            skLineSegment(sketch, "E1367", {"start": v(334.86, -52.53) * mm, "end": v(334.96, -52.64) * mm});
            skLineSegment(sketch, "E1368", {"start": v(334.96, -52.64) * mm, "end": v(335.05, -52.76) * mm});
            skLineSegment(sketch, "E1369", {"start": v(335.05, -52.76) * mm, "end": v(335.14, -52.88) * mm});
            skLineSegment(sketch, "E1370", {"start": v(335.14, -52.88) * mm, "end": v(335.22, -53) * mm});
            skLineSegment(sketch, "E1371", {"start": v(335.22, -53) * mm, "end": v(335.3, -53.12) * mm});
            skLineSegment(sketch, "E1372", {"start": v(335.3, -53.12) * mm, "end": v(335.38, -53.25) * mm});
            skLineSegment(sketch, "E1373", {"start": v(335.38, -53.25) * mm, "end": v(335.46, -53.37) * mm});
            skLineSegment(sketch, "E1374", {"start": v(335.46, -53.37) * mm, "end": v(335.53, -53.5) * mm});
            skLineSegment(sketch, "E1375", {"start": v(335.53, -53.5) * mm, "end": v(335.6, -53.63) * mm});
            skLineSegment(sketch, "E1376", {"start": v(335.6, -53.63) * mm, "end": v(335.67, -53.76) * mm});
            skLineSegment(sketch, "E1377", {"start": v(335.67, -53.76) * mm, "end": v(335.73, -53.89) * mm});
            skLineSegment(sketch, "E1378", {"start": v(335.73, -53.89) * mm, "end": v(335.78, -54.02) * mm});
            skLineSegment(sketch, "E1379", {"start": v(335.78, -54.02) * mm, "end": v(335.84, -54.15) * mm});
            skLineSegment(sketch, "E1380", {"start": v(335.84, -54.15) * mm, "end": v(335.89, -54.29) * mm});
            skLineSegment(sketch, "E1381", {"start": v(335.89, -54.29) * mm, "end": v(335.94, -54.42) * mm});
            skLineSegment(sketch, "E1382", {"start": v(335.94, -54.42) * mm, "end": v(335.98, -54.55) * mm});
            skLineSegment(sketch, "E1383", {"start": v(335.98, -54.55) * mm, "end": v(336.02, -54.69) * mm});
            skLineSegment(sketch, "E1384", {"start": v(336.02, -54.69) * mm, "end": v(336.06, -54.82) * mm});
            skLineSegment(sketch, "E1385", {"start": v(336.06, -54.82) * mm, "end": v(336.1, -54.95) * mm});
            skLineSegment(sketch, "E1386", {"start": v(336.1, -54.95) * mm, "end": v(336.12, -55.09) * mm});
            skLineSegment(sketch, "E1387", {"start": v(336.12, -55.09) * mm, "end": v(336.15, -55.22) * mm});
            skLineSegment(sketch, "E1388", {"start": v(336.15, -55.22) * mm, "end": v(336.17, -55.36) * mm});
            skLineSegment(sketch, "E1389", {"start": v(336.17, -55.36) * mm, "end": v(336.19, -55.49) * mm});
            skLineSegment(sketch, "E1390", {"start": v(336.19, -55.49) * mm, "end": v(336.2, -55.62) * mm});
            skLineSegment(sketch, "E1391", {"start": v(336.2, -55.62) * mm, "end": v(336.22, -55.75) * mm});
            skLineSegment(sketch, "E1392", {"start": v(336.22, -55.75) * mm, "end": v(336.23, -55.88) * mm});
            skLineSegment(sketch, "E1393", {"start": v(336.23, -55.88) * mm, "end": v(336.24, -56.01) * mm});
            skLineSegment(sketch, "E1394", {"start": v(336.24, -56.01) * mm, "end": v(336.24, -56.14) * mm});
            skLineSegment(sketch, "E1395", {"start": v(336.24, -56.14) * mm, "end": v(336.24, -56.27) * mm});
            skLineSegment(sketch, "E1396", {"start": v(336.24, -56.27) * mm, "end": v(336.24, -56.4) * mm});
            skLineSegment(sketch, "E1397", {"start": v(336.24, -56.4) * mm, "end": v(336.24, -56.53) * mm});
            skLineSegment(sketch, "E1398", {"start": v(336.24, -56.53) * mm, "end": v(336.23, -56.65) * mm});
            skLineSegment(sketch, "E1399", {"start": v(336.23, -56.65) * mm, "end": v(336.22, -56.79) * mm});
            skLineSegment(sketch, "E1400", {"start": v(336.22, -56.79) * mm, "end": v(336.2, -56.92) * mm});
            skLineSegment(sketch, "E1401", {"start": v(336.2, -56.92) * mm, "end": v(336.19, -57.05) * mm});
            skLineSegment(sketch, "E1402", {"start": v(336.19, -57.05) * mm, "end": v(336.17, -57.18) * mm});
            skLineSegment(sketch, "E1403", {"start": v(336.17, -57.18) * mm, "end": v(336.15, -57.32) * mm});
            skLineSegment(sketch, "E1404", {"start": v(336.15, -57.32) * mm, "end": v(336.12, -57.45) * mm});
            skLineSegment(sketch, "E1405", {"start": v(336.12, -57.45) * mm, "end": v(336.1, -57.58) * mm});
            skLineSegment(sketch, "E1406", {"start": v(336.1, -57.58) * mm, "end": v(336.06, -57.72) * mm});
            skLineSegment(sketch, "E1407", {"start": v(336.06, -57.72) * mm, "end": v(336.02, -57.85) * mm});
            skLineSegment(sketch, "E1408", {"start": v(336.02, -57.85) * mm, "end": v(335.98, -57.98) * mm});
            skLineSegment(sketch, "E1409", {"start": v(335.98, -57.98) * mm, "end": v(335.94, -58.12) * mm});
            skLineSegment(sketch, "E1410", {"start": v(335.94, -58.12) * mm, "end": v(335.89, -58.25) * mm});
            skLineSegment(sketch, "E1411", {"start": v(335.89, -58.25) * mm, "end": v(335.84, -58.39) * mm});
            skLineSegment(sketch, "E1412", {"start": v(335.84, -58.39) * mm, "end": v(335.78, -58.52) * mm});
            skLineSegment(sketch, "E1413", {"start": v(335.78, -58.52) * mm, "end": v(335.73, -58.65) * mm});
            skLineSegment(sketch, "E1414", {"start": v(335.73, -58.65) * mm, "end": v(335.67, -58.78) * mm});
            skLineSegment(sketch, "E1415", {"start": v(335.67, -58.78) * mm, "end": v(335.6, -58.9) * mm});
            skLineSegment(sketch, "E1416", {"start": v(335.6, -58.9) * mm, "end": v(335.53, -59.04) * mm});
            skLineSegment(sketch, "E1417", {"start": v(335.53, -59.04) * mm, "end": v(335.46, -59.17) * mm});
            skLineSegment(sketch, "E1418", {"start": v(335.46, -59.17) * mm, "end": v(335.38, -59.3) * mm});
            skLineSegment(sketch, "E1419", {"start": v(335.38, -59.3) * mm, "end": v(335.3, -59.42) * mm});
            skLineSegment(sketch, "E1420", {"start": v(335.3, -59.42) * mm, "end": v(335.22, -59.54) * mm});
            skLineSegment(sketch, "E1421", {"start": v(335.22, -59.54) * mm, "end": v(335.14, -59.66) * mm});
            skLineSegment(sketch, "E1422", {"start": v(335.14, -59.66) * mm, "end": v(335.05, -59.78) * mm});
            skLineSegment(sketch, "E1423", {"start": v(335.05, -59.78) * mm, "end": v(334.96, -59.9) * mm});
            skLineSegment(sketch, "E1424", {"start": v(334.96, -59.9) * mm, "end": v(334.86, -60) * mm});
            skLineSegment(sketch, "E1425", {"start": v(334.86, -60) * mm, "end": v(334.76, -60.12) * mm});
            skLineSegment(sketch, "E1426", {"start": v(334.76, -60.12) * mm, "end": v(334.66, -60.23) * mm});
            skLineSegment(sketch, "E1427", {"start": v(334.66, -60.23) * mm, "end": v(334.56, -60.33) * mm});
            skLineSegment(sketch, "E1428", {"start": v(334.56, -60.33) * mm, "end": v(334.45, -60.44) * mm});
            skLineSegment(sketch, "E1429", {"start": v(334.45, -60.44) * mm, "end": v(334.34, -60.54) * mm});
            skLineSegment(sketch, "E1430", {"start": v(334.34, -60.54) * mm, "end": v(334.23, -60.64) * mm});
            skLineSegment(sketch, "E1431", {"start": v(334.23, -60.64) * mm, "end": v(334.12, -60.73) * mm});
            skLineSegment(sketch, "E1432", {"start": v(334.12, -60.73) * mm, "end": v(334, -60.82) * mm});
            skLineSegment(sketch, "E1433", {"start": v(334, -60.82) * mm, "end": v(333.88, -60.91) * mm});
            skLineSegment(sketch, "E1434", {"start": v(333.88, -60.91) * mm, "end": v(333.76, -61) * mm});
            skLineSegment(sketch, "E1435", {"start": v(333.76, -61) * mm, "end": v(333.64, -61.08) * mm});
            skLineSegment(sketch, "E1436", {"start": v(333.64, -61.08) * mm, "end": v(333.51, -61.16) * mm});
            skLineSegment(sketch, "E1437", {"start": v(333.51, -61.16) * mm, "end": v(333.39, -61.24) * mm});
            skLineSegment(sketch, "E1438", {"start": v(333.39, -61.24) * mm, "end": v(333.26, -61.3) * mm});
            skLineSegment(sketch, "E1439", {"start": v(333.26, -61.3) * mm, "end": v(333.13, -61.38) * mm});
            skLineSegment(sketch, "E1440", {"start": v(333.13, -61.38) * mm, "end": v(333, -61.44) * mm});
            skLineSegment(sketch, "E1441", {"start": v(333, -61.44) * mm, "end": v(332.87, -61.5) * mm});
            skLineSegment(sketch, "E1442", {"start": v(332.87, -61.5) * mm, "end": v(332.74, -61.56) * mm});
            skLineSegment(sketch, "E1443", {"start": v(332.74, -61.56) * mm, "end": v(332.6, -61.62) * mm});
            skLineSegment(sketch, "E1444", {"start": v(332.6, -61.62) * mm, "end": v(332.48, -61.67) * mm});
            skLineSegment(sketch, "E1445", {"start": v(332.48, -61.67) * mm, "end": v(332.34, -61.71) * mm});
            skLineSegment(sketch, "E1446", {"start": v(332.34, -61.71) * mm, "end": v(332.2, -61.76) * mm});
            skLineSegment(sketch, "E1447", {"start": v(332.2, -61.76) * mm, "end": v(332.07, -61.8) * mm});
            skLineSegment(sketch, "E1448", {"start": v(332.07, -61.8) * mm, "end": v(331.94, -61.83) * mm});
            skLineSegment(sketch, "E1449", {"start": v(331.94, -61.83) * mm, "end": v(331.8, -61.87) * mm});
            skLineSegment(sketch, "E1450", {"start": v(331.8, -61.87) * mm, "end": v(331.67, -61.9) * mm});
            skLineSegment(sketch, "E1451", {"start": v(331.67, -61.9) * mm, "end": v(331.54, -61.92) * mm});
            skLineSegment(sketch, "E1452", {"start": v(331.54, -61.92) * mm, "end": v(331.4, -61.95) * mm});
            skLineSegment(sketch, "E1453", {"start": v(331.4, -61.95) * mm, "end": v(331.27, -61.97) * mm});
            skLineSegment(sketch, "E1454", {"start": v(331.27, -61.97) * mm, "end": v(331.14, -61.98) * mm});
            skLineSegment(sketch, "E1455", {"start": v(331.14, -61.98) * mm, "end": v(331, -62) * mm});
            skLineSegment(sketch, "E1456", {"start": v(331, -62) * mm, "end": v(330.88, -62) * mm});
            skLineSegment(sketch, "E1457", {"start": v(330.88, -62) * mm, "end": v(330.75, -62.01) * mm});
            skLineSegment(sketch, "E1458", {"start": v(330.75, -62.01) * mm, "end": v(330.62, -62.02) * mm});
            skLineSegment(sketch, "E1459", {"start": v(330.62, -62.02) * mm, "end": v(330.5, -62.02) * mm});
            skLineSegment(sketch, "E1460", {"start": v(330.5, -62.02) * mm, "end": v(330.37, -62.02) * mm});
            skLineSegment(sketch, "E1461", {"start": v(330.37, -62.02) * mm, "end": v(330.24, -62.01) * mm});
            skLineSegment(sketch, "E1462", {"start": v(330.24, -62.01) * mm, "end": v(330.1, -62) * mm});
            skLineSegment(sketch, "E1463", {"start": v(330.1, -62) * mm, "end": v(329.98, -62) * mm});
            skLineSegment(sketch, "E1464", {"start": v(329.98, -62) * mm, "end": v(329.84, -61.98) * mm});
            skLineSegment(sketch, "E1465", {"start": v(329.84, -61.98) * mm, "end": v(329.71, -61.97) * mm});
            skLineSegment(sketch, "E1466", {"start": v(329.71, -61.97) * mm, "end": v(329.58, -61.95) * mm});
            skLineSegment(sketch, "E1467", {"start": v(329.58, -61.95) * mm, "end": v(329.45, -61.92) * mm});
            skLineSegment(sketch, "E1468", {"start": v(329.45, -61.92) * mm, "end": v(329.31, -61.9) * mm});
            skLineSegment(sketch, "E1469", {"start": v(329.31, -61.9) * mm, "end": v(329.18, -61.87) * mm});
            skLineSegment(sketch, "E1470", {"start": v(329.18, -61.87) * mm, "end": v(329.04, -61.83) * mm});
            skLineSegment(sketch, "E1471", {"start": v(329.04, -61.83) * mm, "end": v(328.91, -61.8) * mm});
            skLineSegment(sketch, "E1472", {"start": v(328.91, -61.8) * mm, "end": v(328.78, -61.76) * mm});
            skLineSegment(sketch, "E1473", {"start": v(328.78, -61.76) * mm, "end": v(328.64, -61.71) * mm});
            skLineSegment(sketch, "E1474", {"start": v(328.64, -61.71) * mm, "end": v(328.5, -61.67) * mm});
            skLineSegment(sketch, "E1475", {"start": v(328.5, -61.67) * mm, "end": v(328.38, -61.62) * mm});
            skLineSegment(sketch, "E1476", {"start": v(328.38, -61.62) * mm, "end": v(328.24, -61.56) * mm});
            skLineSegment(sketch, "E1477", {"start": v(328.24, -61.56) * mm, "end": v(328.11, -61.5) * mm});
            skLineSegment(sketch, "E1478", {"start": v(328.11, -61.5) * mm, "end": v(327.98, -61.44) * mm});
            skLineSegment(sketch, "E1479", {"start": v(327.98, -61.44) * mm, "end": v(327.85, -61.38) * mm});
            skLineSegment(sketch, "E1480", {"start": v(327.85, -61.38) * mm, "end": v(327.72, -61.3) * mm});
            skLineSegment(sketch, "E1481", {"start": v(327.72, -61.3) * mm, "end": v(327.6, -61.24) * mm});
            skLineSegment(sketch, "E1482", {"start": v(327.6, -61.24) * mm, "end": v(327.47, -61.16) * mm});
            skLineSegment(sketch, "E1483", {"start": v(327.47, -61.16) * mm, "end": v(327.35, -61.08) * mm});
            skLineSegment(sketch, "E1484", {"start": v(327.35, -61.08) * mm, "end": v(327.22, -61) * mm});
            skLineSegment(sketch, "E1485", {"start": v(327.22, -61) * mm, "end": v(327.1, -60.91) * mm});
            skLineSegment(sketch, "E1486", {"start": v(327.1, -60.91) * mm, "end": v(326.98, -60.82) * mm});
            skLineSegment(sketch, "E1487", {"start": v(326.98, -60.82) * mm, "end": v(326.87, -60.73) * mm});
            skLineSegment(sketch, "E1488", {"start": v(326.87, -60.73) * mm, "end": v(326.75, -60.64) * mm});
            skLineSegment(sketch, "E1489", {"start": v(326.75, -60.64) * mm, "end": v(326.64, -60.54) * mm});
            skLineSegment(sketch, "E1490", {"start": v(326.64, -60.54) * mm, "end": v(326.53, -60.44) * mm});
            skLineSegment(sketch, "E1491", {"start": v(326.53, -60.44) * mm, "end": v(326.43, -60.33) * mm});
            skLineSegment(sketch, "E1492", {"start": v(326.43, -60.33) * mm, "end": v(326.32, -60.23) * mm});
            skLineSegment(sketch, "E1493", {"start": v(326.32, -60.23) * mm, "end": v(326.22, -60.12) * mm});
            skLineSegment(sketch, "E1494", {"start": v(326.22, -60.12) * mm, "end": v(326.12, -60) * mm});
            skLineSegment(sketch, "E1495", {"start": v(326.12, -60) * mm, "end": v(326.03, -59.9) * mm});
            skLineSegment(sketch, "E1496", {"start": v(326.03, -59.9) * mm, "end": v(325.94, -59.78) * mm});
            skLineSegment(sketch, "E1497", {"start": v(325.94, -59.78) * mm, "end": v(325.85, -59.66) * mm});
            skLineSegment(sketch, "E1498", {"start": v(325.85, -59.66) * mm, "end": v(325.76, -59.54) * mm});
            skLineSegment(sketch, "E1499", {"start": v(325.76, -59.54) * mm, "end": v(325.68, -59.42) * mm});
            skLineSegment(sketch, "E1500", {"start": v(325.68, -59.42) * mm, "end": v(325.6, -59.3) * mm});
            skLineSegment(sketch, "E1501", {"start": v(325.6, -59.3) * mm, "end": v(325.53, -59.17) * mm});
            skLineSegment(sketch, "E1502", {"start": v(325.53, -59.17) * mm, "end": v(325.45, -59.04) * mm});
            skLineSegment(sketch, "E1503", {"start": v(325.45, -59.04) * mm, "end": v(325.38, -58.9) * mm});
            skLineSegment(sketch, "E1504", {"start": v(325.38, -58.9) * mm, "end": v(325.32, -58.78) * mm});
            skLineSegment(sketch, "E1505", {"start": v(325.32, -58.78) * mm, "end": v(325.26, -58.65) * mm});
            skLineSegment(sketch, "E1506", {"start": v(325.26, -58.65) * mm, "end": v(325.2, -58.52) * mm});
            skLineSegment(sketch, "E1507", {"start": v(325.2, -58.52) * mm, "end": v(325.15, -58.39) * mm});
            skLineSegment(sketch, "E1508", {"start": v(325.15, -58.39) * mm, "end": v(325.1, -58.25) * mm});
            skLineSegment(sketch, "E1509", {"start": v(325.1, -58.25) * mm, "end": v(325.05, -58.12) * mm});
            skLineSegment(sketch, "E1510", {"start": v(325.05, -58.12) * mm, "end": v(325, -57.98) * mm});
            skLineSegment(sketch, "E1511", {"start": v(325, -57.98) * mm, "end": v(324.96, -57.85) * mm});
            skLineSegment(sketch, "E1512", {"start": v(324.96, -57.85) * mm, "end": v(324.93, -57.72) * mm});
            skLineSegment(sketch, "E1513", {"start": v(324.93, -57.72) * mm, "end": v(324.9, -57.58) * mm});
            skLineSegment(sketch, "E1514", {"start": v(324.9, -57.58) * mm, "end": v(324.87, -57.45) * mm});
            skLineSegment(sketch, "E1515", {"start": v(324.87, -57.45) * mm, "end": v(324.84, -57.32) * mm});
            skLineSegment(sketch, "E1516", {"start": v(324.84, -57.32) * mm, "end": v(324.82, -57.18) * mm});
            skLineSegment(sketch, "E1517", {"start": v(324.82, -57.18) * mm, "end": v(324.8, -57.05) * mm});
            skLineSegment(sketch, "E1518", {"start": v(324.8, -57.05) * mm, "end": v(324.78, -56.92) * mm});
            skLineSegment(sketch, "E1519", {"start": v(324.78, -56.92) * mm, "end": v(324.77, -56.79) * mm});
            skLineSegment(sketch, "E1520", {"start": v(324.77, -56.79) * mm, "end": v(324.76, -56.65) * mm});
            skLineSegment(sketch, "E1521", {"start": v(324.76, -56.65) * mm, "end": v(324.75, -56.53) * mm});
            skLineSegment(sketch, "E1522", {"start": v(324.75, -56.53) * mm, "end": v(324.74, -56.4) * mm});
            skLineSegment(sketch, "E1523", {"start": v(324.74, -56.4) * mm, "end": v(324.74, -56.27) * mm});
            skLineSegment(sketch, "E1524", {"start": v(324.74, -56.27) * mm, "end": v(324.74, -56.14) * mm});
            skLineSegment(sketch, "E1525", {"start": v(324.74, -56.14) * mm, "end": v(324.75, -56.01) * mm});
            skLineSegment(sketch, "E1526", {"start": v(324.75, -56.01) * mm, "end": v(324.76, -55.88) * mm});
            skLineSegment(sketch, "E1527", {"start": v(324.76, -55.88) * mm, "end": v(324.77, -55.75) * mm});
            skLineSegment(sketch, "E1528", {"start": v(324.77, -55.75) * mm, "end": v(324.78, -55.62) * mm});
            skLineSegment(sketch, "E1529", {"start": v(324.78, -55.62) * mm, "end": v(324.8, -55.49) * mm});
            skLineSegment(sketch, "E1530", {"start": v(324.8, -55.49) * mm, "end": v(324.82, -55.36) * mm});
            skLineSegment(sketch, "E1531", {"start": v(324.82, -55.36) * mm, "end": v(324.84, -55.22) * mm});
            skLineSegment(sketch, "E1532", {"start": v(324.84, -55.22) * mm, "end": v(324.87, -55.09) * mm});
            skLineSegment(sketch, "E1533", {"start": v(324.87, -55.09) * mm, "end": v(324.9, -54.95) * mm});
            skLineSegment(sketch, "E1534", {"start": v(324.9, -54.95) * mm, "end": v(324.93, -54.82) * mm});
            skLineSegment(sketch, "E1535", {"start": v(324.93, -54.82) * mm, "end": v(324.96, -54.69) * mm});
            skLineSegment(sketch, "E1536", {"start": v(324.96, -54.69) * mm, "end": v(325, -54.55) * mm});
            skLineSegment(sketch, "E1537", {"start": v(325, -54.55) * mm, "end": v(325.05, -54.42) * mm});
            skLineSegment(sketch, "E1538", {"start": v(325.05, -54.42) * mm, "end": v(325.1, -54.29) * mm});
            skLineSegment(sketch, "E1539", {"start": v(325.1, -54.29) * mm, "end": v(325.15, -54.15) * mm});
            skLineSegment(sketch, "E1540", {"start": v(325.15, -54.15) * mm, "end": v(325.2, -54.02) * mm});
            skLineSegment(sketch, "E1541", {"start": v(325.2, -54.02) * mm, "end": v(325.26, -53.89) * mm});
            skLineSegment(sketch, "E1542", {"start": v(325.26, -53.89) * mm, "end": v(325.32, -53.76) * mm});
            skLineSegment(sketch, "E1543", {"start": v(325.32, -53.76) * mm, "end": v(325.38, -53.63) * mm});
            skLineSegment(sketch, "E1544", {"start": v(325.38, -53.63) * mm, "end": v(325.45, -53.5) * mm});
            skLineSegment(sketch, "E1545", {"start": v(325.45, -53.5) * mm, "end": v(325.53, -53.37) * mm});
            skLineSegment(sketch, "E1546", {"start": v(325.53, -53.37) * mm, "end": v(325.6, -53.25) * mm});
            skLineSegment(sketch, "E1547", {"start": v(325.6, -53.25) * mm, "end": v(325.68, -53.12) * mm});
            skLineSegment(sketch, "E1548", {"start": v(325.68, -53.12) * mm, "end": v(325.76, -53) * mm});
            skLineSegment(sketch, "E1549", {"start": v(325.76, -53) * mm, "end": v(325.85, -52.88) * mm});
            skLineSegment(sketch, "E1550", {"start": v(325.85, -52.88) * mm, "end": v(325.94, -52.76) * mm});
            skLineSegment(sketch, "E1551", {"start": v(325.94, -52.76) * mm, "end": v(326.03, -52.64) * mm});
            skLineSegment(sketch, "E1552", {"start": v(326.03, -52.64) * mm, "end": v(326.12, -52.53) * mm});
            skLineSegment(sketch, "E1553", {"start": v(326.12, -52.53) * mm, "end": v(326.22, -52.42) * mm});
            skLineSegment(sketch, "E1554", {"start": v(326.22, -52.42) * mm, "end": v(326.32, -52.3) * mm});
            skLineSegment(sketch, "E1555", {"start": v(326.32, -52.3) * mm, "end": v(326.43, -52.2) * mm});
            skLineSegment(sketch, "E1556", {"start": v(326.43, -52.2) * mm, "end": v(326.53, -52.1) * mm});
            skLineSegment(sketch, "E1557", {"start": v(326.53, -52.1) * mm, "end": v(326.64, -52) * mm});
            skLineSegment(sketch, "E1558", {"start": v(326.64, -52) * mm, "end": v(326.75, -51.9) * mm});
            skLineSegment(sketch, "E1559", {"start": v(326.75, -51.9) * mm, "end": v(326.87, -51.8) * mm});
            skLineSegment(sketch, "E1560", {"start": v(326.87, -51.8) * mm, "end": v(326.98, -51.71) * mm});
            skLineSegment(sketch, "E1561", {"start": v(326.98, -51.71) * mm, "end": v(327.1, -51.62) * mm});
            skLineSegment(sketch, "E1562", {"start": v(327.1, -51.62) * mm, "end": v(327.22, -51.54) * mm});
            skLineSegment(sketch, "E1563", {"start": v(327.22, -51.54) * mm, "end": v(327.35, -51.46) * mm});
            skLineSegment(sketch, "E1564", {"start": v(327.35, -51.46) * mm, "end": v(327.47, -51.38) * mm});
            skLineSegment(sketch, "E1565", {"start": v(327.47, -51.38) * mm, "end": v(327.6, -51.3) * mm});
            skLineSegment(sketch, "E1566", {"start": v(327.6, -51.3) * mm, "end": v(327.72, -51.23) * mm});
            skLineSegment(sketch, "E1567", {"start": v(327.72, -51.23) * mm, "end": v(327.85, -51.16) * mm});
            skLineSegment(sketch, "E1568", {"start": v(327.85, -51.16) * mm, "end": v(327.98, -51.1) * mm});
            skLineSegment(sketch, "E1569", {"start": v(327.98, -51.1) * mm, "end": v(328.11, -51.03) * mm});
            skLineSegment(sketch, "E1570", {"start": v(328.11, -51.03) * mm, "end": v(328.24, -50.98) * mm});
            skLineSegment(sketch, "E1571", {"start": v(328.24, -50.98) * mm, "end": v(328.38, -50.92) * mm});
            skLineSegment(sketch, "E1572", {"start": v(328.38, -50.92) * mm, "end": v(328.5, -50.87) * mm});
            skLineSegment(sketch, "E1573", {"start": v(328.5, -50.87) * mm, "end": v(328.64, -50.82) * mm});
            skLineSegment(sketch, "E1574", {"start": v(328.64, -50.82) * mm, "end": v(328.78, -50.78) * mm});
            skLineSegment(sketch, "E1575", {"start": v(328.78, -50.78) * mm, "end": v(328.91, -50.74) * mm});
            skLineSegment(sketch, "E1576", {"start": v(328.91, -50.74) * mm, "end": v(329.04, -50.7) * mm});
            skLineSegment(sketch, "E1577", {"start": v(329.04, -50.7) * mm, "end": v(329.18, -50.67) * mm});
            skLineSegment(sketch, "E1578", {"start": v(329.18, -50.67) * mm, "end": v(329.31, -50.64) * mm});
            skLineSegment(sketch, "E1579", {"start": v(329.31, -50.64) * mm, "end": v(329.45, -50.61) * mm});
            skLineSegment(sketch, "E1580", {"start": v(329.45, -50.61) * mm, "end": v(329.58, -50.6) * mm});
            skLineSegment(sketch, "E1581", {"start": v(329.58, -50.6) * mm, "end": v(329.71, -50.57) * mm});
            skLineSegment(sketch, "E1582", {"start": v(329.71, -50.57) * mm, "end": v(329.84, -50.56) * mm});
            skLineSegment(sketch, "E1583", {"start": v(329.84, -50.56) * mm, "end": v(329.98, -50.54) * mm});
            skLineSegment(sketch, "E1584", {"start": v(329.98, -50.54) * mm, "end": v(330.1, -50.53) * mm});
            skLineSegment(sketch, "E1585", {"start": v(330.1, -50.53) * mm, "end": v(330.24, -50.52) * mm});
            skLineSegment(sketch, "E1586", {"start": v(330.24, -50.52) * mm, "end": v(330.37, -50.52) * mm});
            skLineSegment(sketch, "E1587", {"start": v(330.37, -50.52) * mm, "end": v(330.5, -50.52) * mm});
            skLineSegment(sketch, "E1588", {"start": v(330.5, 79.48) * mm, "end": v(330.62, 79.48) * mm});
            skLineSegment(sketch, "E1589", {"start": v(330.62, 79.48) * mm, "end": v(330.75, 79.48) * mm});
            skLineSegment(sketch, "E1590", {"start": v(330.75, 79.48) * mm, "end": v(330.88, 79.47) * mm});
            skLineSegment(sketch, "E1591", {"start": v(330.88, 79.47) * mm, "end": v(331, 79.46) * mm});
            skLineSegment(sketch, "E1592", {"start": v(331, 79.46) * mm, "end": v(331.14, 79.44) * mm});
            skLineSegment(sketch, "E1593", {"start": v(331.14, 79.44) * mm, "end": v(331.27, 79.43) * mm});
            skLineSegment(sketch, "E1594", {"start": v(331.27, 79.43) * mm, "end": v(331.4, 79.4) * mm});
            skLineSegment(sketch, "E1595", {"start": v(331.4, 79.4) * mm, "end": v(331.54, 79.39) * mm});
            skLineSegment(sketch, "E1596", {"start": v(331.54, 79.39) * mm, "end": v(331.67, 79.36) * mm});
            skLineSegment(sketch, "E1597", {"start": v(331.67, 79.36) * mm, "end": v(331.8, 79.33) * mm});
            skLineSegment(sketch, "E1598", {"start": v(331.8, 79.33) * mm, "end": v(331.94, 79.3) * mm});
            skLineSegment(sketch, "E1599", {"start": v(331.94, 79.3) * mm, "end": v(332.07, 79.26) * mm});
            skLineSegment(sketch, "E1600", {"start": v(332.07, 79.26) * mm, "end": v(332.2, 79.22) * mm});
            skLineSegment(sketch, "E1601", {"start": v(332.2, 79.22) * mm, "end": v(332.34, 79.18) * mm});
            skLineSegment(sketch, "E1602", {"start": v(332.34, 79.18) * mm, "end": v(332.48, 79.13) * mm});
            skLineSegment(sketch, "E1603", {"start": v(332.48, 79.13) * mm, "end": v(332.6, 79.08) * mm});
            skLineSegment(sketch, "E1604", {"start": v(332.6, 79.08) * mm, "end": v(332.74, 79.02) * mm});
            skLineSegment(sketch, "E1605", {"start": v(332.74, 79.02) * mm, "end": v(332.87, 78.97) * mm});
            skLineSegment(sketch, "E1606", {"start": v(332.87, 78.97) * mm, "end": v(333, 78.9) * mm});
            skLineSegment(sketch, "E1607", {"start": v(333, 78.9) * mm, "end": v(333.13, 78.84) * mm});
            skLineSegment(sketch, "E1608", {"start": v(333.13, 78.84) * mm, "end": v(333.26, 78.77) * mm});
            skLineSegment(sketch, "E1609", {"start": v(333.26, 78.77) * mm, "end": v(333.39, 78.7) * mm});
            skLineSegment(sketch, "E1610", {"start": v(333.39, 78.7) * mm, "end": v(333.51, 78.62) * mm});
            skLineSegment(sketch, "E1611", {"start": v(333.51, 78.62) * mm, "end": v(333.64, 78.54) * mm});
            skLineSegment(sketch, "E1612", {"start": v(333.64, 78.54) * mm, "end": v(333.76, 78.46) * mm});
            skLineSegment(sketch, "E1613", {"start": v(333.76, 78.46) * mm, "end": v(333.88, 78.38) * mm});
            skLineSegment(sketch, "E1614", {"start": v(333.88, 78.38) * mm, "end": v(334, 78.29) * mm});
            skLineSegment(sketch, "E1615", {"start": v(334, 78.29) * mm, "end": v(334.12, 78.2) * mm});
            skLineSegment(sketch, "E1616", {"start": v(334.12, 78.2) * mm, "end": v(334.23, 78.1) * mm});
            skLineSegment(sketch, "E1617", {"start": v(334.23, 78.1) * mm, "end": v(334.34, 78) * mm});
            skLineSegment(sketch, "E1618", {"start": v(334.34, 78) * mm, "end": v(334.45, 77.9) * mm});
            skLineSegment(sketch, "E1619", {"start": v(334.45, 77.9) * mm, "end": v(334.56, 77.8) * mm});
            skLineSegment(sketch, "E1620", {"start": v(334.56, 77.8) * mm, "end": v(334.66, 77.7) * mm});
            skLineSegment(sketch, "E1621", {"start": v(334.66, 77.7) * mm, "end": v(334.76, 77.58) * mm});
            skLineSegment(sketch, "E1622", {"start": v(334.76, 77.58) * mm, "end": v(334.86, 77.47) * mm});
            skLineSegment(sketch, "E1623", {"start": v(334.86, 77.47) * mm, "end": v(334.96, 77.36) * mm});
            skLineSegment(sketch, "E1624", {"start": v(334.96, 77.36) * mm, "end": v(335.05, 77.24) * mm});
            skLineSegment(sketch, "E1625", {"start": v(335.05, 77.24) * mm, "end": v(335.14, 77.12) * mm});
            skLineSegment(sketch, "E1626", {"start": v(335.14, 77.12) * mm, "end": v(335.22, 77) * mm});
            skLineSegment(sketch, "E1627", {"start": v(335.22, 77) * mm, "end": v(335.3, 76.88) * mm});
            skLineSegment(sketch, "E1628", {"start": v(335.3, 76.88) * mm, "end": v(335.38, 76.75) * mm});
            skLineSegment(sketch, "E1629", {"start": v(335.38, 76.75) * mm, "end": v(335.46, 76.63) * mm});
            skLineSegment(sketch, "E1630", {"start": v(335.46, 76.63) * mm, "end": v(335.53, 76.5) * mm});
            skLineSegment(sketch, "E1631", {"start": v(335.53, 76.5) * mm, "end": v(335.6, 76.37) * mm});
            skLineSegment(sketch, "E1632", {"start": v(335.6, 76.37) * mm, "end": v(335.67, 76.24) * mm});
            skLineSegment(sketch, "E1633", {"start": v(335.67, 76.24) * mm, "end": v(335.73, 76.11) * mm});
            skLineSegment(sketch, "E1634", {"start": v(335.73, 76.11) * mm, "end": v(335.78, 75.98) * mm});
            skLineSegment(sketch, "E1635", {"start": v(335.78, 75.98) * mm, "end": v(335.84, 75.85) * mm});
            skLineSegment(sketch, "E1636", {"start": v(335.84, 75.85) * mm, "end": v(335.89, 75.71) * mm});
            skLineSegment(sketch, "E1637", {"start": v(335.89, 75.71) * mm, "end": v(335.94, 75.58) * mm});
            skLineSegment(sketch, "E1638", {"start": v(335.94, 75.58) * mm, "end": v(335.98, 75.45) * mm});
            skLineSegment(sketch, "E1639", {"start": v(335.98, 75.45) * mm, "end": v(336.02, 75.31) * mm});
            skLineSegment(sketch, "E1640", {"start": v(336.02, 75.31) * mm, "end": v(336.06, 75.18) * mm});
            skLineSegment(sketch, "E1641", {"start": v(336.06, 75.18) * mm, "end": v(336.1, 75.05) * mm});
            skLineSegment(sketch, "E1642", {"start": v(336.1, 75.05) * mm, "end": v(336.12, 74.91) * mm});
            skLineSegment(sketch, "E1643", {"start": v(336.12, 74.91) * mm, "end": v(336.15, 74.78) * mm});
            skLineSegment(sketch, "E1644", {"start": v(336.15, 74.78) * mm, "end": v(336.17, 74.64) * mm});
            skLineSegment(sketch, "E1645", {"start": v(336.17, 74.64) * mm, "end": v(336.19, 74.51) * mm});
            skLineSegment(sketch, "E1646", {"start": v(336.19, 74.51) * mm, "end": v(336.2, 74.38) * mm});
            skLineSegment(sketch, "E1647", {"start": v(336.2, 74.38) * mm, "end": v(336.22, 74.25) * mm});
            skLineSegment(sketch, "E1648", {"start": v(336.22, 74.25) * mm, "end": v(336.23, 74.12) * mm});
            skLineSegment(sketch, "E1649", {"start": v(336.23, 74.12) * mm, "end": v(336.24, 73.99) * mm});
            skLineSegment(sketch, "E1650", {"start": v(336.24, 73.99) * mm, "end": v(336.24, 73.86) * mm});
            skLineSegment(sketch, "E1651", {"start": v(336.24, 73.86) * mm, "end": v(336.24, 73.73) * mm});
            skLineSegment(sketch, "E1652", {"start": v(336.24, 73.73) * mm, "end": v(336.24, 73.6) * mm});
            skLineSegment(sketch, "E1653", {"start": v(336.24, 73.6) * mm, "end": v(336.24, 73.47) * mm});
            skLineSegment(sketch, "E1654", {"start": v(336.24, 73.47) * mm, "end": v(336.23, 73.35) * mm});
            skLineSegment(sketch, "E1655", {"start": v(336.23, 73.35) * mm, "end": v(336.22, 73.21) * mm});
            skLineSegment(sketch, "E1656", {"start": v(336.22, 73.21) * mm, "end": v(336.2, 73.08) * mm});
            skLineSegment(sketch, "E1657", {"start": v(336.2, 73.08) * mm, "end": v(336.19, 72.95) * mm});
            skLineSegment(sketch, "E1658", {"start": v(336.19, 72.95) * mm, "end": v(336.17, 72.82) * mm});
            skLineSegment(sketch, "E1659", {"start": v(336.17, 72.82) * mm, "end": v(336.15, 72.68) * mm});
            skLineSegment(sketch, "E1660", {"start": v(336.15, 72.68) * mm, "end": v(336.12, 72.55) * mm});
            skLineSegment(sketch, "E1661", {"start": v(336.12, 72.55) * mm, "end": v(336.1, 72.42) * mm});
            skLineSegment(sketch, "E1662", {"start": v(336.1, 72.42) * mm, "end": v(336.06, 72.28) * mm});
            skLineSegment(sketch, "E1663", {"start": v(336.06, 72.28) * mm, "end": v(336.02, 72.15) * mm});
            skLineSegment(sketch, "E1664", {"start": v(336.02, 72.15) * mm, "end": v(335.98, 72.02) * mm});
            skLineSegment(sketch, "E1665", {"start": v(335.98, 72.02) * mm, "end": v(335.94, 71.88) * mm});
            skLineSegment(sketch, "E1666", {"start": v(335.94, 71.88) * mm, "end": v(335.89, 71.75) * mm});
            skLineSegment(sketch, "E1667", {"start": v(335.89, 71.75) * mm, "end": v(335.84, 71.61) * mm});
            skLineSegment(sketch, "E1668", {"start": v(335.84, 71.61) * mm, "end": v(335.78, 71.48) * mm});
            skLineSegment(sketch, "E1669", {"start": v(335.78, 71.48) * mm, "end": v(335.73, 71.35) * mm});
            skLineSegment(sketch, "E1670", {"start": v(335.73, 71.35) * mm, "end": v(335.67, 71.22) * mm});
            skLineSegment(sketch, "E1671", {"start": v(335.67, 71.22) * mm, "end": v(335.6, 71.1) * mm});
            skLineSegment(sketch, "E1672", {"start": v(335.6, 71.1) * mm, "end": v(335.53, 70.96) * mm});
            skLineSegment(sketch, "E1673", {"start": v(335.53, 70.96) * mm, "end": v(335.46, 70.83) * mm});
            skLineSegment(sketch, "E1674", {"start": v(335.46, 70.83) * mm, "end": v(335.38, 70.7) * mm});
            skLineSegment(sketch, "E1675", {"start": v(335.38, 70.7) * mm, "end": v(335.3, 70.58) * mm});
            skLineSegment(sketch, "E1676", {"start": v(335.3, 70.58) * mm, "end": v(335.22, 70.46) * mm});
            skLineSegment(sketch, "E1677", {"start": v(335.22, 70.46) * mm, "end": v(335.14, 70.34) * mm});
            skLineSegment(sketch, "E1678", {"start": v(335.14, 70.34) * mm, "end": v(335.05, 70.22) * mm});
            skLineSegment(sketch, "E1679", {"start": v(335.05, 70.22) * mm, "end": v(334.96, 70.1) * mm});
            skLineSegment(sketch, "E1680", {"start": v(334.96, 70.1) * mm, "end": v(334.86, 70) * mm});
            skLineSegment(sketch, "E1681", {"start": v(334.86, 70) * mm, "end": v(334.76, 69.88) * mm});
            skLineSegment(sketch, "E1682", {"start": v(334.76, 69.88) * mm, "end": v(334.66, 69.77) * mm});
            skLineSegment(sketch, "E1683", {"start": v(334.66, 69.77) * mm, "end": v(334.56, 69.67) * mm});
            skLineSegment(sketch, "E1684", {"start": v(334.56, 69.67) * mm, "end": v(334.45, 69.56) * mm});
            skLineSegment(sketch, "E1685", {"start": v(334.45, 69.56) * mm, "end": v(334.34, 69.46) * mm});
            skLineSegment(sketch, "E1686", {"start": v(334.34, 69.46) * mm, "end": v(334.23, 69.36) * mm});
            skLineSegment(sketch, "E1687", {"start": v(334.23, 69.36) * mm, "end": v(334.12, 69.27) * mm});
            skLineSegment(sketch, "E1688", {"start": v(334.12, 69.27) * mm, "end": v(334, 69.18) * mm});
            skLineSegment(sketch, "E1689", {"start": v(334, 69.18) * mm, "end": v(333.88, 69.09) * mm});
            skLineSegment(sketch, "E1690", {"start": v(333.88, 69.09) * mm, "end": v(333.76, 69) * mm});
            skLineSegment(sketch, "E1691", {"start": v(333.76, 69) * mm, "end": v(333.64, 68.92) * mm});
            skLineSegment(sketch, "E1692", {"start": v(333.64, 68.92) * mm, "end": v(333.51, 68.84) * mm});
            skLineSegment(sketch, "E1693", {"start": v(333.51, 68.84) * mm, "end": v(333.39, 68.76) * mm});
            skLineSegment(sketch, "E1694", {"start": v(333.39, 68.76) * mm, "end": v(333.26, 68.7) * mm});
            skLineSegment(sketch, "E1695", {"start": v(333.26, 68.7) * mm, "end": v(333.13, 68.62) * mm});
            skLineSegment(sketch, "E1696", {"start": v(333.13, 68.62) * mm, "end": v(333, 68.56) * mm});
            skLineSegment(sketch, "E1697", {"start": v(333, 68.56) * mm, "end": v(332.87, 68.5) * mm});
            skLineSegment(sketch, "E1698", {"start": v(332.87, 68.5) * mm, "end": v(332.74, 68.44) * mm});
            skLineSegment(sketch, "E1699", {"start": v(332.74, 68.44) * mm, "end": v(332.6, 68.38) * mm});
            skLineSegment(sketch, "E1700", {"start": v(332.6, 68.38) * mm, "end": v(332.48, 68.33) * mm});
            skLineSegment(sketch, "E1701", {"start": v(332.48, 68.33) * mm, "end": v(332.34, 68.29) * mm});
            skLineSegment(sketch, "E1702", {"start": v(332.34, 68.29) * mm, "end": v(332.2, 68.24) * mm});
            skLineSegment(sketch, "E1703", {"start": v(332.2, 68.24) * mm, "end": v(332.07, 68.2) * mm});
            skLineSegment(sketch, "E1704", {"start": v(332.07, 68.2) * mm, "end": v(331.94, 68.17) * mm});
            skLineSegment(sketch, "E1705", {"start": v(331.94, 68.17) * mm, "end": v(331.8, 68.13) * mm});
            skLineSegment(sketch, "E1706", {"start": v(331.8, 68.13) * mm, "end": v(331.67, 68.1) * mm});
            skLineSegment(sketch, "E1707", {"start": v(331.67, 68.1) * mm, "end": v(331.54, 68.08) * mm});
            skLineSegment(sketch, "E1708", {"start": v(331.54, 68.08) * mm, "end": v(331.4, 68.05) * mm});
            skLineSegment(sketch, "E1709", {"start": v(331.4, 68.05) * mm, "end": v(331.27, 68.03) * mm});
            skLineSegment(sketch, "E1710", {"start": v(331.27, 68.03) * mm, "end": v(331.14, 68.02) * mm});
            skLineSegment(sketch, "E1711", {"start": v(331.14, 68.02) * mm, "end": v(331, 68) * mm});
            skLineSegment(sketch, "E1712", {"start": v(331, 68) * mm, "end": v(330.88, 68) * mm});
            skLineSegment(sketch, "E1713", {"start": v(330.88, 68) * mm, "end": v(330.75, 67.99) * mm});
            skLineSegment(sketch, "E1714", {"start": v(330.75, 67.99) * mm, "end": v(330.62, 67.98) * mm});
            skLineSegment(sketch, "E1715", {"start": v(330.62, 67.98) * mm, "end": v(330.5, 67.98) * mm});
            skLineSegment(sketch, "E1716", {"start": v(330.5, 67.98) * mm, "end": v(330.37, 67.98) * mm});
            skLineSegment(sketch, "E1717", {"start": v(330.37, 67.98) * mm, "end": v(330.24, 67.99) * mm});
            skLineSegment(sketch, "E1718", {"start": v(330.24, 67.99) * mm, "end": v(330.1, 68) * mm});
            skLineSegment(sketch, "E1719", {"start": v(330.1, 68) * mm, "end": v(329.98, 68) * mm});
            skLineSegment(sketch, "E1720", {"start": v(329.98, 68) * mm, "end": v(329.84, 68.02) * mm});
            skLineSegment(sketch, "E1721", {"start": v(329.84, 68.02) * mm, "end": v(329.71, 68.03) * mm});
            skLineSegment(sketch, "E1722", {"start": v(329.71, 68.03) * mm, "end": v(329.58, 68.05) * mm});
            skLineSegment(sketch, "E1723", {"start": v(329.58, 68.05) * mm, "end": v(329.45, 68.08) * mm});
            skLineSegment(sketch, "E1724", {"start": v(329.45, 68.08) * mm, "end": v(329.31, 68.1) * mm});
            skLineSegment(sketch, "E1725", {"start": v(329.31, 68.1) * mm, "end": v(329.18, 68.13) * mm});
            skLineSegment(sketch, "E1726", {"start": v(329.18, 68.13) * mm, "end": v(329.04, 68.17) * mm});
            skLineSegment(sketch, "E1727", {"start": v(329.04, 68.17) * mm, "end": v(328.91, 68.2) * mm});
            skLineSegment(sketch, "E1728", {"start": v(328.91, 68.2) * mm, "end": v(328.78, 68.24) * mm});
            skLineSegment(sketch, "E1729", {"start": v(328.78, 68.24) * mm, "end": v(328.64, 68.29) * mm});
            skLineSegment(sketch, "E1730", {"start": v(328.64, 68.29) * mm, "end": v(328.5, 68.33) * mm});
            skLineSegment(sketch, "E1731", {"start": v(328.5, 68.33) * mm, "end": v(328.38, 68.38) * mm});
            skLineSegment(sketch, "E1732", {"start": v(328.38, 68.38) * mm, "end": v(328.24, 68.44) * mm});
            skLineSegment(sketch, "E1733", {"start": v(328.24, 68.44) * mm, "end": v(328.11, 68.5) * mm});
            skLineSegment(sketch, "E1734", {"start": v(328.11, 68.5) * mm, "end": v(327.98, 68.56) * mm});
            skLineSegment(sketch, "E1735", {"start": v(327.98, 68.56) * mm, "end": v(327.85, 68.62) * mm});
            skLineSegment(sketch, "E1736", {"start": v(327.85, 68.62) * mm, "end": v(327.72, 68.7) * mm});
            skLineSegment(sketch, "E1737", {"start": v(327.72, 68.7) * mm, "end": v(327.6, 68.76) * mm});
            skLineSegment(sketch, "E1738", {"start": v(327.6, 68.76) * mm, "end": v(327.47, 68.84) * mm});
            skLineSegment(sketch, "E1739", {"start": v(327.47, 68.84) * mm, "end": v(327.35, 68.92) * mm});
            skLineSegment(sketch, "E1740", {"start": v(327.35, 68.92) * mm, "end": v(327.22, 69) * mm});
            skLineSegment(sketch, "E1741", {"start": v(327.22, 69) * mm, "end": v(327.1, 69.09) * mm});
            skLineSegment(sketch, "E1742", {"start": v(327.1, 69.09) * mm, "end": v(326.98, 69.18) * mm});
            skLineSegment(sketch, "E1743", {"start": v(326.98, 69.18) * mm, "end": v(326.87, 69.27) * mm});
            skLineSegment(sketch, "E1744", {"start": v(326.87, 69.27) * mm, "end": v(326.75, 69.36) * mm});
            skLineSegment(sketch, "E1745", {"start": v(326.75, 69.36) * mm, "end": v(326.64, 69.46) * mm});
            skLineSegment(sketch, "E1746", {"start": v(326.64, 69.46) * mm, "end": v(326.53, 69.56) * mm});
            skLineSegment(sketch, "E1747", {"start": v(326.53, 69.56) * mm, "end": v(326.43, 69.67) * mm});
            skLineSegment(sketch, "E1748", {"start": v(326.43, 69.67) * mm, "end": v(326.32, 69.77) * mm});
            skLineSegment(sketch, "E1749", {"start": v(326.32, 69.77) * mm, "end": v(326.22, 69.88) * mm});
            skLineSegment(sketch, "E1750", {"start": v(326.22, 69.88) * mm, "end": v(326.12, 70) * mm});
            skLineSegment(sketch, "E1751", {"start": v(326.12, 70) * mm, "end": v(326.03, 70.1) * mm});
            skLineSegment(sketch, "E1752", {"start": v(326.03, 70.1) * mm, "end": v(325.94, 70.22) * mm});
            skLineSegment(sketch, "E1753", {"start": v(325.94, 70.22) * mm, "end": v(325.85, 70.34) * mm});
            skLineSegment(sketch, "E1754", {"start": v(325.85, 70.34) * mm, "end": v(325.76, 70.46) * mm});
            skLineSegment(sketch, "E1755", {"start": v(325.76, 70.46) * mm, "end": v(325.68, 70.58) * mm});
            skLineSegment(sketch, "E1756", {"start": v(325.68, 70.58) * mm, "end": v(325.6, 70.7) * mm});
            skLineSegment(sketch, "E1757", {"start": v(325.6, 70.7) * mm, "end": v(325.53, 70.83) * mm});
            skLineSegment(sketch, "E1758", {"start": v(325.53, 70.83) * mm, "end": v(325.45, 70.96) * mm});
            skLineSegment(sketch, "E1759", {"start": v(325.45, 70.96) * mm, "end": v(325.38, 71.1) * mm});
            skLineSegment(sketch, "E1760", {"start": v(325.38, 71.1) * mm, "end": v(325.32, 71.22) * mm});
            skLineSegment(sketch, "E1761", {"start": v(325.32, 71.22) * mm, "end": v(325.26, 71.35) * mm});
            skLineSegment(sketch, "E1762", {"start": v(325.26, 71.35) * mm, "end": v(325.2, 71.48) * mm});
            skLineSegment(sketch, "E1763", {"start": v(325.2, 71.48) * mm, "end": v(325.15, 71.61) * mm});
            skLineSegment(sketch, "E1764", {"start": v(325.15, 71.61) * mm, "end": v(325.1, 71.75) * mm});
            skLineSegment(sketch, "E1765", {"start": v(325.1, 71.75) * mm, "end": v(325.05, 71.88) * mm});
            skLineSegment(sketch, "E1766", {"start": v(325.05, 71.88) * mm, "end": v(325, 72.02) * mm});
            skLineSegment(sketch, "E1767", {"start": v(325, 72.02) * mm, "end": v(324.96, 72.15) * mm});
            skLineSegment(sketch, "E1768", {"start": v(324.96, 72.15) * mm, "end": v(324.93, 72.28) * mm});
            skLineSegment(sketch, "E1769", {"start": v(324.93, 72.28) * mm, "end": v(324.9, 72.42) * mm});
            skLineSegment(sketch, "E1770", {"start": v(324.9, 72.42) * mm, "end": v(324.87, 72.55) * mm});
            skLineSegment(sketch, "E1771", {"start": v(324.87, 72.55) * mm, "end": v(324.84, 72.68) * mm});
            skLineSegment(sketch, "E1772", {"start": v(324.84, 72.68) * mm, "end": v(324.82, 72.82) * mm});
            skLineSegment(sketch, "E1773", {"start": v(324.82, 72.82) * mm, "end": v(324.8, 72.95) * mm});
            skLineSegment(sketch, "E1774", {"start": v(324.8, 72.95) * mm, "end": v(324.78, 73.08) * mm});
            skLineSegment(sketch, "E1775", {"start": v(324.78, 73.08) * mm, "end": v(324.77, 73.21) * mm});
            skLineSegment(sketch, "E1776", {"start": v(324.77, 73.21) * mm, "end": v(324.76, 73.35) * mm});
            skLineSegment(sketch, "E1777", {"start": v(324.76, 73.35) * mm, "end": v(324.75, 73.47) * mm});
            skLineSegment(sketch, "E1778", {"start": v(324.75, 73.47) * mm, "end": v(324.74, 73.6) * mm});
            skLineSegment(sketch, "E1779", {"start": v(324.74, 73.6) * mm, "end": v(324.74, 73.73) * mm});
            skLineSegment(sketch, "E1780", {"start": v(324.74, 73.73) * mm, "end": v(324.74, 73.86) * mm});
            skLineSegment(sketch, "E1781", {"start": v(324.74, 73.86) * mm, "end": v(324.75, 73.99) * mm});
            skLineSegment(sketch, "E1782", {"start": v(324.75, 73.99) * mm, "end": v(324.76, 74.12) * mm});
            skLineSegment(sketch, "E1783", {"start": v(324.76, 74.12) * mm, "end": v(324.77, 74.25) * mm});
            skLineSegment(sketch, "E1784", {"start": v(324.77, 74.25) * mm, "end": v(324.78, 74.38) * mm});
            skLineSegment(sketch, "E1785", {"start": v(324.78, 74.38) * mm, "end": v(324.8, 74.51) * mm});
            skLineSegment(sketch, "E1786", {"start": v(324.8, 74.51) * mm, "end": v(324.82, 74.64) * mm});
            skLineSegment(sketch, "E1787", {"start": v(324.82, 74.64) * mm, "end": v(324.84, 74.78) * mm});
            skLineSegment(sketch, "E1788", {"start": v(324.84, 74.78) * mm, "end": v(324.87, 74.91) * mm});
            skLineSegment(sketch, "E1789", {"start": v(324.87, 74.91) * mm, "end": v(324.9, 75.05) * mm});
            skLineSegment(sketch, "E1790", {"start": v(324.9, 75.05) * mm, "end": v(324.93, 75.18) * mm});
            skLineSegment(sketch, "E1791", {"start": v(324.93, 75.18) * mm, "end": v(324.96, 75.31) * mm});
            skLineSegment(sketch, "E1792", {"start": v(324.96, 75.31) * mm, "end": v(325, 75.45) * mm});
            skLineSegment(sketch, "E1793", {"start": v(325, 75.45) * mm, "end": v(325.05, 75.58) * mm});
            skLineSegment(sketch, "E1794", {"start": v(325.05, 75.58) * mm, "end": v(325.1, 75.71) * mm});
            skLineSegment(sketch, "E1795", {"start": v(325.1, 75.71) * mm, "end": v(325.15, 75.85) * mm});
            skLineSegment(sketch, "E1796", {"start": v(325.15, 75.85) * mm, "end": v(325.2, 75.98) * mm});
            skLineSegment(sketch, "E1797", {"start": v(325.2, 75.98) * mm, "end": v(325.26, 76.11) * mm});
            skLineSegment(sketch, "E1798", {"start": v(325.26, 76.11) * mm, "end": v(325.32, 76.24) * mm});
            skLineSegment(sketch, "E1799", {"start": v(325.32, 76.24) * mm, "end": v(325.38, 76.37) * mm});
            skLineSegment(sketch, "E1800", {"start": v(325.38, 76.37) * mm, "end": v(325.45, 76.5) * mm});
            skLineSegment(sketch, "E1801", {"start": v(325.45, 76.5) * mm, "end": v(325.53, 76.63) * mm});
            skLineSegment(sketch, "E1802", {"start": v(325.53, 76.63) * mm, "end": v(325.6, 76.75) * mm});
            skLineSegment(sketch, "E1803", {"start": v(325.6, 76.75) * mm, "end": v(325.68, 76.88) * mm});
            skLineSegment(sketch, "E1804", {"start": v(325.68, 76.88) * mm, "end": v(325.76, 77) * mm});
            skLineSegment(sketch, "E1805", {"start": v(325.76, 77) * mm, "end": v(325.85, 77.12) * mm});
            skLineSegment(sketch, "E1806", {"start": v(325.85, 77.12) * mm, "end": v(325.94, 77.24) * mm});
            skLineSegment(sketch, "E1807", {"start": v(325.94, 77.24) * mm, "end": v(326.03, 77.36) * mm});
            skLineSegment(sketch, "E1808", {"start": v(326.03, 77.36) * mm, "end": v(326.12, 77.47) * mm});
            skLineSegment(sketch, "E1809", {"start": v(326.12, 77.47) * mm, "end": v(326.22, 77.58) * mm});
            skLineSegment(sketch, "E1810", {"start": v(326.22, 77.58) * mm, "end": v(326.32, 77.7) * mm});
            skLineSegment(sketch, "E1811", {"start": v(326.32, 77.7) * mm, "end": v(326.43, 77.8) * mm});
            skLineSegment(sketch, "E1812", {"start": v(326.43, 77.8) * mm, "end": v(326.53, 77.9) * mm});
            skLineSegment(sketch, "E1813", {"start": v(326.53, 77.9) * mm, "end": v(326.64, 78) * mm});
            skLineSegment(sketch, "E1814", {"start": v(326.64, 78) * mm, "end": v(326.75, 78.1) * mm});
            skLineSegment(sketch, "E1815", {"start": v(326.75, 78.1) * mm, "end": v(326.87, 78.2) * mm});
            skLineSegment(sketch, "E1816", {"start": v(326.87, 78.2) * mm, "end": v(326.98, 78.29) * mm});
            skLineSegment(sketch, "E1817", {"start": v(326.98, 78.29) * mm, "end": v(327.1, 78.38) * mm});
            skLineSegment(sketch, "E1818", {"start": v(327.1, 78.38) * mm, "end": v(327.22, 78.46) * mm});
            skLineSegment(sketch, "E1819", {"start": v(327.22, 78.46) * mm, "end": v(327.35, 78.54) * mm});
            skLineSegment(sketch, "E1820", {"start": v(327.35, 78.54) * mm, "end": v(327.47, 78.62) * mm});
            skLineSegment(sketch, "E1821", {"start": v(327.47, 78.62) * mm, "end": v(327.6, 78.7) * mm});
            skLineSegment(sketch, "E1822", {"start": v(327.6, 78.7) * mm, "end": v(327.72, 78.77) * mm});
            skLineSegment(sketch, "E1823", {"start": v(327.72, 78.77) * mm, "end": v(327.85, 78.84) * mm});
            skLineSegment(sketch, "E1824", {"start": v(327.85, 78.84) * mm, "end": v(327.98, 78.9) * mm});
            skLineSegment(sketch, "E1825", {"start": v(327.98, 78.9) * mm, "end": v(328.11, 78.97) * mm});
            skLineSegment(sketch, "E1826", {"start": v(328.11, 78.97) * mm, "end": v(328.24, 79.02) * mm});
            skLineSegment(sketch, "E1827", {"start": v(328.24, 79.02) * mm, "end": v(328.38, 79.08) * mm});
            skLineSegment(sketch, "E1828", {"start": v(328.38, 79.08) * mm, "end": v(328.5, 79.13) * mm});
            skLineSegment(sketch, "E1829", {"start": v(328.5, 79.13) * mm, "end": v(328.64, 79.18) * mm});
            skLineSegment(sketch, "E1830", {"start": v(328.64, 79.18) * mm, "end": v(328.78, 79.22) * mm});
            skLineSegment(sketch, "E1831", {"start": v(328.78, 79.22) * mm, "end": v(328.91, 79.26) * mm});
            skLineSegment(sketch, "E1832", {"start": v(328.91, 79.26) * mm, "end": v(329.04, 79.3) * mm});
            skLineSegment(sketch, "E1833", {"start": v(329.04, 79.3) * mm, "end": v(329.18, 79.33) * mm});
            skLineSegment(sketch, "E1834", {"start": v(329.18, 79.33) * mm, "end": v(329.31, 79.36) * mm});
            skLineSegment(sketch, "E1835", {"start": v(329.31, 79.36) * mm, "end": v(329.45, 79.39) * mm});
            skLineSegment(sketch, "E1836", {"start": v(329.45, 79.39) * mm, "end": v(329.58, 79.4) * mm});
            skLineSegment(sketch, "E1837", {"start": v(329.58, 79.4) * mm, "end": v(329.71, 79.43) * mm});
            skLineSegment(sketch, "E1838", {"start": v(329.71, 79.43) * mm, "end": v(329.84, 79.44) * mm});
            skLineSegment(sketch, "E1839", {"start": v(329.84, 79.44) * mm, "end": v(329.98, 79.46) * mm});
            skLineSegment(sketch, "E1840", {"start": v(329.98, 79.46) * mm, "end": v(330.1, 79.47) * mm});
            skLineSegment(sketch, "E1841", {"start": v(330.1, 79.47) * mm, "end": v(330.24, 79.48) * mm});
            skLineSegment(sketch, "E1842", {"start": v(330.24, 79.48) * mm, "end": v(330.37, 79.48) * mm});
            skLineSegment(sketch, "E1843", {"start": v(330.37, 79.48) * mm, "end": v(330.5, 79.48) * mm});
            skLineSegment(sketch, "E1844", {"start": v(313.23, 98.73) * mm, "end": v(313.23, 73.33) * mm});
            skLineSegment(sketch, "E1845", {"start": v(313.23, 73.33) * mm, "end": v(318, 73.33) * mm});
            skLineSegment(sketch, "E1846", {"start": v(318, 73.33) * mm, "end": v(318, -73.33) * mm});
            skLineSegment(sketch, "E1847", {"start": v(318, -73.33) * mm, "end": v(313.23, -73.33) * mm});
            skLineSegment(sketch, "E1848", {"start": v(313.23, -73.33) * mm, "end": v(313.23, -98.73) * mm});
            skLineSegment(sketch, "E1849", {"start": v(313.23, -98.73) * mm, "end": v(318, -98.73) * mm});
            skLineSegment(sketch, "E1850", {"start": v(318, -98.73) * mm, "end": v(343, -98.73) * mm});
            skLineSegment(sketch, "E1851", {"start": v(343, -98.73) * mm, "end": v(343, 98.73) * mm});
            skLineSegment(sketch, "E1852", {"start": v(343, 98.73) * mm, "end": v(318, 98.73) * mm});
            skLineSegment(sketch, "E1853", {"start": v(318, 98.73) * mm, "end": v(313.23, 98.73) * mm});
            skSolve(sketch);
        }
        {
            var Q0;
            Q0 = qSketchRegion(id + "F0", true);
            extrude(context, id + "F1", {"entities" : qUnion([Q0]), "depth" : 6.35 * mm});
        }
    });
